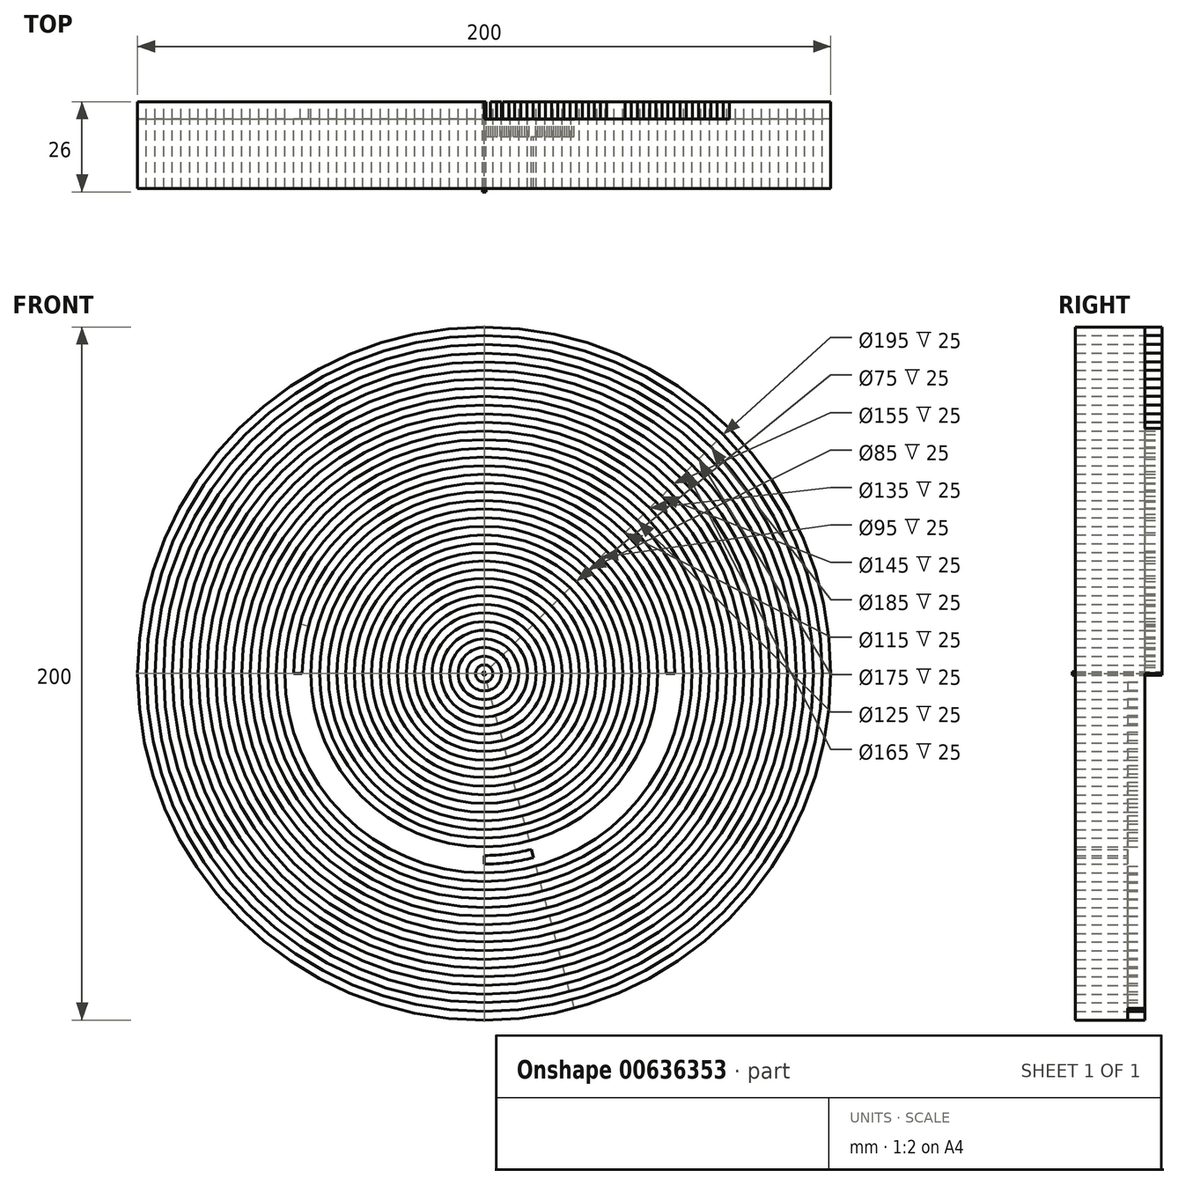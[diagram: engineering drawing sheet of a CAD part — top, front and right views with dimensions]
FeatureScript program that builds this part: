
annotation { "Feature Type Name" : "Feature", "Feature Type Description" : "" }
export const myFeature = defineFeature(function(context is Context, id is Id, definition is map)
    precondition{}
    {
        {
            var Q0;
            Q0=qCreatedBy(makeId("Front.planeOp"),FACE);
            var sketch = newSketch(context, id + "F0", { "sketchPlane" : qUnion([Q0])});
            skCircle(sketch, "E0", {"center": v(0, 0) * mm, "radius": 100 * mm});
            skCircle(sketch, "E1", {"center": v(0, 0) * mm, "radius": 2.5 * mm});
            skCircle(sketch, "E2", {"center": v(0, 0) * mm, "radius": 5 * mm});
            skCircle(sketch, "E3", {"center": v(0, 0) * mm, "radius": 7.5 * mm});
            skCircle(sketch, "E4", {"center": v(0, 0) * mm, "radius": 15 * mm});
            skCircle(sketch, "E5", {"center": v(0, 0) * mm, "radius": 10 * mm});
            skCircle(sketch, "E6", {"center": v(0, 0) * mm, "radius": 12.5 * mm});
            skCircle(sketch, "E7", {"center": v(0, 0) * mm, "radius": 17.5 * mm});
            skCircle(sketch, "E8", {"center": v(0, 0) * mm, "radius": 20 * mm});
            skCircle(sketch, "E9", {"center": v(0, 0) * mm, "radius": 22.5 * mm});
            skCircle(sketch, "E10", {"center": v(0, 0) * mm, "radius": 25 * mm});
            skCircle(sketch, "E11", {"center": v(0, 0) * mm, "radius": 27.5 * mm});
            skCircle(sketch, "E12", {"center": v(0, 0) * mm, "radius": 30 * mm});
            skCircle(sketch, "E13", {"center": v(0, 0) * mm, "radius": 32.5 * mm});
            skCircle(sketch, "E14", {"center": v(0, 0) * mm, "radius": 35 * mm});
            skCircle(sketch, "E15", {"center": v(0, 0) * mm, "radius": 37.5 * mm});
            skCircle(sketch, "E16", {"center": v(0, 0) * mm, "radius": 40 * mm});
            skCircle(sketch, "E17", {"center": v(0, 0) * mm, "radius": 45 * mm});
            skCircle(sketch, "E18", {"center": v(0, 0) * mm, "radius": 50 * mm});
            skCircle(sketch, "E19", {"center": v(0, 0) * mm, "radius": 52.5 * mm});
            skCircle(sketch, "E20", {"center": v(0, 0) * mm, "radius": 55 * mm});
            skCircle(sketch, "E21", {"center": v(0, 0) * mm, "radius": 42.5 * mm});
            skCircle(sketch, "E22", {"center": v(0, 0) * mm, "radius": 47.5 * mm});
            skCircle(sketch, "E23", {"center": v(0, 0) * mm, "radius": 60 * mm});
            skCircle(sketch, "E24", {"center": v(0, 0) * mm, "radius": 57.5 * mm});
            skCircle(sketch, "E25", {"center": v(0, 0) * mm, "radius": 62.5 * mm});
            skCircle(sketch, "E26", {"center": v(0, 0) * mm, "radius": 65 * mm});
            skCircle(sketch, "E27", {"center": v(0, 0) * mm, "radius": 67.5 * mm});
            skCircle(sketch, "E28", {"center": v(0, 0) * mm, "radius": 70 * mm});
            skCircle(sketch, "E29", {"center": v(0, 0) * mm, "radius": 72.5 * mm});
            skCircle(sketch, "E30", {"center": v(0, 0) * mm, "radius": 75 * mm});
            skCircle(sketch, "E31", {"center": v(0, 0) * mm, "radius": 77.5 * mm});
            skCircle(sketch, "E32", {"center": v(0, 0) * mm, "radius": 80 * mm});
            skCircle(sketch, "E33", {"center": v(0, 0) * mm, "radius": 82.5 * mm});
            skCircle(sketch, "E34", {"center": v(0, 0) * mm, "radius": 85 * mm});
            skCircle(sketch, "E35", {"center": v(0, 0) * mm, "radius": 87.5 * mm});
            skCircle(sketch, "E36", {"center": v(0, 0) * mm, "radius": 90 * mm});
            skCircle(sketch, "E37", {"center": v(0, 0) * mm, "radius": 92.5 * mm});
            skCircle(sketch, "E38", {"center": v(0, 0) * mm, "radius": 95 * mm});
            skCircle(sketch, "E39", {"center": v(0, 0) * mm, "radius": 97.5 * mm});
            skLineSegment(sketch, "E40", {"start": v(0, 100) * mm, "end": v(0, -100) * mm});
            skLineSegment(sketch, "E41", {"start": v(100, 0) * mm, "end": v(-100, 0) * mm});
            skLineSegment(sketch, "E42", {"start": v(70.71, 70.71) * mm, "end": v(0, 0) * mm});
            skLineSegment(sketch, "E43", {"start": v(0, 0) * mm, "end": v(25.88, -96.6) * mm});
            skLineSegment(sketch, "E44", {"start": v(25.88, -96.6) * mm, "end": v(0, 0) * mm});
            skLineSegment(sketch, "E45", {"start": v(0, 0) * mm, "end": v(-96.6, 25.88) * mm});
            skCircle(sketch, "E46", {"center": v(0, 0) * mm, "radius": 0.5 * mm});
            skSolve(sketch);
        }
        {
            var Q0;
            {var subQ0=sQuery(id+"F0.wireOp",EDGE,"E42");var subQ1=sQuery(id+"F0.wireOp",EDGE,"E15");var subQ2=makeQuery(id+"F0.imprint","INTERSECT",VERTEX,{"derivedFrom":[subQ1,subQ0]});Q0=makeQuery(id+"F0.imprint","IMPRINT",FACE,{"disambiguationData":[TD([[makeQuery(id+"F0.imprint","IMPRINT",EDGE,{"disambiguationData":[TD([[subQ2,1.0]])],"derivedFrom":subQ1}),-1.0]])]});}
            var Q1;
            {var subQ0=sQuery(id+"F0.wireOp",EDGE,"E41");var subQ1=sQuery(id+"F0.wireOp",EDGE,"E7");var subQ2=makeQuery(id+"F0.imprint","INTERSECT",VERTEX,{"disambiguationData":[OD(0.0)],"derivedFrom":[subQ1,subQ0]});Q1=makeQuery(id+"F0.imprint","IMPRINT",FACE,{"disambiguationData":[TD([[makeQuery(id+"F0.imprint","IMPRINT",EDGE,{"disambiguationData":[TD([[subQ2,1.0]])],"derivedFrom":subQ1}),-1.0]])]});}
            var Q2;
            {var subQ0=sQuery(id+"F0.wireOp",EDGE,"E42");var subQ1=sQuery(id+"F0.wireOp",EDGE,"E26");var subQ2=makeQuery(id+"F0.imprint","INTERSECT",VERTEX,{"derivedFrom":[subQ1,subQ0]});Q2=makeQuery(id+"F0.imprint","IMPRINT",FACE,{"disambiguationData":[TD([[makeQuery(id+"F0.imprint","IMPRINT",EDGE,{"disambiguationData":[TD([[subQ2,-1.0]])],"derivedFrom":subQ1}),-1.0]])]});}
            var Q3;
            {var subQ0=sQuery(id+"F0.wireOp",EDGE,"E45");var subQ1=sQuery(id+"F0.wireOp",EDGE,"E17");var subQ2=makeQuery(id+"F0.imprint","INTERSECT",VERTEX,{"derivedFrom":[subQ1,subQ0]});Q3=makeQuery(id+"F0.imprint","IMPRINT",FACE,{"disambiguationData":[TD([[makeQuery(id+"F0.imprint","IMPRINT",EDGE,{"disambiguationData":[TD([[subQ2,-1.0]])],"derivedFrom":subQ1}),1.0]])]});}
            var Q4;
            {var subQ0=sQuery(id+"F0.wireOp",EDGE,"E40");var subQ1=sQuery(id+"F0.wireOp",EDGE,"E3");var subQ2=makeQuery(id+"F0.imprint","INTERSECT",VERTEX,{"disambiguationData":[OD(1.0)],"derivedFrom":[subQ1,subQ0]});Q4=makeQuery(id+"F0.imprint","IMPRINT",FACE,{"disambiguationData":[TD([[makeQuery(id+"F0.imprint","IMPRINT",EDGE,{"disambiguationData":[TD([[subQ2,-1.0]])],"derivedFrom":subQ1}),-1.0]])]});}
            var Q5;
            {var subQ0=sQuery(id+"F0.wireOp",EDGE,"E42");var subQ1=sQuery(id+"F0.wireOp",EDGE,"E32");var subQ2=makeQuery(id+"F0.imprint","INTERSECT",VERTEX,{"derivedFrom":[subQ1,subQ0]});Q5=makeQuery(id+"F0.imprint","IMPRINT",FACE,{"disambiguationData":[TD([[makeQuery(id+"F0.imprint","IMPRINT",EDGE,{"disambiguationData":[TD([[subQ2,-1.0]])],"derivedFrom":subQ1}),-1.0]])]});}
            var Q6;
            {var subQ0=sQuery(id+"F0.wireOp",EDGE,"E41");var subQ1=sQuery(id+"F0.wireOp",EDGE,"E33");var subQ2=makeQuery(id+"F0.imprint","INTERSECT",VERTEX,{"disambiguationData":[OD(0.0)],"derivedFrom":[subQ1,subQ0]});Q6=makeQuery(id+"F0.imprint","IMPRINT",FACE,{"disambiguationData":[TD([[makeQuery(id+"F0.imprint","IMPRINT",EDGE,{"disambiguationData":[TD([[subQ2,1.0]])],"derivedFrom":subQ1}),-1.0]])]});}
            var Q7;
            {var subQ0=sQuery(id+"F0.wireOp",EDGE,"E41");var subQ1=sQuery(id+"F0.wireOp",EDGE,"E18");var subQ2=makeQuery(id+"F0.imprint","INTERSECT",VERTEX,{"disambiguationData":[OD(1.0)],"derivedFrom":[subQ1,subQ0]});Q7=makeQuery(id+"F0.imprint","IMPRINT",FACE,{"disambiguationData":[TD([[makeQuery(id+"F0.imprint","IMPRINT",EDGE,{"disambiguationData":[TD([[subQ2,-1.0]])],"derivedFrom":subQ1}),-1.0]])]});}
            var Q8;
            {var subQ0=sQuery(id+"F0.wireOp",EDGE,"E42");var subQ1=sQuery(id+"F0.wireOp",EDGE,"E31");var subQ2=makeQuery(id+"F0.imprint","INTERSECT",VERTEX,{"derivedFrom":[subQ1,subQ0]});Q8=makeQuery(id+"F0.imprint","IMPRINT",FACE,{"disambiguationData":[TD([[makeQuery(id+"F0.imprint","IMPRINT",EDGE,{"disambiguationData":[TD([[subQ2,1.0]])],"derivedFrom":subQ1}),-1.0]])]});}
            var Q9;
            {var subQ0=sQuery(id+"F0.wireOp",EDGE,"E45");var subQ1=sQuery(id+"F0.wireOp",EDGE,"E26");var subQ2=makeQuery(id+"F0.imprint","INTERSECT",VERTEX,{"derivedFrom":[subQ1,subQ0]});Q9=makeQuery(id+"F0.imprint","IMPRINT",FACE,{"disambiguationData":[TD([[makeQuery(id+"F0.imprint","IMPRINT",EDGE,{"disambiguationData":[TD([[subQ2,-1.0]])],"derivedFrom":subQ1}),-1.0]])]});}
            var Q10;
            {var subQ0=sQuery(id+"F0.wireOp",EDGE,"E40");var subQ1=sQuery(id+"F0.wireOp",EDGE,"E27");var subQ2=makeQuery(id+"F0.imprint","INTERSECT",VERTEX,{"disambiguationData":[OD(1.0)],"derivedFrom":[subQ1,subQ0]});Q10=makeQuery(id+"F0.imprint","IMPRINT",FACE,{"disambiguationData":[TD([[makeQuery(id+"F0.imprint","IMPRINT",EDGE,{"disambiguationData":[TD([[subQ2,-1.0]])],"derivedFrom":subQ1}),-1.0]])]});}
            var Q11;
            {var subQ0=sQuery(id+"F0.wireOp",EDGE,"E41");var subQ1=sQuery(id+"F0.wireOp",EDGE,"E32");var subQ2=makeQuery(id+"F0.imprint","INTERSECT",VERTEX,{"disambiguationData":[OD(0.0)],"derivedFrom":[subQ1,subQ0]});Q11=makeQuery(id+"F0.imprint","IMPRINT",FACE,{"disambiguationData":[TD([[makeQuery(id+"F0.imprint","IMPRINT",EDGE,{"disambiguationData":[TD([[subQ2,1.0]])],"derivedFrom":subQ1}),-1.0]])]});}
            var Q12;
            {var subQ0=sQuery(id+"F0.wireOp",EDGE,"E40");var subQ1=sQuery(id+"F0.wireOp",EDGE,"E23");var subQ2=makeQuery(id+"F0.imprint","INTERSECT",VERTEX,{"disambiguationData":[OD(0.0)],"derivedFrom":[subQ1,subQ0]});Q12=makeQuery(id+"F0.imprint","IMPRINT",FACE,{"disambiguationData":[TD([[makeQuery(id+"F0.imprint","IMPRINT",EDGE,{"disambiguationData":[TD([[subQ2,-1.0]])],"derivedFrom":subQ1}),1.0]])]});}
            var Q13;
            {var subQ0=sQuery(id+"F0.wireOp",EDGE,"E40");var subQ1=sQuery(id+"F0.wireOp",EDGE,"E14");var subQ2=makeQuery(id+"F0.imprint","INTERSECT",VERTEX,{"disambiguationData":[OD(1.0)],"derivedFrom":[subQ1,subQ0]});Q13=makeQuery(id+"F0.imprint","IMPRINT",FACE,{"disambiguationData":[TD([[makeQuery(id+"F0.imprint","IMPRINT",EDGE,{"disambiguationData":[TD([[subQ2,-1.0]])],"derivedFrom":subQ1}),-1.0]])]});}
            var Q14;
            {var subQ0=sQuery(id+"F0.wireOp",EDGE,"E40");var subQ1=sQuery(id+"F0.wireOp",EDGE,"E26");var subQ2=makeQuery(id+"F0.imprint","INTERSECT",VERTEX,{"disambiguationData":[OD(0.0)],"derivedFrom":[subQ1,subQ0]});Q14=makeQuery(id+"F0.imprint","IMPRINT",FACE,{"disambiguationData":[TD([[makeQuery(id+"F0.imprint","IMPRINT",EDGE,{"disambiguationData":[TD([[subQ2,-1.0]])],"derivedFrom":subQ1}),-1.0]])]});}
            var Q15;
            {var subQ0=sQuery(id+"F0.wireOp",EDGE,"E42");var subQ1=sQuery(id+"F0.wireOp",EDGE,"E12");var subQ2=makeQuery(id+"F0.imprint","INTERSECT",VERTEX,{"derivedFrom":[subQ1,subQ0]});Q15=makeQuery(id+"F0.imprint","IMPRINT",FACE,{"disambiguationData":[TD([[makeQuery(id+"F0.imprint","IMPRINT",EDGE,{"disambiguationData":[TD([[subQ2,-1.0]])],"derivedFrom":subQ1}),-1.0]])]});}
            var Q16;
            {var subQ0=sQuery(id+"F0.wireOp",EDGE,"E45");var subQ1=sQuery(id+"F0.wireOp",EDGE,"E25");var subQ2=makeQuery(id+"F0.imprint","INTERSECT",VERTEX,{"derivedFrom":[subQ1,subQ0]});Q16=makeQuery(id+"F0.imprint","IMPRINT",FACE,{"disambiguationData":[TD([[makeQuery(id+"F0.imprint","IMPRINT",EDGE,{"disambiguationData":[TD([[subQ2,-1.0]])],"derivedFrom":subQ1}),-1.0]])]});}
            var Q17;
            {var subQ0=sQuery(id+"F0.wireOp",EDGE,"E41");var subQ1=sQuery(id+"F0.wireOp",EDGE,"E4");var subQ2=makeQuery(id+"F0.imprint","INTERSECT",VERTEX,{"disambiguationData":[OD(0.0)],"derivedFrom":[subQ1,subQ0]});Q17=makeQuery(id+"F0.imprint","IMPRINT",FACE,{"disambiguationData":[TD([[makeQuery(id+"F0.imprint","IMPRINT",EDGE,{"disambiguationData":[TD([[subQ2,1.0]])],"derivedFrom":subQ1}),-1.0]])]});}
            var Q18;
            {var subQ0=sQuery(id+"F0.wireOp",EDGE,"E45");var subQ1=sQuery(id+"F0.wireOp",EDGE,"E28");var subQ2=makeQuery(id+"F0.imprint","INTERSECT",VERTEX,{"derivedFrom":[subQ1,subQ0]});Q18=makeQuery(id+"F0.imprint","IMPRINT",FACE,{"disambiguationData":[TD([[makeQuery(id+"F0.imprint","IMPRINT",EDGE,{"disambiguationData":[TD([[subQ2,-1.0]])],"derivedFrom":subQ1}),-1.0]])]});}
            var Q19;
            {var subQ0=sQuery(id+"F0.wireOp",EDGE,"E41");var subQ1=sQuery(id+"F0.wireOp",EDGE,"E19");var subQ2=makeQuery(id+"F0.imprint","INTERSECT",VERTEX,{"disambiguationData":[OD(1.0)],"derivedFrom":[subQ1,subQ0]});Q19=makeQuery(id+"F0.imprint","IMPRINT",FACE,{"disambiguationData":[TD([[makeQuery(id+"F0.imprint","IMPRINT",EDGE,{"disambiguationData":[TD([[subQ2,-1.0]])],"derivedFrom":subQ1}),-1.0]])]});}
            var Q20;
            {var subQ0=sQuery(id+"F0.wireOp",EDGE,"E40");var subQ1=sQuery(id+"F0.wireOp",EDGE,"E4");var subQ2=makeQuery(id+"F0.imprint","INTERSECT",VERTEX,{"disambiguationData":[OD(0.0)],"derivedFrom":[subQ1,subQ0]});Q20=makeQuery(id+"F0.imprint","IMPRINT",FACE,{"disambiguationData":[TD([[makeQuery(id+"F0.imprint","IMPRINT",EDGE,{"disambiguationData":[TD([[subQ2,-1.0]])],"derivedFrom":subQ1}),-1.0]])]});}
            var Q21;
            {var subQ0=sQuery(id+"F0.wireOp",EDGE,"E40");var subQ1=sQuery(id+"F0.wireOp",EDGE,"E0");var subQ2=makeQuery(id+"F0.imprint","INTERSECT",VERTEX,{"disambiguationData":[OD(0.0)],"derivedFrom":[subQ1,subQ0]});Q21=makeQuery(id+"F0.imprint","IMPRINT",FACE,{"disambiguationData":[TD([[makeQuery(id+"F0.imprint","IMPRINT",EDGE,{"disambiguationData":[TD([[subQ2,1.0]])],"derivedFrom":subQ1}),1.0]])]});}
            var Q22;
            {var subQ0=sQuery(id+"F0.wireOp",EDGE,"E41");var subQ1=sQuery(id+"F0.wireOp",EDGE,"E18");var subQ2=makeQuery(id+"F0.imprint","INTERSECT",VERTEX,{"disambiguationData":[OD(0.0)],"derivedFrom":[subQ1,subQ0]});Q22=makeQuery(id+"F0.imprint","IMPRINT",FACE,{"disambiguationData":[TD([[makeQuery(id+"F0.imprint","IMPRINT",EDGE,{"disambiguationData":[TD([[subQ2,1.0]])],"derivedFrom":subQ1}),-1.0]])]});}
            var Q23;
            {var subQ0=sQuery(id+"F0.wireOp",EDGE,"E45");var subQ1=sQuery(id+"F0.wireOp",EDGE,"E18");var subQ2=makeQuery(id+"F0.imprint","INTERSECT",VERTEX,{"derivedFrom":[subQ1,subQ0]});Q23=makeQuery(id+"F0.imprint","IMPRINT",FACE,{"disambiguationData":[TD([[makeQuery(id+"F0.imprint","IMPRINT",EDGE,{"disambiguationData":[TD([[subQ2,-1.0]])],"derivedFrom":subQ1}),-1.0]])]});}
            var Q24;
            {var subQ0=sQuery(id+"F0.wireOp",EDGE,"E40");var subQ1=sQuery(id+"F0.wireOp",EDGE,"E33");var subQ2=makeQuery(id+"F0.imprint","INTERSECT",VERTEX,{"disambiguationData":[OD(0.0)],"derivedFrom":[subQ1,subQ0]});Q24=makeQuery(id+"F0.imprint","IMPRINT",FACE,{"disambiguationData":[TD([[makeQuery(id+"F0.imprint","IMPRINT",EDGE,{"disambiguationData":[TD([[subQ2,-1.0]])],"derivedFrom":subQ1}),-1.0]])]});}
            var Q25;
            {var subQ0=sQuery(id+"F0.wireOp",EDGE,"E41");var subQ1=sQuery(id+"F0.wireOp",EDGE,"E10");var subQ2=makeQuery(id+"F0.imprint","INTERSECT",VERTEX,{"disambiguationData":[OD(1.0)],"derivedFrom":[subQ1,subQ0]});Q25=makeQuery(id+"F0.imprint","IMPRINT",FACE,{"disambiguationData":[TD([[makeQuery(id+"F0.imprint","IMPRINT",EDGE,{"disambiguationData":[TD([[subQ2,-1.0]])],"derivedFrom":subQ1}),-1.0]])]});}
            var Q26;
            {var subQ0=sQuery(id+"F0.wireOp",EDGE,"E41");var subQ1=sQuery(id+"F0.wireOp",EDGE,"E11");var subQ2=makeQuery(id+"F0.imprint","INTERSECT",VERTEX,{"disambiguationData":[OD(0.0)],"derivedFrom":[subQ1,subQ0]});Q26=makeQuery(id+"F0.imprint","IMPRINT",FACE,{"disambiguationData":[TD([[makeQuery(id+"F0.imprint","IMPRINT",EDGE,{"disambiguationData":[TD([[subQ2,1.0]])],"derivedFrom":subQ1}),-1.0]])]});}
            var Q27;
            {var subQ0=sQuery(id+"F0.wireOp",EDGE,"E42");var subQ1=sQuery(id+"F0.wireOp",EDGE,"E20");var subQ2=makeQuery(id+"F0.imprint","INTERSECT",VERTEX,{"derivedFrom":[subQ1,subQ0]});Q27=makeQuery(id+"F0.imprint","IMPRINT",FACE,{"disambiguationData":[TD([[makeQuery(id+"F0.imprint","IMPRINT",EDGE,{"disambiguationData":[TD([[subQ2,-1.0]])],"derivedFrom":subQ1}),-1.0]])]});}
            var Q28;
            {var subQ0=sQuery(id+"F0.wireOp",EDGE,"E40");var subQ1=sQuery(id+"F0.wireOp",EDGE,"E34");var subQ2=makeQuery(id+"F0.imprint","INTERSECT",VERTEX,{"disambiguationData":[OD(1.0)],"derivedFrom":[subQ1,subQ0]});Q28=makeQuery(id+"F0.imprint","IMPRINT",FACE,{"disambiguationData":[TD([[makeQuery(id+"F0.imprint","IMPRINT",EDGE,{"disambiguationData":[TD([[subQ2,-1.0]])],"derivedFrom":subQ1}),-1.0]])]});}
            var Q29;
            {var subQ0=sQuery(id+"F0.wireOp",EDGE,"E42");var subQ1=sQuery(id+"F0.wireOp",EDGE,"E3");var subQ2=makeQuery(id+"F0.imprint","INTERSECT",VERTEX,{"derivedFrom":[subQ1,subQ0]});Q29=makeQuery(id+"F0.imprint","IMPRINT",FACE,{"disambiguationData":[TD([[makeQuery(id+"F0.imprint","IMPRINT",EDGE,{"disambiguationData":[TD([[subQ2,1.0]])],"derivedFrom":subQ1}),-1.0]])]});}
            var Q30;
            {var subQ0=sQuery(id+"F0.wireOp",EDGE,"E42");var subQ1=sQuery(id+"F0.wireOp",EDGE,"E16");var subQ2=makeQuery(id+"F0.imprint","INTERSECT",VERTEX,{"derivedFrom":[subQ1,subQ0]});Q30=makeQuery(id+"F0.imprint","IMPRINT",FACE,{"disambiguationData":[TD([[makeQuery(id+"F0.imprint","IMPRINT",EDGE,{"disambiguationData":[TD([[subQ2,1.0]])],"derivedFrom":subQ1}),-1.0]])]});}
            var Q31;
            {var subQ0=sQuery(id+"F0.wireOp",EDGE,"E45");var subQ1=sQuery(id+"F0.wireOp",EDGE,"E38");var subQ2=makeQuery(id+"F0.imprint","INTERSECT",VERTEX,{"derivedFrom":[subQ1,subQ0]});Q31=makeQuery(id+"F0.imprint","IMPRINT",FACE,{"disambiguationData":[TD([[makeQuery(id+"F0.imprint","IMPRINT",EDGE,{"disambiguationData":[TD([[subQ2,-1.0]])],"derivedFrom":subQ1}),-1.0]])]});}
            var Q32;
            {var subQ0=sQuery(id+"F0.wireOp",EDGE,"E40");var subQ1=sQuery(id+"F0.wireOp",EDGE,"E17");var subQ2=makeQuery(id+"F0.imprint","INTERSECT",VERTEX,{"disambiguationData":[OD(0.0)],"derivedFrom":[subQ1,subQ0]});Q32=makeQuery(id+"F0.imprint","IMPRINT",FACE,{"disambiguationData":[TD([[makeQuery(id+"F0.imprint","IMPRINT",EDGE,{"disambiguationData":[TD([[subQ2,-1.0]])],"derivedFrom":subQ1}),-1.0]])]});}
            var Q33;
            {var subQ0=sQuery(id+"F0.wireOp",EDGE,"E41");var subQ1=sQuery(id+"F0.wireOp",EDGE,"E10");var subQ2=makeQuery(id+"F0.imprint","INTERSECT",VERTEX,{"disambiguationData":[OD(0.0)],"derivedFrom":[subQ1,subQ0]});Q33=makeQuery(id+"F0.imprint","IMPRINT",FACE,{"disambiguationData":[TD([[makeQuery(id+"F0.imprint","IMPRINT",EDGE,{"disambiguationData":[TD([[subQ2,1.0]])],"derivedFrom":subQ1}),-1.0]])]});}
            var Q34;
            {var subQ0=sQuery(id+"F0.wireOp",EDGE,"E40");var subQ1=sQuery(id+"F0.wireOp",EDGE,"E18");var subQ2=makeQuery(id+"F0.imprint","INTERSECT",VERTEX,{"disambiguationData":[OD(1.0)],"derivedFrom":[subQ1,subQ0]});Q34=makeQuery(id+"F0.imprint","IMPRINT",FACE,{"disambiguationData":[TD([[makeQuery(id+"F0.imprint","IMPRINT",EDGE,{"disambiguationData":[TD([[subQ2,-1.0]])],"derivedFrom":subQ1}),1.0]])]});}
            var Q35;
            {var subQ0=sQuery(id+"F0.wireOp",EDGE,"E41");var subQ1=sQuery(id+"F0.wireOp",EDGE,"E4");var subQ2=makeQuery(id+"F0.imprint","INTERSECT",VERTEX,{"disambiguationData":[OD(0.0)],"derivedFrom":[subQ1,subQ0]});Q35=makeQuery(id+"F0.imprint","IMPRINT",FACE,{"disambiguationData":[TD([[makeQuery(id+"F0.imprint","IMPRINT",EDGE,{"disambiguationData":[TD([[subQ2,1.0]])],"derivedFrom":subQ1}),1.0]])]});}
            var Q36;
            {var subQ0=sQuery(id+"F0.wireOp",EDGE,"E42");var subQ1=sQuery(id+"F0.wireOp",EDGE,"E17");var subQ2=makeQuery(id+"F0.imprint","INTERSECT",VERTEX,{"derivedFrom":[subQ1,subQ0]});Q36=makeQuery(id+"F0.imprint","IMPRINT",FACE,{"disambiguationData":[TD([[makeQuery(id+"F0.imprint","IMPRINT",EDGE,{"disambiguationData":[TD([[subQ2,1.0]])],"derivedFrom":subQ1}),-1.0]])]});}
            var Q37;
            {var subQ0=sQuery(id+"F0.wireOp",EDGE,"E40");var subQ1=sQuery(id+"F0.wireOp",EDGE,"E7");var subQ2=makeQuery(id+"F0.imprint","INTERSECT",VERTEX,{"disambiguationData":[OD(1.0)],"derivedFrom":[subQ1,subQ0]});Q37=makeQuery(id+"F0.imprint","IMPRINT",FACE,{"disambiguationData":[TD([[makeQuery(id+"F0.imprint","IMPRINT",EDGE,{"disambiguationData":[TD([[subQ2,-1.0]])],"derivedFrom":subQ1}),-1.0]])]});}
            var Q38;
            {var subQ0=sQuery(id+"F0.wireOp",EDGE,"E42");var subQ1=sQuery(id+"F0.wireOp",EDGE,"E28");var subQ2=makeQuery(id+"F0.imprint","INTERSECT",VERTEX,{"derivedFrom":[subQ1,subQ0]});Q38=makeQuery(id+"F0.imprint","IMPRINT",FACE,{"disambiguationData":[TD([[makeQuery(id+"F0.imprint","IMPRINT",EDGE,{"disambiguationData":[TD([[subQ2,1.0]])],"derivedFrom":subQ1}),-1.0]])]});}
            var Q39;
            {var subQ0=sQuery(id+"F0.wireOp",EDGE,"E40");var subQ1=sQuery(id+"F0.wireOp",EDGE,"E23");var subQ2=makeQuery(id+"F0.imprint","INTERSECT",VERTEX,{"disambiguationData":[OD(1.0)],"derivedFrom":[subQ1,subQ0]});Q39=makeQuery(id+"F0.imprint","IMPRINT",FACE,{"disambiguationData":[TD([[makeQuery(id+"F0.imprint","IMPRINT",EDGE,{"disambiguationData":[TD([[subQ2,-1.0]])],"derivedFrom":subQ1}),-1.0]])]});}
            var Q40;
            {var subQ0=sQuery(id+"F0.wireOp",EDGE,"E42");var subQ1=sQuery(id+"F0.wireOp",EDGE,"E23");var subQ2=makeQuery(id+"F0.imprint","INTERSECT",VERTEX,{"derivedFrom":[subQ1,subQ0]});Q40=makeQuery(id+"F0.imprint","IMPRINT",FACE,{"disambiguationData":[TD([[makeQuery(id+"F0.imprint","IMPRINT",EDGE,{"disambiguationData":[TD([[subQ2,1.0]])],"derivedFrom":subQ1}),-1.0]])]});}
            var Q41;
            {var subQ0=sQuery(id+"F0.wireOp",EDGE,"E41");var subQ1=sQuery(id+"F0.wireOp",EDGE,"E2");var subQ2=makeQuery(id+"F0.imprint","INTERSECT",VERTEX,{"disambiguationData":[OD(1.0)],"derivedFrom":[subQ1,subQ0]});Q41=makeQuery(id+"F0.imprint","IMPRINT",FACE,{"disambiguationData":[TD([[makeQuery(id+"F0.imprint","IMPRINT",EDGE,{"disambiguationData":[TD([[subQ2,-1.0]])],"derivedFrom":subQ1}),-1.0]])]});}
            var Q42;
            {var subQ0=sQuery(id+"F0.wireOp",EDGE,"E42");var subQ1=sQuery(id+"F0.wireOp",EDGE,"E7");var subQ2=makeQuery(id+"F0.imprint","INTERSECT",VERTEX,{"derivedFrom":[subQ1,subQ0]});Q42=makeQuery(id+"F0.imprint","IMPRINT",FACE,{"disambiguationData":[TD([[makeQuery(id+"F0.imprint","IMPRINT",EDGE,{"disambiguationData":[TD([[subQ2,-1.0]])],"derivedFrom":subQ1}),-1.0]])]});}
            var Q43;
            {var subQ0=sQuery(id+"F0.wireOp",EDGE,"E41");var subQ1=sQuery(id+"F0.wireOp",EDGE,"E4");var subQ2=makeQuery(id+"F0.imprint","INTERSECT",VERTEX,{"disambiguationData":[OD(1.0)],"derivedFrom":[subQ1,subQ0]});Q43=makeQuery(id+"F0.imprint","IMPRINT",FACE,{"disambiguationData":[TD([[makeQuery(id+"F0.imprint","IMPRINT",EDGE,{"disambiguationData":[TD([[subQ2,-1.0]])],"derivedFrom":subQ1}),-1.0]])]});}
            var Q44;
            {var subQ0=sQuery(id+"F0.wireOp",EDGE,"E40");var subQ1=sQuery(id+"F0.wireOp",EDGE,"E2");var subQ2=makeQuery(id+"F0.imprint","INTERSECT",VERTEX,{"disambiguationData":[OD(0.0)],"derivedFrom":[subQ1,subQ0]});Q44=makeQuery(id+"F0.imprint","IMPRINT",FACE,{"disambiguationData":[TD([[makeQuery(id+"F0.imprint","IMPRINT",EDGE,{"disambiguationData":[TD([[subQ2,-1.0]])],"derivedFrom":subQ1}),-1.0]])]});}
            var Q45;
            {var subQ0=sQuery(id+"F0.wireOp",EDGE,"E40");var subQ1=sQuery(id+"F0.wireOp",EDGE,"E20");var subQ2=makeQuery(id+"F0.imprint","INTERSECT",VERTEX,{"disambiguationData":[OD(1.0)],"derivedFrom":[subQ1,subQ0]});Q45=makeQuery(id+"F0.imprint","IMPRINT",FACE,{"disambiguationData":[TD([[makeQuery(id+"F0.imprint","IMPRINT",EDGE,{"disambiguationData":[TD([[subQ2,-1.0]])],"derivedFrom":subQ1}),-1.0]])]});}
            var Q46;
            {var subQ0=sQuery(id+"F0.wireOp",EDGE,"E40");var subQ1=sQuery(id+"F0.wireOp",EDGE,"E31");var subQ2=makeQuery(id+"F0.imprint","INTERSECT",VERTEX,{"disambiguationData":[OD(1.0)],"derivedFrom":[subQ1,subQ0]});Q46=makeQuery(id+"F0.imprint","IMPRINT",FACE,{"disambiguationData":[TD([[makeQuery(id+"F0.imprint","IMPRINT",EDGE,{"disambiguationData":[TD([[subQ2,-1.0]])],"derivedFrom":subQ1}),-1.0]])]});}
            var Q47;
            {var subQ0=sQuery(id+"F0.wireOp",EDGE,"E45");var subQ1=sQuery(id+"F0.wireOp",EDGE,"E31");var subQ2=makeQuery(id+"F0.imprint","INTERSECT",VERTEX,{"derivedFrom":[subQ1,subQ0]});Q47=makeQuery(id+"F0.imprint","IMPRINT",FACE,{"disambiguationData":[TD([[makeQuery(id+"F0.imprint","IMPRINT",EDGE,{"disambiguationData":[TD([[subQ2,-1.0]])],"derivedFrom":subQ1}),-1.0]])]});}
            var Q48;
            {var subQ0=sQuery(id+"F0.wireOp",EDGE,"E40");var subQ1=sQuery(id+"F0.wireOp",EDGE,"E18");var subQ2=makeQuery(id+"F0.imprint","INTERSECT",VERTEX,{"disambiguationData":[OD(0.0)],"derivedFrom":[subQ1,subQ0]});Q48=makeQuery(id+"F0.imprint","IMPRINT",FACE,{"disambiguationData":[TD([[makeQuery(id+"F0.imprint","IMPRINT",EDGE,{"disambiguationData":[TD([[subQ2,-1.0]])],"derivedFrom":subQ1}),-1.0]])]});}
            var Q49;
            {var subQ0=sQuery(id+"F0.wireOp",EDGE,"E42");var subQ1=sQuery(id+"F0.wireOp",EDGE,"E7");var subQ2=makeQuery(id+"F0.imprint","INTERSECT",VERTEX,{"derivedFrom":[subQ1,subQ0]});Q49=makeQuery(id+"F0.imprint","IMPRINT",FACE,{"disambiguationData":[TD([[makeQuery(id+"F0.imprint","IMPRINT",EDGE,{"disambiguationData":[TD([[subQ2,1.0]])],"derivedFrom":subQ1}),-1.0]])]});}
            var Q50;
            {var subQ0=sQuery(id+"F0.wireOp",EDGE,"E41");var subQ1=sQuery(id+"F0.wireOp",EDGE,"E27");var subQ2=makeQuery(id+"F0.imprint","INTERSECT",VERTEX,{"disambiguationData":[OD(1.0)],"derivedFrom":[subQ1,subQ0]});Q50=makeQuery(id+"F0.imprint","IMPRINT",FACE,{"disambiguationData":[TD([[makeQuery(id+"F0.imprint","IMPRINT",EDGE,{"disambiguationData":[TD([[subQ2,-1.0]])],"derivedFrom":subQ1}),-1.0]])]});}
            var Q51;
            {var subQ0=sQuery(id+"F0.wireOp",EDGE,"E41");var subQ1=sQuery(id+"F0.wireOp",EDGE,"E7");var subQ2=makeQuery(id+"F0.imprint","INTERSECT",VERTEX,{"disambiguationData":[OD(1.0)],"derivedFrom":[subQ1,subQ0]});Q51=makeQuery(id+"F0.imprint","IMPRINT",FACE,{"disambiguationData":[TD([[makeQuery(id+"F0.imprint","IMPRINT",EDGE,{"disambiguationData":[TD([[subQ2,-1.0]])],"derivedFrom":subQ1}),-1.0]])]});}
            var Q52;
            {var subQ0=sQuery(id+"F0.wireOp",EDGE,"E41");var subQ1=sQuery(id+"F0.wireOp",EDGE,"E19");var subQ2=makeQuery(id+"F0.imprint","INTERSECT",VERTEX,{"disambiguationData":[OD(0.0)],"derivedFrom":[subQ1,subQ0]});Q52=makeQuery(id+"F0.imprint","IMPRINT",FACE,{"disambiguationData":[TD([[makeQuery(id+"F0.imprint","IMPRINT",EDGE,{"disambiguationData":[TD([[subQ2,1.0]])],"derivedFrom":subQ1}),-1.0]])]});}
            var Q53;
            {var subQ0=sQuery(id+"F0.wireOp",EDGE,"E45");var subQ1=sQuery(id+"F0.wireOp",EDGE,"E11");var subQ2=makeQuery(id+"F0.imprint","INTERSECT",VERTEX,{"derivedFrom":[subQ1,subQ0]});Q53=makeQuery(id+"F0.imprint","IMPRINT",FACE,{"disambiguationData":[TD([[makeQuery(id+"F0.imprint","IMPRINT",EDGE,{"disambiguationData":[TD([[subQ2,-1.0]])],"derivedFrom":subQ1}),-1.0]])]});}
            var Q54;
            {var subQ0=sQuery(id+"F0.wireOp",EDGE,"E40");var subQ1=sQuery(id+"F0.wireOp",EDGE,"E19");var subQ2=makeQuery(id+"F0.imprint","INTERSECT",VERTEX,{"disambiguationData":[OD(0.0)],"derivedFrom":[subQ1,subQ0]});Q54=makeQuery(id+"F0.imprint","IMPRINT",FACE,{"disambiguationData":[TD([[makeQuery(id+"F0.imprint","IMPRINT",EDGE,{"disambiguationData":[TD([[subQ2,-1.0]])],"derivedFrom":subQ1}),-1.0]])]});}
            var Q55;
            {var subQ0=sQuery(id+"F0.wireOp",EDGE,"E42");var subQ1=sQuery(id+"F0.wireOp",EDGE,"E10");var subQ2=makeQuery(id+"F0.imprint","INTERSECT",VERTEX,{"derivedFrom":[subQ1,subQ0]});Q55=makeQuery(id+"F0.imprint","IMPRINT",FACE,{"disambiguationData":[TD([[makeQuery(id+"F0.imprint","IMPRINT",EDGE,{"disambiguationData":[TD([[subQ2,1.0]])],"derivedFrom":subQ1}),-1.0]])]});}
            var Q56;
            {var subQ0=sQuery(id+"F0.wireOp",EDGE,"E40");var subQ1=sQuery(id+"F0.wireOp",EDGE,"E0");var subQ2=makeQuery(id+"F0.imprint","INTERSECT",VERTEX,{"disambiguationData":[OD(0.0)],"derivedFrom":[subQ1,subQ0]});Q56=makeQuery(id+"F0.imprint","IMPRINT",FACE,{"disambiguationData":[TD([[makeQuery(id+"F0.imprint","IMPRINT",EDGE,{"disambiguationData":[TD([[subQ2,-1.0]])],"derivedFrom":subQ1}),1.0]])]});}
            var Q57;
            {var subQ0=sQuery(id+"F0.wireOp",EDGE,"E40");var subQ1=sQuery(id+"F0.wireOp",EDGE,"E4");var subQ2=makeQuery(id+"F0.imprint","INTERSECT",VERTEX,{"disambiguationData":[OD(1.0)],"derivedFrom":[subQ1,subQ0]});Q57=makeQuery(id+"F0.imprint","IMPRINT",FACE,{"disambiguationData":[TD([[makeQuery(id+"F0.imprint","IMPRINT",EDGE,{"disambiguationData":[TD([[subQ2,-1.0]])],"derivedFrom":subQ1}),1.0]])]});}
            var Q58;
            {var subQ0=sQuery(id+"F0.wireOp",EDGE,"E41");var subQ1=sQuery(id+"F0.wireOp",EDGE,"E30");var subQ2=makeQuery(id+"F0.imprint","INTERSECT",VERTEX,{"disambiguationData":[OD(0.0)],"derivedFrom":[subQ1,subQ0]});Q58=makeQuery(id+"F0.imprint","IMPRINT",FACE,{"disambiguationData":[TD([[makeQuery(id+"F0.imprint","IMPRINT",EDGE,{"disambiguationData":[TD([[subQ2,1.0]])],"derivedFrom":subQ1}),-1.0]])]});}
            var Q59;
            {var subQ0=sQuery(id+"F0.wireOp",EDGE,"E41");var subQ1=sQuery(id+"F0.wireOp",EDGE,"E29");var subQ2=makeQuery(id+"F0.imprint","INTERSECT",VERTEX,{"disambiguationData":[OD(0.0)],"derivedFrom":[subQ1,subQ0]});Q59=makeQuery(id+"F0.imprint","IMPRINT",FACE,{"disambiguationData":[TD([[makeQuery(id+"F0.imprint","IMPRINT",EDGE,{"disambiguationData":[TD([[subQ2,1.0]])],"derivedFrom":subQ1}),-1.0]])]});}
            var Q60;
            {var subQ0=sQuery(id+"F0.wireOp",EDGE,"E45");var subQ1=sQuery(id+"F0.wireOp",EDGE,"E8");var subQ2=makeQuery(id+"F0.imprint","INTERSECT",VERTEX,{"derivedFrom":[subQ1,subQ0]});Q60=makeQuery(id+"F0.imprint","IMPRINT",FACE,{"disambiguationData":[TD([[makeQuery(id+"F0.imprint","IMPRINT",EDGE,{"disambiguationData":[TD([[subQ2,-1.0]])],"derivedFrom":subQ1}),-1.0]])]});}
            var Q61;
            {var subQ0=sQuery(id+"F0.wireOp",EDGE,"E42");var subQ1=sQuery(id+"F0.wireOp",EDGE,"E5");var subQ2=makeQuery(id+"F0.imprint","INTERSECT",VERTEX,{"derivedFrom":[subQ1,subQ0]});Q61=makeQuery(id+"F0.imprint","IMPRINT",FACE,{"disambiguationData":[TD([[makeQuery(id+"F0.imprint","IMPRINT",EDGE,{"disambiguationData":[TD([[subQ2,1.0]])],"derivedFrom":subQ1}),-1.0]])]});}
            var Q62;
            {var subQ0=sQuery(id+"F0.wireOp",EDGE,"E40");var subQ1=sQuery(id+"F0.wireOp",EDGE,"E25");var subQ2=makeQuery(id+"F0.imprint","INTERSECT",VERTEX,{"disambiguationData":[OD(0.0)],"derivedFrom":[subQ1,subQ0]});Q62=makeQuery(id+"F0.imprint","IMPRINT",FACE,{"disambiguationData":[TD([[makeQuery(id+"F0.imprint","IMPRINT",EDGE,{"disambiguationData":[TD([[subQ2,-1.0]])],"derivedFrom":subQ1}),-1.0]])]});}
            var Q63;
            {var subQ0=sQuery(id+"F0.wireOp",EDGE,"E41");var subQ1=sQuery(id+"F0.wireOp",EDGE,"E9");var subQ2=makeQuery(id+"F0.imprint","INTERSECT",VERTEX,{"disambiguationData":[OD(0.0)],"derivedFrom":[subQ1,subQ0]});Q63=makeQuery(id+"F0.imprint","IMPRINT",FACE,{"disambiguationData":[TD([[makeQuery(id+"F0.imprint","IMPRINT",EDGE,{"disambiguationData":[TD([[subQ2,1.0]])],"derivedFrom":subQ1}),-1.0]])]});}
            var Q64;
            {var subQ0=sQuery(id+"F0.wireOp",EDGE,"E45");var subQ1=sQuery(id+"F0.wireOp",EDGE,"E9");var subQ2=makeQuery(id+"F0.imprint","INTERSECT",VERTEX,{"derivedFrom":[subQ1,subQ0]});Q64=makeQuery(id+"F0.imprint","IMPRINT",FACE,{"disambiguationData":[TD([[makeQuery(id+"F0.imprint","IMPRINT",EDGE,{"disambiguationData":[TD([[subQ2,-1.0]])],"derivedFrom":subQ1}),-1.0]])]});}
            var Q65;
            {var subQ0=sQuery(id+"F0.wireOp",EDGE,"E40");var subQ1=sQuery(id+"F0.wireOp",EDGE,"E18");var subQ2=makeQuery(id+"F0.imprint","INTERSECT",VERTEX,{"disambiguationData":[OD(0.0)],"derivedFrom":[subQ1,subQ0]});Q65=makeQuery(id+"F0.imprint","IMPRINT",FACE,{"disambiguationData":[TD([[makeQuery(id+"F0.imprint","IMPRINT",EDGE,{"disambiguationData":[TD([[subQ2,-1.0]])],"derivedFrom":subQ1}),1.0]])]});}
            var Q66;
            {var subQ0=sQuery(id+"F0.wireOp",EDGE,"E40");var subQ1=sQuery(id+"F0.wireOp",EDGE,"E15");var subQ2=makeQuery(id+"F0.imprint","INTERSECT",VERTEX,{"disambiguationData":[OD(0.0)],"derivedFrom":[subQ1,subQ0]});Q66=makeQuery(id+"F0.imprint","IMPRINT",FACE,{"disambiguationData":[TD([[makeQuery(id+"F0.imprint","IMPRINT",EDGE,{"disambiguationData":[TD([[subQ2,-1.0]])],"derivedFrom":subQ1}),-1.0]])]});}
            var Q67;
            {var subQ0=sQuery(id+"F0.wireOp",EDGE,"E40");var subQ1=sQuery(id+"F0.wireOp",EDGE,"E20");var subQ2=makeQuery(id+"F0.imprint","INTERSECT",VERTEX,{"disambiguationData":[OD(0.0)],"derivedFrom":[subQ1,subQ0]});Q67=makeQuery(id+"F0.imprint","IMPRINT",FACE,{"disambiguationData":[TD([[makeQuery(id+"F0.imprint","IMPRINT",EDGE,{"disambiguationData":[TD([[subQ2,-1.0]])],"derivedFrom":subQ1}),-1.0]])]});}
            var Q68;
            {var subQ0=sQuery(id+"F0.wireOp",EDGE,"E42");var subQ1=sQuery(id+"F0.wireOp",EDGE,"E3");var subQ2=makeQuery(id+"F0.imprint","INTERSECT",VERTEX,{"derivedFrom":[subQ1,subQ0]});Q68=makeQuery(id+"F0.imprint","IMPRINT",FACE,{"disambiguationData":[TD([[makeQuery(id+"F0.imprint","IMPRINT",EDGE,{"disambiguationData":[TD([[subQ2,-1.0]])],"derivedFrom":subQ1}),-1.0]])]});}
            var Q69;
            {var subQ0=sQuery(id+"F0.wireOp",EDGE,"E45");var subQ1=sQuery(id+"F0.wireOp",EDGE,"E19");var subQ2=makeQuery(id+"F0.imprint","INTERSECT",VERTEX,{"derivedFrom":[subQ1,subQ0]});Q69=makeQuery(id+"F0.imprint","IMPRINT",FACE,{"disambiguationData":[TD([[makeQuery(id+"F0.imprint","IMPRINT",EDGE,{"disambiguationData":[TD([[subQ2,-1.0]])],"derivedFrom":subQ1}),-1.0]])]});}
            var Q70;
            {var subQ0=sQuery(id+"F0.wireOp",EDGE,"E45");var subQ1=sQuery(id+"F0.wireOp",EDGE,"E36");var subQ2=makeQuery(id+"F0.imprint","INTERSECT",VERTEX,{"derivedFrom":[subQ1,subQ0]});Q70=makeQuery(id+"F0.imprint","IMPRINT",FACE,{"disambiguationData":[TD([[makeQuery(id+"F0.imprint","IMPRINT",EDGE,{"disambiguationData":[TD([[subQ2,-1.0]])],"derivedFrom":subQ1}),-1.0]])]});}
            var Q71;
            {var subQ0=sQuery(id+"F0.wireOp",EDGE,"E42");var subQ1=sQuery(id+"F0.wireOp",EDGE,"E13");var subQ2=makeQuery(id+"F0.imprint","INTERSECT",VERTEX,{"derivedFrom":[subQ1,subQ0]});Q71=makeQuery(id+"F0.imprint","IMPRINT",FACE,{"disambiguationData":[TD([[makeQuery(id+"F0.imprint","IMPRINT",EDGE,{"disambiguationData":[TD([[subQ2,-1.0]])],"derivedFrom":subQ1}),-1.0]])]});}
            var Q72;
            {var subQ0=sQuery(id+"F0.wireOp",EDGE,"E40");var subQ1=sQuery(id+"F0.wireOp",EDGE,"E30");var subQ2=makeQuery(id+"F0.imprint","INTERSECT",VERTEX,{"disambiguationData":[OD(0.0)],"derivedFrom":[subQ1,subQ0]});Q72=makeQuery(id+"F0.imprint","IMPRINT",FACE,{"disambiguationData":[TD([[makeQuery(id+"F0.imprint","IMPRINT",EDGE,{"disambiguationData":[TD([[subQ2,-1.0]])],"derivedFrom":subQ1}),-1.0]])]});}
            var Q73;
            {var subQ0=sQuery(id+"F0.wireOp",EDGE,"E41");var subQ1=sQuery(id+"F0.wireOp",EDGE,"E17");var subQ2=makeQuery(id+"F0.imprint","INTERSECT",VERTEX,{"disambiguationData":[OD(0.0)],"derivedFrom":[subQ1,subQ0]});Q73=makeQuery(id+"F0.imprint","IMPRINT",FACE,{"disambiguationData":[TD([[makeQuery(id+"F0.imprint","IMPRINT",EDGE,{"disambiguationData":[TD([[subQ2,1.0]])],"derivedFrom":subQ1}),1.0]])]});}
            var Q74;
            {var subQ0=sQuery(id+"F0.wireOp",EDGE,"E42");var subQ1=sQuery(id+"F0.wireOp",EDGE,"E35");var subQ2=makeQuery(id+"F0.imprint","INTERSECT",VERTEX,{"derivedFrom":[subQ1,subQ0]});Q74=makeQuery(id+"F0.imprint","IMPRINT",FACE,{"disambiguationData":[TD([[makeQuery(id+"F0.imprint","IMPRINT",EDGE,{"disambiguationData":[TD([[subQ2,-1.0]])],"derivedFrom":subQ1}),-1.0]])]});}
            var Q75;
            {var subQ0=sQuery(id+"F0.wireOp",EDGE,"E41");var subQ1=sQuery(id+"F0.wireOp",EDGE,"E31");var subQ2=makeQuery(id+"F0.imprint","INTERSECT",VERTEX,{"disambiguationData":[OD(1.0)],"derivedFrom":[subQ1,subQ0]});Q75=makeQuery(id+"F0.imprint","IMPRINT",FACE,{"disambiguationData":[TD([[makeQuery(id+"F0.imprint","IMPRINT",EDGE,{"disambiguationData":[TD([[subQ2,-1.0]])],"derivedFrom":subQ1}),-1.0]])]});}
            var Q76;
            {var subQ0=sQuery(id+"F0.wireOp",EDGE,"E42");var subQ1=sQuery(id+"F0.wireOp",EDGE,"E38");var subQ2=makeQuery(id+"F0.imprint","INTERSECT",VERTEX,{"derivedFrom":[subQ1,subQ0]});Q76=makeQuery(id+"F0.imprint","IMPRINT",FACE,{"disambiguationData":[TD([[makeQuery(id+"F0.imprint","IMPRINT",EDGE,{"disambiguationData":[TD([[subQ2,-1.0]])],"derivedFrom":subQ1}),-1.0]])]});}
            var Q77;
            {var subQ0=sQuery(id+"F0.wireOp",EDGE,"E40");var subQ1=sQuery(id+"F0.wireOp",EDGE,"E23");var subQ2=makeQuery(id+"F0.imprint","INTERSECT",VERTEX,{"disambiguationData":[OD(0.0)],"derivedFrom":[subQ1,subQ0]});Q77=makeQuery(id+"F0.imprint","IMPRINT",FACE,{"disambiguationData":[TD([[makeQuery(id+"F0.imprint","IMPRINT",EDGE,{"disambiguationData":[TD([[subQ2,-1.0]])],"derivedFrom":subQ1}),-1.0]])]});}
            var Q78;
            {var subQ0=sQuery(id+"F0.wireOp",EDGE,"E45");var subQ1=sQuery(id+"F0.wireOp",EDGE,"E29");var subQ2=makeQuery(id+"F0.imprint","INTERSECT",VERTEX,{"derivedFrom":[subQ1,subQ0]});Q78=makeQuery(id+"F0.imprint","IMPRINT",FACE,{"disambiguationData":[TD([[makeQuery(id+"F0.imprint","IMPRINT",EDGE,{"disambiguationData":[TD([[subQ2,-1.0]])],"derivedFrom":subQ1}),-1.0]])]});}
            var Q79;
            {var subQ0=sQuery(id+"F0.wireOp",EDGE,"E40");var subQ1=sQuery(id+"F0.wireOp",EDGE,"E5");var subQ2=makeQuery(id+"F0.imprint","INTERSECT",VERTEX,{"disambiguationData":[OD(1.0)],"derivedFrom":[subQ1,subQ0]});Q79=makeQuery(id+"F0.imprint","IMPRINT",FACE,{"disambiguationData":[TD([[makeQuery(id+"F0.imprint","IMPRINT",EDGE,{"disambiguationData":[TD([[subQ2,-1.0]])],"derivedFrom":subQ1}),-1.0]])]});}
            var Q80;
            {var subQ0=sQuery(id+"F0.wireOp",EDGE,"E40");var subQ1=sQuery(id+"F0.wireOp",EDGE,"E27");var subQ2=makeQuery(id+"F0.imprint","INTERSECT",VERTEX,{"disambiguationData":[OD(0.0)],"derivedFrom":[subQ1,subQ0]});Q80=makeQuery(id+"F0.imprint","IMPRINT",FACE,{"disambiguationData":[TD([[makeQuery(id+"F0.imprint","IMPRINT",EDGE,{"disambiguationData":[TD([[subQ2,-1.0]])],"derivedFrom":subQ1}),-1.0]])]});}
            var Q81;
            {var subQ0=sQuery(id+"F0.wireOp",EDGE,"E41");var subQ1=sQuery(id+"F0.wireOp",EDGE,"E28");var subQ2=makeQuery(id+"F0.imprint","INTERSECT",VERTEX,{"disambiguationData":[OD(1.0)],"derivedFrom":[subQ1,subQ0]});Q81=makeQuery(id+"F0.imprint","IMPRINT",FACE,{"disambiguationData":[TD([[makeQuery(id+"F0.imprint","IMPRINT",EDGE,{"disambiguationData":[TD([[subQ2,-1.0]])],"derivedFrom":subQ1}),-1.0]])]});}
            var Q82;
            {var subQ0=sQuery(id+"F0.wireOp",EDGE,"E41");var subQ1=sQuery(id+"F0.wireOp",EDGE,"E35");var subQ2=makeQuery(id+"F0.imprint","INTERSECT",VERTEX,{"disambiguationData":[OD(0.0)],"derivedFrom":[subQ1,subQ0]});Q82=makeQuery(id+"F0.imprint","IMPRINT",FACE,{"disambiguationData":[TD([[makeQuery(id+"F0.imprint","IMPRINT",EDGE,{"disambiguationData":[TD([[subQ2,1.0]])],"derivedFrom":subQ1}),-1.0]])]});}
            var Q83;
            {var subQ0=sQuery(id+"F0.wireOp",EDGE,"E42");var subQ1=sQuery(id+"F0.wireOp",EDGE,"E33");var subQ2=makeQuery(id+"F0.imprint","INTERSECT",VERTEX,{"derivedFrom":[subQ1,subQ0]});Q83=makeQuery(id+"F0.imprint","IMPRINT",FACE,{"disambiguationData":[TD([[makeQuery(id+"F0.imprint","IMPRINT",EDGE,{"disambiguationData":[TD([[subQ2,-1.0]])],"derivedFrom":subQ1}),-1.0]])]});}
            var Q84;
            {var subQ0=sQuery(id+"F0.wireOp",EDGE,"E42");var subQ1=sQuery(id+"F0.wireOp",EDGE,"E14");var subQ2=makeQuery(id+"F0.imprint","INTERSECT",VERTEX,{"derivedFrom":[subQ1,subQ0]});Q84=makeQuery(id+"F0.imprint","IMPRINT",FACE,{"disambiguationData":[TD([[makeQuery(id+"F0.imprint","IMPRINT",EDGE,{"disambiguationData":[TD([[subQ2,-1.0]])],"derivedFrom":subQ1}),-1.0]])]});}
            var Q85;
            {var subQ0=sQuery(id+"F0.wireOp",EDGE,"E41");var subQ1=sQuery(id+"F0.wireOp",EDGE,"E20");var subQ2=makeQuery(id+"F0.imprint","INTERSECT",VERTEX,{"disambiguationData":[OD(1.0)],"derivedFrom":[subQ1,subQ0]});Q85=makeQuery(id+"F0.imprint","IMPRINT",FACE,{"disambiguationData":[TD([[makeQuery(id+"F0.imprint","IMPRINT",EDGE,{"disambiguationData":[TD([[subQ2,-1.0]])],"derivedFrom":subQ1}),-1.0]])]});}
            var Q86;
            {var subQ0=sQuery(id+"F0.wireOp",EDGE,"E42");var subQ1=sQuery(id+"F0.wireOp",EDGE,"E11");var subQ2=makeQuery(id+"F0.imprint","INTERSECT",VERTEX,{"derivedFrom":[subQ1,subQ0]});Q86=makeQuery(id+"F0.imprint","IMPRINT",FACE,{"disambiguationData":[TD([[makeQuery(id+"F0.imprint","IMPRINT",EDGE,{"disambiguationData":[TD([[subQ2,1.0]])],"derivedFrom":subQ1}),-1.0]])]});}
            var Q87;
            {var subQ0=sQuery(id+"F0.wireOp",EDGE,"E40");var subQ1=sQuery(id+"F0.wireOp",EDGE,"E11");var subQ2=makeQuery(id+"F0.imprint","INTERSECT",VERTEX,{"disambiguationData":[OD(1.0)],"derivedFrom":[subQ1,subQ0]});Q87=makeQuery(id+"F0.imprint","IMPRINT",FACE,{"disambiguationData":[TD([[makeQuery(id+"F0.imprint","IMPRINT",EDGE,{"disambiguationData":[TD([[subQ2,-1.0]])],"derivedFrom":subQ1}),-1.0]])]});}
            var Q88;
            {var subQ0=sQuery(id+"F0.wireOp",EDGE,"E41");var subQ1=sQuery(id+"F0.wireOp",EDGE,"E20");var subQ2=makeQuery(id+"F0.imprint","INTERSECT",VERTEX,{"disambiguationData":[OD(0.0)],"derivedFrom":[subQ1,subQ0]});Q88=makeQuery(id+"F0.imprint","IMPRINT",FACE,{"disambiguationData":[TD([[makeQuery(id+"F0.imprint","IMPRINT",EDGE,{"disambiguationData":[TD([[subQ2,1.0]])],"derivedFrom":subQ1}),-1.0]])]});}
            var Q89;
            {var subQ0=sQuery(id+"F0.wireOp",EDGE,"E40");var subQ1=sQuery(id+"F0.wireOp",EDGE,"E2");var subQ2=makeQuery(id+"F0.imprint","INTERSECT",VERTEX,{"disambiguationData":[OD(1.0)],"derivedFrom":[subQ1,subQ0]});Q89=makeQuery(id+"F0.imprint","IMPRINT",FACE,{"disambiguationData":[TD([[makeQuery(id+"F0.imprint","IMPRINT",EDGE,{"disambiguationData":[TD([[subQ2,-1.0]])],"derivedFrom":subQ1}),-1.0]])]});}
            var Q90;
            {var subQ0=sQuery(id+"F0.wireOp",EDGE,"E41");var subQ1=sQuery(id+"F0.wireOp",EDGE,"E23");var subQ2=makeQuery(id+"F0.imprint","INTERSECT",VERTEX,{"disambiguationData":[OD(0.0)],"derivedFrom":[subQ1,subQ0]});Q90=makeQuery(id+"F0.imprint","IMPRINT",FACE,{"disambiguationData":[TD([[makeQuery(id+"F0.imprint","IMPRINT",EDGE,{"disambiguationData":[TD([[subQ2,1.0]])],"derivedFrom":subQ1}),1.0]])]});}
            var Q91;
            {var subQ0=sQuery(id+"F0.wireOp",EDGE,"E42");var subQ1=sQuery(id+"F0.wireOp",EDGE,"E20");var subQ2=makeQuery(id+"F0.imprint","INTERSECT",VERTEX,{"derivedFrom":[subQ1,subQ0]});Q91=makeQuery(id+"F0.imprint","IMPRINT",FACE,{"disambiguationData":[TD([[makeQuery(id+"F0.imprint","IMPRINT",EDGE,{"disambiguationData":[TD([[subQ2,1.0]])],"derivedFrom":subQ1}),-1.0]])]});}
            var Q92;
            {var subQ0=sQuery(id+"F0.wireOp",EDGE,"E42");var subQ1=sQuery(id+"F0.wireOp",EDGE,"E37");var subQ2=makeQuery(id+"F0.imprint","INTERSECT",VERTEX,{"derivedFrom":[subQ1,subQ0]});Q92=makeQuery(id+"F0.imprint","IMPRINT",FACE,{"disambiguationData":[TD([[makeQuery(id+"F0.imprint","IMPRINT",EDGE,{"disambiguationData":[TD([[subQ2,-1.0]])],"derivedFrom":subQ1}),-1.0]])]});}
            var Q93;
            {var subQ0=sQuery(id+"F0.wireOp",EDGE,"E42");var subQ1=sQuery(id+"F0.wireOp",EDGE,"E26");var subQ2=makeQuery(id+"F0.imprint","INTERSECT",VERTEX,{"derivedFrom":[subQ1,subQ0]});Q93=makeQuery(id+"F0.imprint","IMPRINT",FACE,{"disambiguationData":[TD([[makeQuery(id+"F0.imprint","IMPRINT",EDGE,{"disambiguationData":[TD([[subQ2,1.0]])],"derivedFrom":subQ1}),-1.0]])]});}
            var Q94;
            {var subQ0=sQuery(id+"F0.wireOp",EDGE,"E40");var subQ1=sQuery(id+"F0.wireOp",EDGE,"E28");var subQ2=makeQuery(id+"F0.imprint","INTERSECT",VERTEX,{"disambiguationData":[OD(0.0)],"derivedFrom":[subQ1,subQ0]});Q94=makeQuery(id+"F0.imprint","IMPRINT",FACE,{"disambiguationData":[TD([[makeQuery(id+"F0.imprint","IMPRINT",EDGE,{"disambiguationData":[TD([[subQ2,-1.0]])],"derivedFrom":subQ1}),-1.0]])]});}
            var Q95;
            {var subQ0=sQuery(id+"F0.wireOp",EDGE,"E42");var subQ1=sQuery(id+"F0.wireOp",EDGE,"E2");var subQ2=makeQuery(id+"F0.imprint","INTERSECT",VERTEX,{"derivedFrom":[subQ1,subQ0]});Q95=makeQuery(id+"F0.imprint","IMPRINT",FACE,{"disambiguationData":[TD([[makeQuery(id+"F0.imprint","IMPRINT",EDGE,{"disambiguationData":[TD([[subQ2,-1.0]])],"derivedFrom":subQ1}),-1.0]])]});}
            var Q96;
            {var subQ0=sQuery(id+"F0.wireOp",EDGE,"E41");var subQ1=sQuery(id+"F0.wireOp",EDGE,"E3");var subQ2=makeQuery(id+"F0.imprint","INTERSECT",VERTEX,{"disambiguationData":[OD(0.0)],"derivedFrom":[subQ1,subQ0]});Q96=makeQuery(id+"F0.imprint","IMPRINT",FACE,{"disambiguationData":[TD([[makeQuery(id+"F0.imprint","IMPRINT",EDGE,{"disambiguationData":[TD([[subQ2,1.0]])],"derivedFrom":subQ1}),-1.0]])]});}
            var Q97;
            {var subQ0=sQuery(id+"F0.wireOp",EDGE,"E40");var subQ1=sQuery(id+"F0.wireOp",EDGE,"E5");var subQ2=makeQuery(id+"F0.imprint","INTERSECT",VERTEX,{"disambiguationData":[OD(0.0)],"derivedFrom":[subQ1,subQ0]});Q97=makeQuery(id+"F0.imprint","IMPRINT",FACE,{"disambiguationData":[TD([[makeQuery(id+"F0.imprint","IMPRINT",EDGE,{"disambiguationData":[TD([[subQ2,-1.0]])],"derivedFrom":subQ1}),-1.0]])]});}
            var Q98;
            {var subQ0=sQuery(id+"F0.wireOp",EDGE,"E40");var subQ1=sQuery(id+"F0.wireOp",EDGE,"E13");var subQ2=makeQuery(id+"F0.imprint","INTERSECT",VERTEX,{"disambiguationData":[OD(1.0)],"derivedFrom":[subQ1,subQ0]});Q98=makeQuery(id+"F0.imprint","IMPRINT",FACE,{"disambiguationData":[TD([[makeQuery(id+"F0.imprint","IMPRINT",EDGE,{"disambiguationData":[TD([[subQ2,-1.0]])],"derivedFrom":subQ1}),-1.0]])]});}
            var Q99;
            {var subQ0=sQuery(id+"F0.wireOp",EDGE,"E40");var subQ1=sQuery(id+"F0.wireOp",EDGE,"E8");var subQ2=makeQuery(id+"F0.imprint","INTERSECT",VERTEX,{"disambiguationData":[OD(1.0)],"derivedFrom":[subQ1,subQ0]});Q99=makeQuery(id+"F0.imprint","IMPRINT",FACE,{"disambiguationData":[TD([[makeQuery(id+"F0.imprint","IMPRINT",EDGE,{"disambiguationData":[TD([[subQ2,-1.0]])],"derivedFrom":subQ1}),-1.0]])]});}
            var Q100;
            {var subQ0=sQuery(id+"F0.wireOp",EDGE,"E41");var subQ1=sQuery(id+"F0.wireOp",EDGE,"E30");var subQ2=makeQuery(id+"F0.imprint","INTERSECT",VERTEX,{"disambiguationData":[OD(1.0)],"derivedFrom":[subQ1,subQ0]});Q100=makeQuery(id+"F0.imprint","IMPRINT",FACE,{"disambiguationData":[TD([[makeQuery(id+"F0.imprint","IMPRINT",EDGE,{"disambiguationData":[TD([[subQ2,-1.0]])],"derivedFrom":subQ1}),-1.0]])]});}
            var Q101;
            {var subQ0=sQuery(id+"F0.wireOp",EDGE,"E42");var subQ1=sQuery(id+"F0.wireOp",EDGE,"E8");var subQ2=makeQuery(id+"F0.imprint","INTERSECT",VERTEX,{"derivedFrom":[subQ1,subQ0]});Q101=makeQuery(id+"F0.imprint","IMPRINT",FACE,{"disambiguationData":[TD([[makeQuery(id+"F0.imprint","IMPRINT",EDGE,{"disambiguationData":[TD([[subQ2,-1.0]])],"derivedFrom":subQ1}),-1.0]])]});}
            var Q102;
            {var subQ0=sQuery(id+"F0.wireOp",EDGE,"E42");var subQ1=sQuery(id+"F0.wireOp",EDGE,"E30");var subQ2=makeQuery(id+"F0.imprint","INTERSECT",VERTEX,{"derivedFrom":[subQ1,subQ0]});Q102=makeQuery(id+"F0.imprint","IMPRINT",FACE,{"disambiguationData":[TD([[makeQuery(id+"F0.imprint","IMPRINT",EDGE,{"disambiguationData":[TD([[subQ2,-1.0]])],"derivedFrom":subQ1}),-1.0]])]});}
            var Q103;
            {var subQ0=sQuery(id+"F0.wireOp",EDGE,"E45");var subQ1=sQuery(id+"F0.wireOp",EDGE,"E5");var subQ2=makeQuery(id+"F0.imprint","INTERSECT",VERTEX,{"derivedFrom":[subQ1,subQ0]});Q103=makeQuery(id+"F0.imprint","IMPRINT",FACE,{"disambiguationData":[TD([[makeQuery(id+"F0.imprint","IMPRINT",EDGE,{"disambiguationData":[TD([[subQ2,-1.0]])],"derivedFrom":subQ1}),-1.0]])]});}
            var Q104;
            {var subQ0=sQuery(id+"F0.wireOp",EDGE,"E45");var subQ1=sQuery(id+"F0.wireOp",EDGE,"E7");var subQ2=makeQuery(id+"F0.imprint","INTERSECT",VERTEX,{"derivedFrom":[subQ1,subQ0]});Q104=makeQuery(id+"F0.imprint","IMPRINT",FACE,{"disambiguationData":[TD([[makeQuery(id+"F0.imprint","IMPRINT",EDGE,{"disambiguationData":[TD([[subQ2,-1.0]])],"derivedFrom":subQ1}),-1.0]])]});}
            var Q105;
            {var subQ0=sQuery(id+"F0.wireOp",EDGE,"E41");var subQ1=sQuery(id+"F0.wireOp",EDGE,"E8");var subQ2=makeQuery(id+"F0.imprint","INTERSECT",VERTEX,{"disambiguationData":[OD(1.0)],"derivedFrom":[subQ1,subQ0]});Q105=makeQuery(id+"F0.imprint","IMPRINT",FACE,{"disambiguationData":[TD([[makeQuery(id+"F0.imprint","IMPRINT",EDGE,{"disambiguationData":[TD([[subQ2,-1.0]])],"derivedFrom":subQ1}),-1.0]])]});}
            var Q106;
            {var subQ0=sQuery(id+"F0.wireOp",EDGE,"E42");var subQ1=sQuery(id+"F0.wireOp",EDGE,"E4");var subQ2=makeQuery(id+"F0.imprint","INTERSECT",VERTEX,{"derivedFrom":[subQ1,subQ0]});Q106=makeQuery(id+"F0.imprint","IMPRINT",FACE,{"disambiguationData":[TD([[makeQuery(id+"F0.imprint","IMPRINT",EDGE,{"disambiguationData":[TD([[subQ2,1.0]])],"derivedFrom":subQ1}),1.0]])]});}
            var Q107;
            {var subQ0=sQuery(id+"F0.wireOp",EDGE,"E41");var subQ1=sQuery(id+"F0.wireOp",EDGE,"E29");var subQ2=makeQuery(id+"F0.imprint","INTERSECT",VERTEX,{"disambiguationData":[OD(1.0)],"derivedFrom":[subQ1,subQ0]});Q107=makeQuery(id+"F0.imprint","IMPRINT",FACE,{"disambiguationData":[TD([[makeQuery(id+"F0.imprint","IMPRINT",EDGE,{"disambiguationData":[TD([[subQ2,-1.0]])],"derivedFrom":subQ1}),-1.0]])]});}
            var Q108;
            {var subQ0=sQuery(id+"F0.wireOp",EDGE,"E40");var subQ1=sQuery(id+"F0.wireOp",EDGE,"E38");var subQ2=makeQuery(id+"F0.imprint","INTERSECT",VERTEX,{"disambiguationData":[OD(0.0)],"derivedFrom":[subQ1,subQ0]});Q108=makeQuery(id+"F0.imprint","IMPRINT",FACE,{"disambiguationData":[TD([[makeQuery(id+"F0.imprint","IMPRINT",EDGE,{"disambiguationData":[TD([[subQ2,-1.0]])],"derivedFrom":subQ1}),-1.0]])]});}
            var Q109;
            {var subQ0=sQuery(id+"F0.wireOp",EDGE,"E42");var subQ1=sQuery(id+"F0.wireOp",EDGE,"E27");var subQ2=makeQuery(id+"F0.imprint","INTERSECT",VERTEX,{"derivedFrom":[subQ1,subQ0]});Q109=makeQuery(id+"F0.imprint","IMPRINT",FACE,{"disambiguationData":[TD([[makeQuery(id+"F0.imprint","IMPRINT",EDGE,{"disambiguationData":[TD([[subQ2,-1.0]])],"derivedFrom":subQ1}),-1.0]])]});}
            var Q110;
            {var subQ0=sQuery(id+"F0.wireOp",EDGE,"E41");var subQ1=sQuery(id+"F0.wireOp",EDGE,"E5");var subQ2=makeQuery(id+"F0.imprint","INTERSECT",VERTEX,{"disambiguationData":[OD(0.0)],"derivedFrom":[subQ1,subQ0]});Q110=makeQuery(id+"F0.imprint","IMPRINT",FACE,{"disambiguationData":[TD([[makeQuery(id+"F0.imprint","IMPRINT",EDGE,{"disambiguationData":[TD([[subQ2,1.0]])],"derivedFrom":subQ1}),-1.0]])]});}
            var Q111;
            {var subQ0=sQuery(id+"F0.wireOp",EDGE,"E45");var subQ1=sQuery(id+"F0.wireOp",EDGE,"E32");var subQ2=makeQuery(id+"F0.imprint","INTERSECT",VERTEX,{"derivedFrom":[subQ1,subQ0]});Q111=makeQuery(id+"F0.imprint","IMPRINT",FACE,{"disambiguationData":[TD([[makeQuery(id+"F0.imprint","IMPRINT",EDGE,{"disambiguationData":[TD([[subQ2,-1.0]])],"derivedFrom":subQ1}),-1.0]])]});}
            var Q112;
            {var subQ0=sQuery(id+"F0.wireOp",EDGE,"E40");var subQ1=sQuery(id+"F0.wireOp",EDGE,"E32");var subQ2=makeQuery(id+"F0.imprint","INTERSECT",VERTEX,{"disambiguationData":[OD(0.0)],"derivedFrom":[subQ1,subQ0]});Q112=makeQuery(id+"F0.imprint","IMPRINT",FACE,{"disambiguationData":[TD([[makeQuery(id+"F0.imprint","IMPRINT",EDGE,{"disambiguationData":[TD([[subQ2,-1.0]])],"derivedFrom":subQ1}),-1.0]])]});}
            var Q113;
            {var subQ0=sQuery(id+"F0.wireOp",EDGE,"E40");var subQ1=sQuery(id+"F0.wireOp",EDGE,"E19");var subQ2=makeQuery(id+"F0.imprint","INTERSECT",VERTEX,{"disambiguationData":[OD(1.0)],"derivedFrom":[subQ1,subQ0]});Q113=makeQuery(id+"F0.imprint","IMPRINT",FACE,{"disambiguationData":[TD([[makeQuery(id+"F0.imprint","IMPRINT",EDGE,{"disambiguationData":[TD([[subQ2,-1.0]])],"derivedFrom":subQ1}),-1.0]])]});}
            var Q114;
            {var subQ0=sQuery(id+"F0.wireOp",EDGE,"E40");var subQ1=sQuery(id+"F0.wireOp",EDGE,"E10");var subQ2=makeQuery(id+"F0.imprint","INTERSECT",VERTEX,{"disambiguationData":[OD(0.0)],"derivedFrom":[subQ1,subQ0]});Q114=makeQuery(id+"F0.imprint","IMPRINT",FACE,{"disambiguationData":[TD([[makeQuery(id+"F0.imprint","IMPRINT",EDGE,{"disambiguationData":[TD([[subQ2,-1.0]])],"derivedFrom":subQ1}),-1.0]])]});}
            var Q115;
            {var subQ0=sQuery(id+"F0.wireOp",EDGE,"E41");var subQ1=sQuery(id+"F0.wireOp",EDGE,"E8");var subQ2=makeQuery(id+"F0.imprint","INTERSECT",VERTEX,{"disambiguationData":[OD(0.0)],"derivedFrom":[subQ1,subQ0]});Q115=makeQuery(id+"F0.imprint","IMPRINT",FACE,{"disambiguationData":[TD([[makeQuery(id+"F0.imprint","IMPRINT",EDGE,{"disambiguationData":[TD([[subQ2,1.0]])],"derivedFrom":subQ1}),-1.0]])]});}
            var Q116;
            {var subQ0=sQuery(id+"F0.wireOp",EDGE,"E42");var subQ1=sQuery(id+"F0.wireOp",EDGE,"E17");var subQ2=makeQuery(id+"F0.imprint","INTERSECT",VERTEX,{"derivedFrom":[subQ1,subQ0]});Q116=makeQuery(id+"F0.imprint","IMPRINT",FACE,{"disambiguationData":[TD([[makeQuery(id+"F0.imprint","IMPRINT",EDGE,{"disambiguationData":[TD([[subQ2,-1.0]])],"derivedFrom":subQ1}),1.0]])]});}
            var Q117;
            {var subQ0=sQuery(id+"F0.wireOp",EDGE,"E45");var subQ1=sQuery(id+"F0.wireOp",EDGE,"E2");var subQ2=makeQuery(id+"F0.imprint","INTERSECT",VERTEX,{"derivedFrom":[subQ1,subQ0]});Q117=makeQuery(id+"F0.imprint","IMPRINT",FACE,{"disambiguationData":[TD([[makeQuery(id+"F0.imprint","IMPRINT",EDGE,{"disambiguationData":[TD([[subQ2,-1.0]])],"derivedFrom":subQ1}),-1.0]])]});}
            var Q118;
            {var subQ0=sQuery(id+"F0.wireOp",EDGE,"E40");var subQ1=sQuery(id+"F0.wireOp",EDGE,"E16");var subQ2=makeQuery(id+"F0.imprint","INTERSECT",VERTEX,{"disambiguationData":[OD(1.0)],"derivedFrom":[subQ1,subQ0]});Q118=makeQuery(id+"F0.imprint","IMPRINT",FACE,{"disambiguationData":[TD([[makeQuery(id+"F0.imprint","IMPRINT",EDGE,{"disambiguationData":[TD([[subQ2,-1.0]])],"derivedFrom":subQ1}),-1.0]])]});}
            var Q119;
            {var subQ0=sQuery(id+"F0.wireOp",EDGE,"E40");var subQ1=sQuery(id+"F0.wireOp",EDGE,"E28");var subQ2=makeQuery(id+"F0.imprint","INTERSECT",VERTEX,{"disambiguationData":[OD(1.0)],"derivedFrom":[subQ1,subQ0]});Q119=makeQuery(id+"F0.imprint","IMPRINT",FACE,{"disambiguationData":[TD([[makeQuery(id+"F0.imprint","IMPRINT",EDGE,{"disambiguationData":[TD([[subQ2,-1.0]])],"derivedFrom":subQ1}),-1.0]])]});}
            var Q120;
            {var subQ0=sQuery(id+"F0.wireOp",EDGE,"E42");var subQ1=sQuery(id+"F0.wireOp",EDGE,"E29");var subQ2=makeQuery(id+"F0.imprint","INTERSECT",VERTEX,{"derivedFrom":[subQ1,subQ0]});Q120=makeQuery(id+"F0.imprint","IMPRINT",FACE,{"disambiguationData":[TD([[makeQuery(id+"F0.imprint","IMPRINT",EDGE,{"disambiguationData":[TD([[subQ2,1.0]])],"derivedFrom":subQ1}),-1.0]])]});}
            var Q121;
            {var subQ0=sQuery(id+"F0.wireOp",EDGE,"E42");var subQ1=sQuery(id+"F0.wireOp",EDGE,"E5");var subQ2=makeQuery(id+"F0.imprint","INTERSECT",VERTEX,{"derivedFrom":[subQ1,subQ0]});Q121=makeQuery(id+"F0.imprint","IMPRINT",FACE,{"disambiguationData":[TD([[makeQuery(id+"F0.imprint","IMPRINT",EDGE,{"disambiguationData":[TD([[subQ2,-1.0]])],"derivedFrom":subQ1}),-1.0]])]});}
            var Q122;
            {var subQ0=sQuery(id+"F0.wireOp",EDGE,"E45");var subQ1=sQuery(id+"F0.wireOp",EDGE,"E15");var subQ2=makeQuery(id+"F0.imprint","INTERSECT",VERTEX,{"derivedFrom":[subQ1,subQ0]});Q122=makeQuery(id+"F0.imprint","IMPRINT",FACE,{"disambiguationData":[TD([[makeQuery(id+"F0.imprint","IMPRINT",EDGE,{"disambiguationData":[TD([[subQ2,-1.0]])],"derivedFrom":subQ1}),-1.0]])]});}
            var Q123;
            {var subQ0=sQuery(id+"F0.wireOp",EDGE,"E40");var subQ1=sQuery(id+"F0.wireOp",EDGE,"E29");var subQ2=makeQuery(id+"F0.imprint","INTERSECT",VERTEX,{"disambiguationData":[OD(0.0)],"derivedFrom":[subQ1,subQ0]});Q123=makeQuery(id+"F0.imprint","IMPRINT",FACE,{"disambiguationData":[TD([[makeQuery(id+"F0.imprint","IMPRINT",EDGE,{"disambiguationData":[TD([[subQ2,-1.0]])],"derivedFrom":subQ1}),-1.0]])]});}
            var Q124;
            {var subQ0=sQuery(id+"F0.wireOp",EDGE,"E41");var subQ1=sQuery(id+"F0.wireOp",EDGE,"E2");var subQ2=makeQuery(id+"F0.imprint","INTERSECT",VERTEX,{"disambiguationData":[OD(0.0)],"derivedFrom":[subQ1,subQ0]});Q124=makeQuery(id+"F0.imprint","IMPRINT",FACE,{"disambiguationData":[TD([[makeQuery(id+"F0.imprint","IMPRINT",EDGE,{"disambiguationData":[TD([[subQ2,1.0]])],"derivedFrom":subQ1}),-1.0]])]});}
            var Q125;
            {var subQ0=sQuery(id+"F0.wireOp",EDGE,"E41");var subQ1=sQuery(id+"F0.wireOp",EDGE,"E15");var subQ2=makeQuery(id+"F0.imprint","INTERSECT",VERTEX,{"disambiguationData":[OD(0.0)],"derivedFrom":[subQ1,subQ0]});Q125=makeQuery(id+"F0.imprint","IMPRINT",FACE,{"disambiguationData":[TD([[makeQuery(id+"F0.imprint","IMPRINT",EDGE,{"disambiguationData":[TD([[subQ2,1.0]])],"derivedFrom":subQ1}),-1.0]])]});}
            var Q126;
            {var subQ0=sQuery(id+"F0.wireOp",EDGE,"E40");var subQ1=sQuery(id+"F0.wireOp",EDGE,"E7");var subQ2=makeQuery(id+"F0.imprint","INTERSECT",VERTEX,{"disambiguationData":[OD(0.0)],"derivedFrom":[subQ1,subQ0]});Q126=makeQuery(id+"F0.imprint","IMPRINT",FACE,{"disambiguationData":[TD([[makeQuery(id+"F0.imprint","IMPRINT",EDGE,{"disambiguationData":[TD([[subQ2,-1.0]])],"derivedFrom":subQ1}),-1.0]])]});}
            var Q127;
            {var subQ0=sQuery(id+"F0.wireOp",EDGE,"E41");var subQ1=sQuery(id+"F0.wireOp",EDGE,"E0");var subQ2=makeQuery(id+"F0.imprint","INTERSECT",VERTEX,{"disambiguationData":[OD(1.0)],"derivedFrom":[subQ1,subQ0]});Q127=makeQuery(id+"F0.imprint","IMPRINT",FACE,{"disambiguationData":[TD([[makeQuery(id+"F0.imprint","IMPRINT",EDGE,{"disambiguationData":[TD([[subQ2,1.0]])],"derivedFrom":subQ1}),1.0]])]});}
            var Q128;
            {var subQ0=sQuery(id+"F0.wireOp",EDGE,"E42");var subQ1=sQuery(id+"F0.wireOp",EDGE,"E30");var subQ2=makeQuery(id+"F0.imprint","INTERSECT",VERTEX,{"derivedFrom":[subQ1,subQ0]});Q128=makeQuery(id+"F0.imprint","IMPRINT",FACE,{"disambiguationData":[TD([[makeQuery(id+"F0.imprint","IMPRINT",EDGE,{"disambiguationData":[TD([[subQ2,1.0]])],"derivedFrom":subQ1}),-1.0]])]});}
            var Q129;
            {var subQ0=sQuery(id+"F0.wireOp",EDGE,"E45");var subQ1=sQuery(id+"F0.wireOp",EDGE,"E30");var subQ2=makeQuery(id+"F0.imprint","INTERSECT",VERTEX,{"derivedFrom":[subQ1,subQ0]});Q129=makeQuery(id+"F0.imprint","IMPRINT",FACE,{"disambiguationData":[TD([[makeQuery(id+"F0.imprint","IMPRINT",EDGE,{"disambiguationData":[TD([[subQ2,-1.0]])],"derivedFrom":subQ1}),-1.0]])]});}
            var Q130;
            {var subQ0=sQuery(id+"F0.wireOp",EDGE,"E42");var subQ1=sQuery(id+"F0.wireOp",EDGE,"E23");var subQ2=makeQuery(id+"F0.imprint","INTERSECT",VERTEX,{"derivedFrom":[subQ1,subQ0]});Q130=makeQuery(id+"F0.imprint","IMPRINT",FACE,{"disambiguationData":[TD([[makeQuery(id+"F0.imprint","IMPRINT",EDGE,{"disambiguationData":[TD([[subQ2,-1.0]])],"derivedFrom":subQ1}),-1.0]])]});}
            var Q131;
            {var subQ0=sQuery(id+"F0.wireOp",EDGE,"E42");var subQ1=sQuery(id+"F0.wireOp",EDGE,"E17");var subQ2=makeQuery(id+"F0.imprint","INTERSECT",VERTEX,{"derivedFrom":[subQ1,subQ0]});Q131=makeQuery(id+"F0.imprint","IMPRINT",FACE,{"disambiguationData":[TD([[makeQuery(id+"F0.imprint","IMPRINT",EDGE,{"disambiguationData":[TD([[subQ2,1.0]])],"derivedFrom":subQ1}),1.0]])]});}
            var Q132;
            {var subQ0=sQuery(id+"F0.wireOp",EDGE,"E40");var subQ1=sQuery(id+"F0.wireOp",EDGE,"E3");var subQ2=makeQuery(id+"F0.imprint","INTERSECT",VERTEX,{"disambiguationData":[OD(0.0)],"derivedFrom":[subQ1,subQ0]});Q132=makeQuery(id+"F0.imprint","IMPRINT",FACE,{"disambiguationData":[TD([[makeQuery(id+"F0.imprint","IMPRINT",EDGE,{"disambiguationData":[TD([[subQ2,-1.0]])],"derivedFrom":subQ1}),-1.0]])]});}
            var Q133;
            {var subQ0=sQuery(id+"F0.wireOp",EDGE,"E41");var subQ1=sQuery(id+"F0.wireOp",EDGE,"E26");var subQ2=makeQuery(id+"F0.imprint","INTERSECT",VERTEX,{"disambiguationData":[OD(0.0)],"derivedFrom":[subQ1,subQ0]});Q133=makeQuery(id+"F0.imprint","IMPRINT",FACE,{"disambiguationData":[TD([[makeQuery(id+"F0.imprint","IMPRINT",EDGE,{"disambiguationData":[TD([[subQ2,1.0]])],"derivedFrom":subQ1}),-1.0]])]});}
            var Q134;
            {var subQ0=sQuery(id+"F0.wireOp",EDGE,"E41");var subQ1=sQuery(id+"F0.wireOp",EDGE,"E32");var subQ2=makeQuery(id+"F0.imprint","INTERSECT",VERTEX,{"disambiguationData":[OD(1.0)],"derivedFrom":[subQ1,subQ0]});Q134=makeQuery(id+"F0.imprint","IMPRINT",FACE,{"disambiguationData":[TD([[makeQuery(id+"F0.imprint","IMPRINT",EDGE,{"disambiguationData":[TD([[subQ2,-1.0]])],"derivedFrom":subQ1}),-1.0]])]});}
            var Q135;
            {var subQ0=sQuery(id+"F0.wireOp",EDGE,"E41");var subQ1=sQuery(id+"F0.wireOp",EDGE,"E23");var subQ2=makeQuery(id+"F0.imprint","INTERSECT",VERTEX,{"disambiguationData":[OD(1.0)],"derivedFrom":[subQ1,subQ0]});Q135=makeQuery(id+"F0.imprint","IMPRINT",FACE,{"disambiguationData":[TD([[makeQuery(id+"F0.imprint","IMPRINT",EDGE,{"disambiguationData":[TD([[subQ2,-1.0]])],"derivedFrom":subQ1}),-1.0]])]});}
            var Q136;
            {var subQ0=sQuery(id+"F0.wireOp",EDGE,"E41");var subQ1=sQuery(id+"F0.wireOp",EDGE,"E33");var subQ2=makeQuery(id+"F0.imprint","INTERSECT",VERTEX,{"disambiguationData":[OD(1.0)],"derivedFrom":[subQ1,subQ0]});Q136=makeQuery(id+"F0.imprint","IMPRINT",FACE,{"disambiguationData":[TD([[makeQuery(id+"F0.imprint","IMPRINT",EDGE,{"disambiguationData":[TD([[subQ2,-1.0]])],"derivedFrom":subQ1}),-1.0]])]});}
            var Q137;
            {var subQ0=sQuery(id+"F0.wireOp",EDGE,"E41");var subQ1=sQuery(id+"F0.wireOp",EDGE,"E13");var subQ2=makeQuery(id+"F0.imprint","INTERSECT",VERTEX,{"disambiguationData":[OD(1.0)],"derivedFrom":[subQ1,subQ0]});Q137=makeQuery(id+"F0.imprint","IMPRINT",FACE,{"disambiguationData":[TD([[makeQuery(id+"F0.imprint","IMPRINT",EDGE,{"disambiguationData":[TD([[subQ2,-1.0]])],"derivedFrom":subQ1}),-1.0]])]});}
            var Q138;
            {var subQ0=sQuery(id+"F0.wireOp",EDGE,"E41");var subQ1=sQuery(id+"F0.wireOp",EDGE,"E18");var subQ2=makeQuery(id+"F0.imprint","INTERSECT",VERTEX,{"disambiguationData":[OD(0.0)],"derivedFrom":[subQ1,subQ0]});Q138=makeQuery(id+"F0.imprint","IMPRINT",FACE,{"disambiguationData":[TD([[makeQuery(id+"F0.imprint","IMPRINT",EDGE,{"disambiguationData":[TD([[subQ2,1.0]])],"derivedFrom":subQ1}),1.0]])]});}
            var Q139;
            {var subQ0=sQuery(id+"F0.wireOp",EDGE,"E40");var subQ1=sQuery(id+"F0.wireOp",EDGE,"E16");var subQ2=makeQuery(id+"F0.imprint","INTERSECT",VERTEX,{"disambiguationData":[OD(0.0)],"derivedFrom":[subQ1,subQ0]});Q139=makeQuery(id+"F0.imprint","IMPRINT",FACE,{"disambiguationData":[TD([[makeQuery(id+"F0.imprint","IMPRINT",EDGE,{"disambiguationData":[TD([[subQ2,-1.0]])],"derivedFrom":subQ1}),-1.0]])]});}
            var Q140;
            {var subQ0=sQuery(id+"F0.wireOp",EDGE,"E42");var subQ1=sQuery(id+"F0.wireOp",EDGE,"E13");var subQ2=makeQuery(id+"F0.imprint","INTERSECT",VERTEX,{"derivedFrom":[subQ1,subQ0]});Q140=makeQuery(id+"F0.imprint","IMPRINT",FACE,{"disambiguationData":[TD([[makeQuery(id+"F0.imprint","IMPRINT",EDGE,{"disambiguationData":[TD([[subQ2,1.0]])],"derivedFrom":subQ1}),-1.0]])]});}
            var Q141;
            {var subQ0=sQuery(id+"F0.wireOp",EDGE,"E41");var subQ1=sQuery(id+"F0.wireOp",EDGE,"E16");var subQ2=makeQuery(id+"F0.imprint","INTERSECT",VERTEX,{"disambiguationData":[OD(1.0)],"derivedFrom":[subQ1,subQ0]});Q141=makeQuery(id+"F0.imprint","IMPRINT",FACE,{"disambiguationData":[TD([[makeQuery(id+"F0.imprint","IMPRINT",EDGE,{"disambiguationData":[TD([[subQ2,-1.0]])],"derivedFrom":subQ1}),-1.0]])]});}
            var Q142;
            {var subQ0=sQuery(id+"F0.wireOp",EDGE,"E40");var subQ1=sQuery(id+"F0.wireOp",EDGE,"E34");var subQ2=makeQuery(id+"F0.imprint","INTERSECT",VERTEX,{"disambiguationData":[OD(0.0)],"derivedFrom":[subQ1,subQ0]});Q142=makeQuery(id+"F0.imprint","IMPRINT",FACE,{"disambiguationData":[TD([[makeQuery(id+"F0.imprint","IMPRINT",EDGE,{"disambiguationData":[TD([[subQ2,-1.0]])],"derivedFrom":subQ1}),-1.0]])]});}
            var Q143;
            {var subQ0=sQuery(id+"F0.wireOp",EDGE,"E40");var subQ1=sQuery(id+"F0.wireOp",EDGE,"E35");var subQ2=makeQuery(id+"F0.imprint","INTERSECT",VERTEX,{"disambiguationData":[OD(0.0)],"derivedFrom":[subQ1,subQ0]});Q143=makeQuery(id+"F0.imprint","IMPRINT",FACE,{"disambiguationData":[TD([[makeQuery(id+"F0.imprint","IMPRINT",EDGE,{"disambiguationData":[TD([[subQ2,-1.0]])],"derivedFrom":subQ1}),-1.0]])]});}
            var Q144;
            {var subQ0=sQuery(id+"F0.wireOp",EDGE,"E45");var subQ1=sQuery(id+"F0.wireOp",EDGE,"E37");var subQ2=makeQuery(id+"F0.imprint","INTERSECT",VERTEX,{"derivedFrom":[subQ1,subQ0]});Q144=makeQuery(id+"F0.imprint","IMPRINT",FACE,{"disambiguationData":[TD([[makeQuery(id+"F0.imprint","IMPRINT",EDGE,{"disambiguationData":[TD([[subQ2,-1.0]])],"derivedFrom":subQ1}),-1.0]])]});}
            var Q145;
            {var subQ0=sQuery(id+"F0.wireOp",EDGE,"E40");var subQ1=sQuery(id+"F0.wireOp",EDGE,"E11");var subQ2=makeQuery(id+"F0.imprint","INTERSECT",VERTEX,{"disambiguationData":[OD(0.0)],"derivedFrom":[subQ1,subQ0]});Q145=makeQuery(id+"F0.imprint","IMPRINT",FACE,{"disambiguationData":[TD([[makeQuery(id+"F0.imprint","IMPRINT",EDGE,{"disambiguationData":[TD([[subQ2,-1.0]])],"derivedFrom":subQ1}),-1.0]])]});}
            var Q146;
            {var subQ0=sQuery(id+"F0.wireOp",EDGE,"E40");var subQ1=sQuery(id+"F0.wireOp",EDGE,"E30");var subQ2=makeQuery(id+"F0.imprint","INTERSECT",VERTEX,{"disambiguationData":[OD(1.0)],"derivedFrom":[subQ1,subQ0]});Q146=makeQuery(id+"F0.imprint","IMPRINT",FACE,{"disambiguationData":[TD([[makeQuery(id+"F0.imprint","IMPRINT",EDGE,{"disambiguationData":[TD([[subQ2,-1.0]])],"derivedFrom":subQ1}),-1.0]])]});}
            var Q147;
            {var subQ0=sQuery(id+"F0.wireOp",EDGE,"E41");var subQ1=sQuery(id+"F0.wireOp",EDGE,"E3");var subQ2=makeQuery(id+"F0.imprint","INTERSECT",VERTEX,{"disambiguationData":[OD(1.0)],"derivedFrom":[subQ1,subQ0]});Q147=makeQuery(id+"F0.imprint","IMPRINT",FACE,{"disambiguationData":[TD([[makeQuery(id+"F0.imprint","IMPRINT",EDGE,{"disambiguationData":[TD([[subQ2,-1.0]])],"derivedFrom":subQ1}),-1.0]])]});}
            var Q148;
            {var subQ0=sQuery(id+"F0.wireOp",EDGE,"E42");var subQ1=sQuery(id+"F0.wireOp",EDGE,"E9");var subQ2=makeQuery(id+"F0.imprint","INTERSECT",VERTEX,{"derivedFrom":[subQ1,subQ0]});Q148=makeQuery(id+"F0.imprint","IMPRINT",FACE,{"disambiguationData":[TD([[makeQuery(id+"F0.imprint","IMPRINT",EDGE,{"disambiguationData":[TD([[subQ2,-1.0]])],"derivedFrom":subQ1}),-1.0]])]});}
            var Q149;
            {var subQ0=sQuery(id+"F0.wireOp",EDGE,"E42");var subQ1=sQuery(id+"F0.wireOp",EDGE,"E4");var subQ2=makeQuery(id+"F0.imprint","INTERSECT",VERTEX,{"derivedFrom":[subQ1,subQ0]});Q149=makeQuery(id+"F0.imprint","IMPRINT",FACE,{"disambiguationData":[TD([[makeQuery(id+"F0.imprint","IMPRINT",EDGE,{"disambiguationData":[TD([[subQ2,1.0]])],"derivedFrom":subQ1}),-1.0]])]});}
            var Q150;
            {var subQ0=sQuery(id+"F0.wireOp",EDGE,"E40");var subQ1=sQuery(id+"F0.wireOp",EDGE,"E23");var subQ2=makeQuery(id+"F0.imprint","INTERSECT",VERTEX,{"disambiguationData":[OD(1.0)],"derivedFrom":[subQ1,subQ0]});Q150=makeQuery(id+"F0.imprint","IMPRINT",FACE,{"disambiguationData":[TD([[makeQuery(id+"F0.imprint","IMPRINT",EDGE,{"disambiguationData":[TD([[subQ2,-1.0]])],"derivedFrom":subQ1}),1.0]])]});}
            var Q151;
            {var subQ0=sQuery(id+"F0.wireOp",EDGE,"E41");var subQ1=sQuery(id+"F0.wireOp",EDGE,"E9");var subQ2=makeQuery(id+"F0.imprint","INTERSECT",VERTEX,{"disambiguationData":[OD(1.0)],"derivedFrom":[subQ1,subQ0]});Q151=makeQuery(id+"F0.imprint","IMPRINT",FACE,{"disambiguationData":[TD([[makeQuery(id+"F0.imprint","IMPRINT",EDGE,{"disambiguationData":[TD([[subQ2,-1.0]])],"derivedFrom":subQ1}),-1.0]])]});}
            var Q152;
            {var subQ0=sQuery(id+"F0.wireOp",EDGE,"E42");var subQ1=sQuery(id+"F0.wireOp",EDGE,"E34");var subQ2=makeQuery(id+"F0.imprint","INTERSECT",VERTEX,{"derivedFrom":[subQ1,subQ0]});Q152=makeQuery(id+"F0.imprint","IMPRINT",FACE,{"disambiguationData":[TD([[makeQuery(id+"F0.imprint","IMPRINT",EDGE,{"disambiguationData":[TD([[subQ2,-1.0]])],"derivedFrom":subQ1}),-1.0]])]});}
            var Q153;
            {var subQ0=sQuery(id+"F0.wireOp",EDGE,"E45");var subQ1=sQuery(id+"F0.wireOp",EDGE,"E10");var subQ2=makeQuery(id+"F0.imprint","INTERSECT",VERTEX,{"derivedFrom":[subQ1,subQ0]});Q153=makeQuery(id+"F0.imprint","IMPRINT",FACE,{"disambiguationData":[TD([[makeQuery(id+"F0.imprint","IMPRINT",EDGE,{"disambiguationData":[TD([[subQ2,-1.0]])],"derivedFrom":subQ1}),-1.0]])]});}
            var Q154;
            {var subQ0=sQuery(id+"F0.wireOp",EDGE,"E40");var subQ1=sQuery(id+"F0.wireOp",EDGE,"E4");var subQ2=makeQuery(id+"F0.imprint","INTERSECT",VERTEX,{"disambiguationData":[OD(0.0)],"derivedFrom":[subQ1,subQ0]});Q154=makeQuery(id+"F0.imprint","IMPRINT",FACE,{"disambiguationData":[TD([[makeQuery(id+"F0.imprint","IMPRINT",EDGE,{"disambiguationData":[TD([[subQ2,-1.0]])],"derivedFrom":subQ1}),1.0]])]});}
            var Q155;
            {var subQ0=sQuery(id+"F0.wireOp",EDGE,"E42");var subQ1=sQuery(id+"F0.wireOp",EDGE,"E11");var subQ2=makeQuery(id+"F0.imprint","INTERSECT",VERTEX,{"derivedFrom":[subQ1,subQ0]});Q155=makeQuery(id+"F0.imprint","IMPRINT",FACE,{"disambiguationData":[TD([[makeQuery(id+"F0.imprint","IMPRINT",EDGE,{"disambiguationData":[TD([[subQ2,-1.0]])],"derivedFrom":subQ1}),-1.0]])]});}
            var Q156;
            {var subQ0=sQuery(id+"F0.wireOp",EDGE,"E45");var subQ1=sQuery(id+"F0.wireOp",EDGE,"E23");var subQ2=makeQuery(id+"F0.imprint","INTERSECT",VERTEX,{"derivedFrom":[subQ1,subQ0]});Q156=makeQuery(id+"F0.imprint","IMPRINT",FACE,{"disambiguationData":[TD([[makeQuery(id+"F0.imprint","IMPRINT",EDGE,{"disambiguationData":[TD([[subQ2,-1.0]])],"derivedFrom":subQ1}),1.0]])]});}
            var Q157;
            {var subQ0=sQuery(id+"F0.wireOp",EDGE,"E45");var subQ1=sQuery(id+"F0.wireOp",EDGE,"E16");var subQ2=makeQuery(id+"F0.imprint","INTERSECT",VERTEX,{"derivedFrom":[subQ1,subQ0]});Q157=makeQuery(id+"F0.imprint","IMPRINT",FACE,{"disambiguationData":[TD([[makeQuery(id+"F0.imprint","IMPRINT",EDGE,{"disambiguationData":[TD([[subQ2,-1.0]])],"derivedFrom":subQ1}),-1.0]])]});}
            var Q158;
            {var subQ0=sQuery(id+"F0.wireOp",EDGE,"E40");var subQ1=sQuery(id+"F0.wireOp",EDGE,"E17");var subQ2=makeQuery(id+"F0.imprint","INTERSECT",VERTEX,{"disambiguationData":[OD(1.0)],"derivedFrom":[subQ1,subQ0]});Q158=makeQuery(id+"F0.imprint","IMPRINT",FACE,{"disambiguationData":[TD([[makeQuery(id+"F0.imprint","IMPRINT",EDGE,{"disambiguationData":[TD([[subQ2,-1.0]])],"derivedFrom":subQ1}),-1.0]])]});}
            var Q159;
            {var subQ0=sQuery(id+"F0.wireOp",EDGE,"E42");var subQ1=sQuery(id+"F0.wireOp",EDGE,"E19");var subQ2=makeQuery(id+"F0.imprint","INTERSECT",VERTEX,{"derivedFrom":[subQ1,subQ0]});Q159=makeQuery(id+"F0.imprint","IMPRINT",FACE,{"disambiguationData":[TD([[makeQuery(id+"F0.imprint","IMPRINT",EDGE,{"disambiguationData":[TD([[subQ2,1.0]])],"derivedFrom":subQ1}),-1.0]])]});}
            var Q160;
            {var subQ0=sQuery(id+"F0.wireOp",EDGE,"E41");var subQ1=sQuery(id+"F0.wireOp",EDGE,"E23");var subQ2=makeQuery(id+"F0.imprint","INTERSECT",VERTEX,{"disambiguationData":[OD(0.0)],"derivedFrom":[subQ1,subQ0]});Q160=makeQuery(id+"F0.imprint","IMPRINT",FACE,{"disambiguationData":[TD([[makeQuery(id+"F0.imprint","IMPRINT",EDGE,{"disambiguationData":[TD([[subQ2,1.0]])],"derivedFrom":subQ1}),-1.0]])]});}
            var Q161;
            {var subQ0=sQuery(id+"F0.wireOp",EDGE,"E40");var subQ1=sQuery(id+"F0.wireOp",EDGE,"E12");var subQ2=makeQuery(id+"F0.imprint","INTERSECT",VERTEX,{"disambiguationData":[OD(0.0)],"derivedFrom":[subQ1,subQ0]});Q161=makeQuery(id+"F0.imprint","IMPRINT",FACE,{"disambiguationData":[TD([[makeQuery(id+"F0.imprint","IMPRINT",EDGE,{"disambiguationData":[TD([[subQ2,-1.0]])],"derivedFrom":subQ1}),-1.0]])]});}
            var Q162;
            {var subQ0=sQuery(id+"F0.wireOp",EDGE,"E41");var subQ1=sQuery(id+"F0.wireOp",EDGE,"E25");var subQ2=makeQuery(id+"F0.imprint","INTERSECT",VERTEX,{"disambiguationData":[OD(0.0)],"derivedFrom":[subQ1,subQ0]});Q162=makeQuery(id+"F0.imprint","IMPRINT",FACE,{"disambiguationData":[TD([[makeQuery(id+"F0.imprint","IMPRINT",EDGE,{"disambiguationData":[TD([[subQ2,1.0]])],"derivedFrom":subQ1}),-1.0]])]});}
            var Q163;
            {var subQ0=sQuery(id+"F0.wireOp",EDGE,"E45");var subQ1=sQuery(id+"F0.wireOp",EDGE,"E35");var subQ2=makeQuery(id+"F0.imprint","INTERSECT",VERTEX,{"derivedFrom":[subQ1,subQ0]});Q163=makeQuery(id+"F0.imprint","IMPRINT",FACE,{"disambiguationData":[TD([[makeQuery(id+"F0.imprint","IMPRINT",EDGE,{"disambiguationData":[TD([[subQ2,-1.0]])],"derivedFrom":subQ1}),-1.0]])]});}
            var Q164;
            {var subQ0=sQuery(id+"F0.wireOp",EDGE,"E42");var subQ1=sQuery(id+"F0.wireOp",EDGE,"E19");var subQ2=makeQuery(id+"F0.imprint","INTERSECT",VERTEX,{"derivedFrom":[subQ1,subQ0]});Q164=makeQuery(id+"F0.imprint","IMPRINT",FACE,{"disambiguationData":[TD([[makeQuery(id+"F0.imprint","IMPRINT",EDGE,{"disambiguationData":[TD([[subQ2,-1.0]])],"derivedFrom":subQ1}),-1.0]])]});}
            var Q165;
            {var subQ0=sQuery(id+"F0.wireOp",EDGE,"E40");var subQ1=sQuery(id+"F0.wireOp",EDGE,"E12");var subQ2=makeQuery(id+"F0.imprint","INTERSECT",VERTEX,{"disambiguationData":[OD(1.0)],"derivedFrom":[subQ1,subQ0]});Q165=makeQuery(id+"F0.imprint","IMPRINT",FACE,{"disambiguationData":[TD([[makeQuery(id+"F0.imprint","IMPRINT",EDGE,{"disambiguationData":[TD([[subQ2,-1.0]])],"derivedFrom":subQ1}),-1.0]])]});}
            var Q166;
            {var subQ0=sQuery(id+"F0.wireOp",EDGE,"E42");var subQ1=sQuery(id+"F0.wireOp",EDGE,"E15");var subQ2=makeQuery(id+"F0.imprint","INTERSECT",VERTEX,{"derivedFrom":[subQ1,subQ0]});Q166=makeQuery(id+"F0.imprint","IMPRINT",FACE,{"disambiguationData":[TD([[makeQuery(id+"F0.imprint","IMPRINT",EDGE,{"disambiguationData":[TD([[subQ2,-1.0]])],"derivedFrom":subQ1}),-1.0]])]});}
            var Q167;
            {var subQ0=sQuery(id+"F0.wireOp",EDGE,"E40");var subQ1=sQuery(id+"F0.wireOp",EDGE,"E9");var subQ2=makeQuery(id+"F0.imprint","INTERSECT",VERTEX,{"disambiguationData":[OD(1.0)],"derivedFrom":[subQ1,subQ0]});Q167=makeQuery(id+"F0.imprint","IMPRINT",FACE,{"disambiguationData":[TD([[makeQuery(id+"F0.imprint","IMPRINT",EDGE,{"disambiguationData":[TD([[subQ2,-1.0]])],"derivedFrom":subQ1}),-1.0]])]});}
            var Q168;
            {var subQ0=sQuery(id+"F0.wireOp",EDGE,"E45");var subQ1=sQuery(id+"F0.wireOp",EDGE,"E34");var subQ2=makeQuery(id+"F0.imprint","INTERSECT",VERTEX,{"derivedFrom":[subQ1,subQ0]});Q168=makeQuery(id+"F0.imprint","IMPRINT",FACE,{"disambiguationData":[TD([[makeQuery(id+"F0.imprint","IMPRINT",EDGE,{"disambiguationData":[TD([[subQ2,-1.0]])],"derivedFrom":subQ1}),-1.0]])]});}
            var Q169;
            {var subQ0=sQuery(id+"F0.wireOp",EDGE,"E42");var subQ1=sQuery(id+"F0.wireOp",EDGE,"E16");var subQ2=makeQuery(id+"F0.imprint","INTERSECT",VERTEX,{"derivedFrom":[subQ1,subQ0]});Q169=makeQuery(id+"F0.imprint","IMPRINT",FACE,{"disambiguationData":[TD([[makeQuery(id+"F0.imprint","IMPRINT",EDGE,{"disambiguationData":[TD([[subQ2,-1.0]])],"derivedFrom":subQ1}),-1.0]])]});}
            var Q170;
            {var subQ0=sQuery(id+"F0.wireOp",EDGE,"E41");var subQ1=sQuery(id+"F0.wireOp",EDGE,"E11");var subQ2=makeQuery(id+"F0.imprint","INTERSECT",VERTEX,{"disambiguationData":[OD(1.0)],"derivedFrom":[subQ1,subQ0]});Q170=makeQuery(id+"F0.imprint","IMPRINT",FACE,{"disambiguationData":[TD([[makeQuery(id+"F0.imprint","IMPRINT",EDGE,{"disambiguationData":[TD([[subQ2,-1.0]])],"derivedFrom":subQ1}),-1.0]])]});}
            var Q171;
            {var subQ0=sQuery(id+"F0.wireOp",EDGE,"E40");var subQ1=sQuery(id+"F0.wireOp",EDGE,"E15");var subQ2=makeQuery(id+"F0.imprint","INTERSECT",VERTEX,{"disambiguationData":[OD(1.0)],"derivedFrom":[subQ1,subQ0]});Q171=makeQuery(id+"F0.imprint","IMPRINT",FACE,{"disambiguationData":[TD([[makeQuery(id+"F0.imprint","IMPRINT",EDGE,{"disambiguationData":[TD([[subQ2,-1.0]])],"derivedFrom":subQ1}),-1.0]])]});}
            var Q172;
            {var subQ0=sQuery(id+"F0.wireOp",EDGE,"E42");var subQ1=sQuery(id+"F0.wireOp",EDGE,"E18");var subQ2=makeQuery(id+"F0.imprint","INTERSECT",VERTEX,{"derivedFrom":[subQ1,subQ0]});Q172=makeQuery(id+"F0.imprint","IMPRINT",FACE,{"disambiguationData":[TD([[makeQuery(id+"F0.imprint","IMPRINT",EDGE,{"disambiguationData":[TD([[subQ2,1.0]])],"derivedFrom":subQ1}),1.0]])]});}
            var Q173;
            {var subQ0=sQuery(id+"F0.wireOp",EDGE,"E40");var subQ1=sQuery(id+"F0.wireOp",EDGE,"E4");var subQ2=makeQuery(id+"F0.imprint","INTERSECT",VERTEX,{"disambiguationData":[OD(1.0)],"derivedFrom":[subQ1,subQ0]});Q173=makeQuery(id+"F0.imprint","IMPRINT",FACE,{"disambiguationData":[TD([[makeQuery(id+"F0.imprint","IMPRINT",EDGE,{"disambiguationData":[TD([[subQ2,-1.0]])],"derivedFrom":subQ1}),-1.0]])]});}
            var Q174;
            {var subQ0=sQuery(id+"F0.wireOp",EDGE,"E42");var subQ1=sQuery(id+"F0.wireOp",EDGE,"E32");var subQ2=makeQuery(id+"F0.imprint","INTERSECT",VERTEX,{"derivedFrom":[subQ1,subQ0]});Q174=makeQuery(id+"F0.imprint","IMPRINT",FACE,{"disambiguationData":[TD([[makeQuery(id+"F0.imprint","IMPRINT",EDGE,{"disambiguationData":[TD([[subQ2,1.0]])],"derivedFrom":subQ1}),-1.0]])]});}
            var Q175;
            {var subQ0=sQuery(id+"F0.wireOp",EDGE,"E40");var subQ1=sQuery(id+"F0.wireOp",EDGE,"E29");var subQ2=makeQuery(id+"F0.imprint","INTERSECT",VERTEX,{"disambiguationData":[OD(1.0)],"derivedFrom":[subQ1,subQ0]});Q175=makeQuery(id+"F0.imprint","IMPRINT",FACE,{"disambiguationData":[TD([[makeQuery(id+"F0.imprint","IMPRINT",EDGE,{"disambiguationData":[TD([[subQ2,-1.0]])],"derivedFrom":subQ1}),-1.0]])]});}
            var Q176;
            {var subQ0=sQuery(id+"F0.wireOp",EDGE,"E42");var subQ1=sQuery(id+"F0.wireOp",EDGE,"E18");var subQ2=makeQuery(id+"F0.imprint","INTERSECT",VERTEX,{"derivedFrom":[subQ1,subQ0]});Q176=makeQuery(id+"F0.imprint","IMPRINT",FACE,{"disambiguationData":[TD([[makeQuery(id+"F0.imprint","IMPRINT",EDGE,{"disambiguationData":[TD([[subQ2,-1.0]])],"derivedFrom":subQ1}),1.0]])]});}
            var Q177;
            {var subQ0=sQuery(id+"F0.wireOp",EDGE,"E40");var subQ1=sQuery(id+"F0.wireOp",EDGE,"E25");var subQ2=makeQuery(id+"F0.imprint","INTERSECT",VERTEX,{"disambiguationData":[OD(1.0)],"derivedFrom":[subQ1,subQ0]});Q177=makeQuery(id+"F0.imprint","IMPRINT",FACE,{"disambiguationData":[TD([[makeQuery(id+"F0.imprint","IMPRINT",EDGE,{"disambiguationData":[TD([[subQ2,-1.0]])],"derivedFrom":subQ1}),-1.0]])]});}
            var Q178;
            {var subQ0=sQuery(id+"F0.wireOp",EDGE,"E41");var subQ1=sQuery(id+"F0.wireOp",EDGE,"E16");var subQ2=makeQuery(id+"F0.imprint","INTERSECT",VERTEX,{"disambiguationData":[OD(0.0)],"derivedFrom":[subQ1,subQ0]});Q178=makeQuery(id+"F0.imprint","IMPRINT",FACE,{"disambiguationData":[TD([[makeQuery(id+"F0.imprint","IMPRINT",EDGE,{"disambiguationData":[TD([[subQ2,1.0]])],"derivedFrom":subQ1}),-1.0]])]});}
            var Q179;
            {var subQ0=sQuery(id+"F0.wireOp",EDGE,"E42");var subQ1=sQuery(id+"F0.wireOp",EDGE,"E12");var subQ2=makeQuery(id+"F0.imprint","INTERSECT",VERTEX,{"derivedFrom":[subQ1,subQ0]});Q179=makeQuery(id+"F0.imprint","IMPRINT",FACE,{"disambiguationData":[TD([[makeQuery(id+"F0.imprint","IMPRINT",EDGE,{"disambiguationData":[TD([[subQ2,1.0]])],"derivedFrom":subQ1}),-1.0]])]});}
            var Q180;
            {var subQ0=sQuery(id+"F0.wireOp",EDGE,"E41");var subQ1=sQuery(id+"F0.wireOp",EDGE,"E26");var subQ2=makeQuery(id+"F0.imprint","INTERSECT",VERTEX,{"disambiguationData":[OD(1.0)],"derivedFrom":[subQ1,subQ0]});Q180=makeQuery(id+"F0.imprint","IMPRINT",FACE,{"disambiguationData":[TD([[makeQuery(id+"F0.imprint","IMPRINT",EDGE,{"disambiguationData":[TD([[subQ2,-1.0]])],"derivedFrom":subQ1}),-1.0]])]});}
            var Q181;
            {var subQ0=sQuery(id+"F0.wireOp",EDGE,"E42");var subQ1=sQuery(id+"F0.wireOp",EDGE,"E25");var subQ2=makeQuery(id+"F0.imprint","INTERSECT",VERTEX,{"derivedFrom":[subQ1,subQ0]});Q181=makeQuery(id+"F0.imprint","IMPRINT",FACE,{"disambiguationData":[TD([[makeQuery(id+"F0.imprint","IMPRINT",EDGE,{"disambiguationData":[TD([[subQ2,-1.0]])],"derivedFrom":subQ1}),-1.0]])]});}
            var Q182;
            {var subQ0=sQuery(id+"F0.wireOp",EDGE,"E40");var subQ1=sQuery(id+"F0.wireOp",EDGE,"E35");var subQ2=makeQuery(id+"F0.imprint","INTERSECT",VERTEX,{"disambiguationData":[OD(1.0)],"derivedFrom":[subQ1,subQ0]});Q182=makeQuery(id+"F0.imprint","IMPRINT",FACE,{"disambiguationData":[TD([[makeQuery(id+"F0.imprint","IMPRINT",EDGE,{"disambiguationData":[TD([[subQ2,-1.0]])],"derivedFrom":subQ1}),-1.0]])]});}
            var Q183;
            {var subQ0=sQuery(id+"F0.wireOp",EDGE,"E40");var subQ1=sQuery(id+"F0.wireOp",EDGE,"E8");var subQ2=makeQuery(id+"F0.imprint","INTERSECT",VERTEX,{"disambiguationData":[OD(0.0)],"derivedFrom":[subQ1,subQ0]});Q183=makeQuery(id+"F0.imprint","IMPRINT",FACE,{"disambiguationData":[TD([[makeQuery(id+"F0.imprint","IMPRINT",EDGE,{"disambiguationData":[TD([[subQ2,-1.0]])],"derivedFrom":subQ1}),-1.0]])]});}
            var Q184;
            {var subQ0=sQuery(id+"F0.wireOp",EDGE,"E42");var subQ1=sQuery(id+"F0.wireOp",EDGE,"E4");var subQ2=makeQuery(id+"F0.imprint","INTERSECT",VERTEX,{"derivedFrom":[subQ1,subQ0]});Q184=makeQuery(id+"F0.imprint","IMPRINT",FACE,{"disambiguationData":[TD([[makeQuery(id+"F0.imprint","IMPRINT",EDGE,{"disambiguationData":[TD([[subQ2,-1.0]])],"derivedFrom":subQ1}),1.0]])]});}
            var Q185;
            {var subQ0=sQuery(id+"F0.wireOp",EDGE,"E41");var subQ1=sQuery(id+"F0.wireOp",EDGE,"E15");var subQ2=makeQuery(id+"F0.imprint","INTERSECT",VERTEX,{"disambiguationData":[OD(1.0)],"derivedFrom":[subQ1,subQ0]});Q185=makeQuery(id+"F0.imprint","IMPRINT",FACE,{"disambiguationData":[TD([[makeQuery(id+"F0.imprint","IMPRINT",EDGE,{"disambiguationData":[TD([[subQ2,-1.0]])],"derivedFrom":subQ1}),-1.0]])]});}
            var Q186;
            {var subQ0=sQuery(id+"F0.wireOp",EDGE,"E40");var subQ1=sQuery(id+"F0.wireOp",EDGE,"E31");var subQ2=makeQuery(id+"F0.imprint","INTERSECT",VERTEX,{"disambiguationData":[OD(0.0)],"derivedFrom":[subQ1,subQ0]});Q186=makeQuery(id+"F0.imprint","IMPRINT",FACE,{"disambiguationData":[TD([[makeQuery(id+"F0.imprint","IMPRINT",EDGE,{"disambiguationData":[TD([[subQ2,-1.0]])],"derivedFrom":subQ1}),-1.0]])]});}
            var Q187;
            {var subQ0=sQuery(id+"F0.wireOp",EDGE,"E41");var subQ1=sQuery(id+"F0.wireOp",EDGE,"E31");var subQ2=makeQuery(id+"F0.imprint","INTERSECT",VERTEX,{"disambiguationData":[OD(0.0)],"derivedFrom":[subQ1,subQ0]});Q187=makeQuery(id+"F0.imprint","IMPRINT",FACE,{"disambiguationData":[TD([[makeQuery(id+"F0.imprint","IMPRINT",EDGE,{"disambiguationData":[TD([[subQ2,1.0]])],"derivedFrom":subQ1}),-1.0]])]});}
            var Q188;
            {var subQ0=sQuery(id+"F0.wireOp",EDGE,"E40");var subQ1=sQuery(id+"F0.wireOp",EDGE,"E17");var subQ2=makeQuery(id+"F0.imprint","INTERSECT",VERTEX,{"disambiguationData":[OD(0.0)],"derivedFrom":[subQ1,subQ0]});Q188=makeQuery(id+"F0.imprint","IMPRINT",FACE,{"disambiguationData":[TD([[makeQuery(id+"F0.imprint","IMPRINT",EDGE,{"disambiguationData":[TD([[subQ2,-1.0]])],"derivedFrom":subQ1}),1.0]])]});}
            var Q189;
            {var subQ0=sQuery(id+"F0.wireOp",EDGE,"E42");var subQ1=sQuery(id+"F0.wireOp",EDGE,"E25");var subQ2=makeQuery(id+"F0.imprint","INTERSECT",VERTEX,{"derivedFrom":[subQ1,subQ0]});Q189=makeQuery(id+"F0.imprint","IMPRINT",FACE,{"disambiguationData":[TD([[makeQuery(id+"F0.imprint","IMPRINT",EDGE,{"disambiguationData":[TD([[subQ2,1.0]])],"derivedFrom":subQ1}),-1.0]])]});}
            var Q190;
            {var subQ0=sQuery(id+"F0.wireOp",EDGE,"E42");var subQ1=sQuery(id+"F0.wireOp",EDGE,"E4");var subQ2=makeQuery(id+"F0.imprint","INTERSECT",VERTEX,{"derivedFrom":[subQ1,subQ0]});Q190=makeQuery(id+"F0.imprint","IMPRINT",FACE,{"disambiguationData":[TD([[makeQuery(id+"F0.imprint","IMPRINT",EDGE,{"disambiguationData":[TD([[subQ2,-1.0]])],"derivedFrom":subQ1}),-1.0]])]});}
            var Q191;
            {var subQ0=sQuery(id+"F0.wireOp",EDGE,"E42");var subQ1=sQuery(id+"F0.wireOp",EDGE,"E31");var subQ2=makeQuery(id+"F0.imprint","INTERSECT",VERTEX,{"derivedFrom":[subQ1,subQ0]});Q191=makeQuery(id+"F0.imprint","IMPRINT",FACE,{"disambiguationData":[TD([[makeQuery(id+"F0.imprint","IMPRINT",EDGE,{"disambiguationData":[TD([[subQ2,-1.0]])],"derivedFrom":subQ1}),-1.0]])]});}
            var Q192;
            {var subQ0=sQuery(id+"F0.wireOp",EDGE,"E41");var subQ1=sQuery(id+"F0.wireOp",EDGE,"E28");var subQ2=makeQuery(id+"F0.imprint","INTERSECT",VERTEX,{"disambiguationData":[OD(0.0)],"derivedFrom":[subQ1,subQ0]});Q192=makeQuery(id+"F0.imprint","IMPRINT",FACE,{"disambiguationData":[TD([[makeQuery(id+"F0.imprint","IMPRINT",EDGE,{"disambiguationData":[TD([[subQ2,1.0]])],"derivedFrom":subQ1}),-1.0]])]});}
            var Q193;
            {var subQ0=sQuery(id+"F0.wireOp",EDGE,"E40");var subQ1=sQuery(id+"F0.wireOp",EDGE,"E37");var subQ2=makeQuery(id+"F0.imprint","INTERSECT",VERTEX,{"disambiguationData":[OD(0.0)],"derivedFrom":[subQ1,subQ0]});Q193=makeQuery(id+"F0.imprint","IMPRINT",FACE,{"disambiguationData":[TD([[makeQuery(id+"F0.imprint","IMPRINT",EDGE,{"disambiguationData":[TD([[subQ2,-1.0]])],"derivedFrom":subQ1}),-1.0]])]});}
            var Q194;
            {var subQ0=sQuery(id+"F0.wireOp",EDGE,"E45");var subQ1=sQuery(id+"F0.wireOp",EDGE,"E14");var subQ2=makeQuery(id+"F0.imprint","INTERSECT",VERTEX,{"derivedFrom":[subQ1,subQ0]});Q194=makeQuery(id+"F0.imprint","IMPRINT",FACE,{"disambiguationData":[TD([[makeQuery(id+"F0.imprint","IMPRINT",EDGE,{"disambiguationData":[TD([[subQ2,-1.0]])],"derivedFrom":subQ1}),-1.0]])]});}
            var Q195;
            {var subQ0=sQuery(id+"F0.wireOp",EDGE,"E45");var subQ1=sQuery(id+"F0.wireOp",EDGE,"E4");var subQ2=makeQuery(id+"F0.imprint","INTERSECT",VERTEX,{"derivedFrom":[subQ1,subQ0]});Q195=makeQuery(id+"F0.imprint","IMPRINT",FACE,{"disambiguationData":[TD([[makeQuery(id+"F0.imprint","IMPRINT",EDGE,{"disambiguationData":[TD([[subQ2,-1.0]])],"derivedFrom":subQ1}),-1.0]])]});}
            var Q196;
            {var subQ0=sQuery(id+"F0.wireOp",EDGE,"E45");var subQ1=sQuery(id+"F0.wireOp",EDGE,"E17");var subQ2=makeQuery(id+"F0.imprint","INTERSECT",VERTEX,{"derivedFrom":[subQ1,subQ0]});Q196=makeQuery(id+"F0.imprint","IMPRINT",FACE,{"disambiguationData":[TD([[makeQuery(id+"F0.imprint","IMPRINT",EDGE,{"disambiguationData":[TD([[subQ2,-1.0]])],"derivedFrom":subQ1}),-1.0]])]});}
            var Q197;
            {var subQ0=sQuery(id+"F0.wireOp",EDGE,"E45");var subQ1=sQuery(id+"F0.wireOp",EDGE,"E20");var subQ2=makeQuery(id+"F0.imprint","INTERSECT",VERTEX,{"derivedFrom":[subQ1,subQ0]});Q197=makeQuery(id+"F0.imprint","IMPRINT",FACE,{"disambiguationData":[TD([[makeQuery(id+"F0.imprint","IMPRINT",EDGE,{"disambiguationData":[TD([[subQ2,-1.0]])],"derivedFrom":subQ1}),-1.0]])]});}
            var Q198;
            {var subQ0=sQuery(id+"F0.wireOp",EDGE,"E42");var subQ1=sQuery(id+"F0.wireOp",EDGE,"E35");var subQ2=makeQuery(id+"F0.imprint","INTERSECT",VERTEX,{"derivedFrom":[subQ1,subQ0]});Q198=makeQuery(id+"F0.imprint","IMPRINT",FACE,{"disambiguationData":[TD([[makeQuery(id+"F0.imprint","IMPRINT",EDGE,{"disambiguationData":[TD([[subQ2,1.0]])],"derivedFrom":subQ1}),-1.0]])]});}
            var Q199;
            {var subQ0=sQuery(id+"F0.wireOp",EDGE,"E42");var subQ1=sQuery(id+"F0.wireOp",EDGE,"E2");var subQ2=makeQuery(id+"F0.imprint","INTERSECT",VERTEX,{"derivedFrom":[subQ1,subQ0]});Q199=makeQuery(id+"F0.imprint","IMPRINT",FACE,{"disambiguationData":[TD([[makeQuery(id+"F0.imprint","IMPRINT",EDGE,{"disambiguationData":[TD([[subQ2,1.0]])],"derivedFrom":subQ1}),-1.0]])]});}
            var Q200;
            {var subQ0=sQuery(id+"F0.wireOp",EDGE,"E40");var subQ1=sQuery(id+"F0.wireOp",EDGE,"E26");var subQ2=makeQuery(id+"F0.imprint","INTERSECT",VERTEX,{"disambiguationData":[OD(1.0)],"derivedFrom":[subQ1,subQ0]});Q200=makeQuery(id+"F0.imprint","IMPRINT",FACE,{"disambiguationData":[TD([[makeQuery(id+"F0.imprint","IMPRINT",EDGE,{"disambiguationData":[TD([[subQ2,-1.0]])],"derivedFrom":subQ1}),-1.0]])]});}
            var Q201;
            {var subQ0=sQuery(id+"F0.wireOp",EDGE,"E45");var subQ1=sQuery(id+"F0.wireOp",EDGE,"E13");var subQ2=makeQuery(id+"F0.imprint","INTERSECT",VERTEX,{"derivedFrom":[subQ1,subQ0]});Q201=makeQuery(id+"F0.imprint","IMPRINT",FACE,{"disambiguationData":[TD([[makeQuery(id+"F0.imprint","IMPRINT",EDGE,{"disambiguationData":[TD([[subQ2,-1.0]])],"derivedFrom":subQ1}),-1.0]])]});}
            var Q202;
            {var subQ0=sQuery(id+"F0.wireOp",EDGE,"E42");var subQ1=sQuery(id+"F0.wireOp",EDGE,"E36");var subQ2=makeQuery(id+"F0.imprint","INTERSECT",VERTEX,{"derivedFrom":[subQ1,subQ0]});Q202=makeQuery(id+"F0.imprint","IMPRINT",FACE,{"disambiguationData":[TD([[makeQuery(id+"F0.imprint","IMPRINT",EDGE,{"disambiguationData":[TD([[subQ2,-1.0]])],"derivedFrom":subQ1}),-1.0]])]});}
            var Q203;
            {var subQ0=sQuery(id+"F0.wireOp",EDGE,"E42");var subQ1=sQuery(id+"F0.wireOp",EDGE,"E9");var subQ2=makeQuery(id+"F0.imprint","INTERSECT",VERTEX,{"derivedFrom":[subQ1,subQ0]});Q203=makeQuery(id+"F0.imprint","IMPRINT",FACE,{"disambiguationData":[TD([[makeQuery(id+"F0.imprint","IMPRINT",EDGE,{"disambiguationData":[TD([[subQ2,1.0]])],"derivedFrom":subQ1}),-1.0]])]});}
            var Q204;
            {var subQ0=sQuery(id+"F0.wireOp",EDGE,"E40");var subQ1=sQuery(id+"F0.wireOp",EDGE,"E10");var subQ2=makeQuery(id+"F0.imprint","INTERSECT",VERTEX,{"disambiguationData":[OD(1.0)],"derivedFrom":[subQ1,subQ0]});Q204=makeQuery(id+"F0.imprint","IMPRINT",FACE,{"disambiguationData":[TD([[makeQuery(id+"F0.imprint","IMPRINT",EDGE,{"disambiguationData":[TD([[subQ2,-1.0]])],"derivedFrom":subQ1}),-1.0]])]});}
            var Q205;
            {var subQ0=sQuery(id+"F0.wireOp",EDGE,"E42");var subQ1=sQuery(id+"F0.wireOp",EDGE,"E18");var subQ2=makeQuery(id+"F0.imprint","INTERSECT",VERTEX,{"derivedFrom":[subQ1,subQ0]});Q205=makeQuery(id+"F0.imprint","IMPRINT",FACE,{"disambiguationData":[TD([[makeQuery(id+"F0.imprint","IMPRINT",EDGE,{"disambiguationData":[TD([[subQ2,-1.0]])],"derivedFrom":subQ1}),-1.0]])]});}
            var Q206;
            {var subQ0=sQuery(id+"F0.wireOp",EDGE,"E42");var subQ1=sQuery(id+"F0.wireOp",EDGE,"E27");var subQ2=makeQuery(id+"F0.imprint","INTERSECT",VERTEX,{"derivedFrom":[subQ1,subQ0]});Q206=makeQuery(id+"F0.imprint","IMPRINT",FACE,{"disambiguationData":[TD([[makeQuery(id+"F0.imprint","IMPRINT",EDGE,{"disambiguationData":[TD([[subQ2,1.0]])],"derivedFrom":subQ1}),-1.0]])]});}
            var Q207;
            {var subQ0=sQuery(id+"F0.wireOp",EDGE,"E40");var subQ1=sQuery(id+"F0.wireOp",EDGE,"E13");var subQ2=makeQuery(id+"F0.imprint","INTERSECT",VERTEX,{"disambiguationData":[OD(0.0)],"derivedFrom":[subQ1,subQ0]});Q207=makeQuery(id+"F0.imprint","IMPRINT",FACE,{"disambiguationData":[TD([[makeQuery(id+"F0.imprint","IMPRINT",EDGE,{"disambiguationData":[TD([[subQ2,-1.0]])],"derivedFrom":subQ1}),-1.0]])]});}
            var Q208;
            {var subQ0=sQuery(id+"F0.wireOp",EDGE,"E41");var subQ1=sQuery(id+"F0.wireOp",EDGE,"E23");var subQ2=makeQuery(id+"F0.imprint","INTERSECT",VERTEX,{"disambiguationData":[OD(1.0)],"derivedFrom":[subQ1,subQ0]});Q208=makeQuery(id+"F0.imprint","IMPRINT",FACE,{"disambiguationData":[TD([[makeQuery(id+"F0.imprint","IMPRINT",EDGE,{"disambiguationData":[TD([[subQ2,-1.0]])],"derivedFrom":subQ1}),1.0]])]});}
            var Q209;
            {var subQ0=sQuery(id+"F0.wireOp",EDGE,"E42");var subQ1=sQuery(id+"F0.wireOp",EDGE,"E28");var subQ2=makeQuery(id+"F0.imprint","INTERSECT",VERTEX,{"derivedFrom":[subQ1,subQ0]});Q209=makeQuery(id+"F0.imprint","IMPRINT",FACE,{"disambiguationData":[TD([[makeQuery(id+"F0.imprint","IMPRINT",EDGE,{"disambiguationData":[TD([[subQ2,-1.0]])],"derivedFrom":subQ1}),-1.0]])]});}
            var Q210;
            {var subQ0=sQuery(id+"F0.wireOp",EDGE,"E41");var subQ1=sQuery(id+"F0.wireOp",EDGE,"E17");var subQ2=makeQuery(id+"F0.imprint","INTERSECT",VERTEX,{"disambiguationData":[OD(0.0)],"derivedFrom":[subQ1,subQ0]});Q210=makeQuery(id+"F0.imprint","IMPRINT",FACE,{"disambiguationData":[TD([[makeQuery(id+"F0.imprint","IMPRINT",EDGE,{"disambiguationData":[TD([[subQ2,1.0]])],"derivedFrom":subQ1}),-1.0]])]});}
            var Q211;
            {var subQ0=sQuery(id+"F0.wireOp",EDGE,"E41");var subQ1=sQuery(id+"F0.wireOp",EDGE,"E34");var subQ2=makeQuery(id+"F0.imprint","INTERSECT",VERTEX,{"disambiguationData":[OD(0.0)],"derivedFrom":[subQ1,subQ0]});Q211=makeQuery(id+"F0.imprint","IMPRINT",FACE,{"disambiguationData":[TD([[makeQuery(id+"F0.imprint","IMPRINT",EDGE,{"disambiguationData":[TD([[subQ2,1.0]])],"derivedFrom":subQ1}),-1.0]])]});}
            var Q212;
            {var subQ0=sQuery(id+"F0.wireOp",EDGE,"E41");var subQ1=sQuery(id+"F0.wireOp",EDGE,"E12");var subQ2=makeQuery(id+"F0.imprint","INTERSECT",VERTEX,{"disambiguationData":[OD(1.0)],"derivedFrom":[subQ1,subQ0]});Q212=makeQuery(id+"F0.imprint","IMPRINT",FACE,{"disambiguationData":[TD([[makeQuery(id+"F0.imprint","IMPRINT",EDGE,{"disambiguationData":[TD([[subQ2,-1.0]])],"derivedFrom":subQ1}),-1.0]])]});}
            var Q213;
            {var subQ0=sQuery(id+"F0.wireOp",EDGE,"E42");var subQ1=sQuery(id+"F0.wireOp",EDGE,"E23");var subQ2=makeQuery(id+"F0.imprint","INTERSECT",VERTEX,{"derivedFrom":[subQ1,subQ0]});Q213=makeQuery(id+"F0.imprint","IMPRINT",FACE,{"disambiguationData":[TD([[makeQuery(id+"F0.imprint","IMPRINT",EDGE,{"disambiguationData":[TD([[subQ2,1.0]])],"derivedFrom":subQ1}),1.0]])]});}
            var Q214;
            {var subQ0=sQuery(id+"F0.wireOp",EDGE,"E41");var subQ1=sQuery(id+"F0.wireOp",EDGE,"E35");var subQ2=makeQuery(id+"F0.imprint","INTERSECT",VERTEX,{"disambiguationData":[OD(1.0)],"derivedFrom":[subQ1,subQ0]});Q214=makeQuery(id+"F0.imprint","IMPRINT",FACE,{"disambiguationData":[TD([[makeQuery(id+"F0.imprint","IMPRINT",EDGE,{"disambiguationData":[TD([[subQ2,-1.0]])],"derivedFrom":subQ1}),-1.0]])]});}
            var Q215;
            {var subQ0=sQuery(id+"F0.wireOp",EDGE,"E41");var subQ1=sQuery(id+"F0.wireOp",EDGE,"E14");var subQ2=makeQuery(id+"F0.imprint","INTERSECT",VERTEX,{"disambiguationData":[OD(1.0)],"derivedFrom":[subQ1,subQ0]});Q215=makeQuery(id+"F0.imprint","IMPRINT",FACE,{"disambiguationData":[TD([[makeQuery(id+"F0.imprint","IMPRINT",EDGE,{"disambiguationData":[TD([[subQ2,-1.0]])],"derivedFrom":subQ1}),-1.0]])]});}
            var Q216;
            {var subQ0=sQuery(id+"F0.wireOp",EDGE,"E40");var subQ1=sQuery(id+"F0.wireOp",EDGE,"E14");var subQ2=makeQuery(id+"F0.imprint","INTERSECT",VERTEX,{"disambiguationData":[OD(0.0)],"derivedFrom":[subQ1,subQ0]});Q216=makeQuery(id+"F0.imprint","IMPRINT",FACE,{"disambiguationData":[TD([[makeQuery(id+"F0.imprint","IMPRINT",EDGE,{"disambiguationData":[TD([[subQ2,-1.0]])],"derivedFrom":subQ1}),-1.0]])]});}
            var Q217;
            {var subQ0=sQuery(id+"F0.wireOp",EDGE,"E41");var subQ1=sQuery(id+"F0.wireOp",EDGE,"E27");var subQ2=makeQuery(id+"F0.imprint","INTERSECT",VERTEX,{"disambiguationData":[OD(0.0)],"derivedFrom":[subQ1,subQ0]});Q217=makeQuery(id+"F0.imprint","IMPRINT",FACE,{"disambiguationData":[TD([[makeQuery(id+"F0.imprint","IMPRINT",EDGE,{"disambiguationData":[TD([[subQ2,1.0]])],"derivedFrom":subQ1}),-1.0]])]});}
            var Q218;
            {var subQ0=sQuery(id+"F0.wireOp",EDGE,"E41");var subQ1=sQuery(id+"F0.wireOp",EDGE,"E5");var subQ2=makeQuery(id+"F0.imprint","INTERSECT",VERTEX,{"disambiguationData":[OD(1.0)],"derivedFrom":[subQ1,subQ0]});Q218=makeQuery(id+"F0.imprint","IMPRINT",FACE,{"disambiguationData":[TD([[makeQuery(id+"F0.imprint","IMPRINT",EDGE,{"disambiguationData":[TD([[subQ2,-1.0]])],"derivedFrom":subQ1}),-1.0]])]});}
            var Q219;
            {var subQ0=sQuery(id+"F0.wireOp",EDGE,"E40");var subQ1=sQuery(id+"F0.wireOp",EDGE,"E17");var subQ2=makeQuery(id+"F0.imprint","INTERSECT",VERTEX,{"disambiguationData":[OD(1.0)],"derivedFrom":[subQ1,subQ0]});Q219=makeQuery(id+"F0.imprint","IMPRINT",FACE,{"disambiguationData":[TD([[makeQuery(id+"F0.imprint","IMPRINT",EDGE,{"disambiguationData":[TD([[subQ2,-1.0]])],"derivedFrom":subQ1}),1.0]])]});}
            var Q220;
            {var subQ0=sQuery(id+"F0.wireOp",EDGE,"E41");var subQ1=sQuery(id+"F0.wireOp",EDGE,"E17");var subQ2=makeQuery(id+"F0.imprint","INTERSECT",VERTEX,{"disambiguationData":[OD(1.0)],"derivedFrom":[subQ1,subQ0]});Q220=makeQuery(id+"F0.imprint","IMPRINT",FACE,{"disambiguationData":[TD([[makeQuery(id+"F0.imprint","IMPRINT",EDGE,{"disambiguationData":[TD([[subQ2,-1.0]])],"derivedFrom":subQ1}),1.0]])]});}
            var Q221;
            {var subQ0=sQuery(id+"F0.wireOp",EDGE,"E45");var subQ1=sQuery(id+"F0.wireOp",EDGE,"E12");var subQ2=makeQuery(id+"F0.imprint","INTERSECT",VERTEX,{"derivedFrom":[subQ1,subQ0]});Q221=makeQuery(id+"F0.imprint","IMPRINT",FACE,{"disambiguationData":[TD([[makeQuery(id+"F0.imprint","IMPRINT",EDGE,{"disambiguationData":[TD([[subQ2,-1.0]])],"derivedFrom":subQ1}),-1.0]])]});}
            var Q222;
            {var subQ0=sQuery(id+"F0.wireOp",EDGE,"E42");var subQ1=sQuery(id+"F0.wireOp",EDGE,"E14");var subQ2=makeQuery(id+"F0.imprint","INTERSECT",VERTEX,{"derivedFrom":[subQ1,subQ0]});Q222=makeQuery(id+"F0.imprint","IMPRINT",FACE,{"disambiguationData":[TD([[makeQuery(id+"F0.imprint","IMPRINT",EDGE,{"disambiguationData":[TD([[subQ2,1.0]])],"derivedFrom":subQ1}),-1.0]])]});}
            var Q223;
            {var subQ0=sQuery(id+"F0.wireOp",EDGE,"E41");var subQ1=sQuery(id+"F0.wireOp",EDGE,"E34");var subQ2=makeQuery(id+"F0.imprint","INTERSECT",VERTEX,{"disambiguationData":[OD(1.0)],"derivedFrom":[subQ1,subQ0]});Q223=makeQuery(id+"F0.imprint","IMPRINT",FACE,{"disambiguationData":[TD([[makeQuery(id+"F0.imprint","IMPRINT",EDGE,{"disambiguationData":[TD([[subQ2,-1.0]])],"derivedFrom":subQ1}),-1.0]])]});}
            var Q224;
            {var subQ0=sQuery(id+"F0.wireOp",EDGE,"E45");var subQ1=sQuery(id+"F0.wireOp",EDGE,"E33");var subQ2=makeQuery(id+"F0.imprint","INTERSECT",VERTEX,{"derivedFrom":[subQ1,subQ0]});Q224=makeQuery(id+"F0.imprint","IMPRINT",FACE,{"disambiguationData":[TD([[makeQuery(id+"F0.imprint","IMPRINT",EDGE,{"disambiguationData":[TD([[subQ2,-1.0]])],"derivedFrom":subQ1}),-1.0]])]});}
            var Q225;
            {var subQ0=sQuery(id+"F0.wireOp",EDGE,"E41");var subQ1=sQuery(id+"F0.wireOp",EDGE,"E18");var subQ2=makeQuery(id+"F0.imprint","INTERSECT",VERTEX,{"disambiguationData":[OD(1.0)],"derivedFrom":[subQ1,subQ0]});Q225=makeQuery(id+"F0.imprint","IMPRINT",FACE,{"disambiguationData":[TD([[makeQuery(id+"F0.imprint","IMPRINT",EDGE,{"disambiguationData":[TD([[subQ2,-1.0]])],"derivedFrom":subQ1}),1.0]])]});}
            var Q226;
            {var subQ0=sQuery(id+"F0.wireOp",EDGE,"E41");var subQ1=sQuery(id+"F0.wireOp",EDGE,"E25");var subQ2=makeQuery(id+"F0.imprint","INTERSECT",VERTEX,{"disambiguationData":[OD(1.0)],"derivedFrom":[subQ1,subQ0]});Q226=makeQuery(id+"F0.imprint","IMPRINT",FACE,{"disambiguationData":[TD([[makeQuery(id+"F0.imprint","IMPRINT",EDGE,{"disambiguationData":[TD([[subQ2,-1.0]])],"derivedFrom":subQ1}),-1.0]])]});}
            var Q227;
            {var subQ0=sQuery(id+"F0.wireOp",EDGE,"E45");var subQ1=sQuery(id+"F0.wireOp",EDGE,"E3");var subQ2=makeQuery(id+"F0.imprint","INTERSECT",VERTEX,{"derivedFrom":[subQ1,subQ0]});Q227=makeQuery(id+"F0.imprint","IMPRINT",FACE,{"disambiguationData":[TD([[makeQuery(id+"F0.imprint","IMPRINT",EDGE,{"disambiguationData":[TD([[subQ2,-1.0]])],"derivedFrom":subQ1}),-1.0]])]});}
            var Q228;
            {var subQ0=sQuery(id+"F0.wireOp",EDGE,"E42");var subQ1=sQuery(id+"F0.wireOp",EDGE,"E33");var subQ2=makeQuery(id+"F0.imprint","INTERSECT",VERTEX,{"derivedFrom":[subQ1,subQ0]});Q228=makeQuery(id+"F0.imprint","IMPRINT",FACE,{"disambiguationData":[TD([[makeQuery(id+"F0.imprint","IMPRINT",EDGE,{"disambiguationData":[TD([[subQ2,1.0]])],"derivedFrom":subQ1}),-1.0]])]});}
            var Q229;
            {var subQ0=sQuery(id+"F0.wireOp",EDGE,"E45");var subQ1=sQuery(id+"F0.wireOp",EDGE,"E18");var subQ2=makeQuery(id+"F0.imprint","INTERSECT",VERTEX,{"derivedFrom":[subQ1,subQ0]});Q229=makeQuery(id+"F0.imprint","IMPRINT",FACE,{"disambiguationData":[TD([[makeQuery(id+"F0.imprint","IMPRINT",EDGE,{"disambiguationData":[TD([[subQ2,-1.0]])],"derivedFrom":subQ1}),1.0]])]});}
            var Q230;
            {var subQ0=sQuery(id+"F0.wireOp",EDGE,"E40");var subQ1=sQuery(id+"F0.wireOp",EDGE,"E36");var subQ2=makeQuery(id+"F0.imprint","INTERSECT",VERTEX,{"disambiguationData":[OD(0.0)],"derivedFrom":[subQ1,subQ0]});Q230=makeQuery(id+"F0.imprint","IMPRINT",FACE,{"disambiguationData":[TD([[makeQuery(id+"F0.imprint","IMPRINT",EDGE,{"disambiguationData":[TD([[subQ2,-1.0]])],"derivedFrom":subQ1}),-1.0]])]});}
            var Q231;
            {var subQ0=sQuery(id+"F0.wireOp",EDGE,"E40");var subQ1=sQuery(id+"F0.wireOp",EDGE,"E32");var subQ2=makeQuery(id+"F0.imprint","INTERSECT",VERTEX,{"disambiguationData":[OD(1.0)],"derivedFrom":[subQ1,subQ0]});Q231=makeQuery(id+"F0.imprint","IMPRINT",FACE,{"disambiguationData":[TD([[makeQuery(id+"F0.imprint","IMPRINT",EDGE,{"disambiguationData":[TD([[subQ2,-1.0]])],"derivedFrom":subQ1}),-1.0]])]});}
            var Q232;
            {var subQ0=sQuery(id+"F0.wireOp",EDGE,"E41");var subQ1=sQuery(id+"F0.wireOp",EDGE,"E17");var subQ2=makeQuery(id+"F0.imprint","INTERSECT",VERTEX,{"disambiguationData":[OD(1.0)],"derivedFrom":[subQ1,subQ0]});Q232=makeQuery(id+"F0.imprint","IMPRINT",FACE,{"disambiguationData":[TD([[makeQuery(id+"F0.imprint","IMPRINT",EDGE,{"disambiguationData":[TD([[subQ2,-1.0]])],"derivedFrom":subQ1}),-1.0]])]});}
            var Q233;
            {var subQ0=sQuery(id+"F0.wireOp",EDGE,"E41");var subQ1=sQuery(id+"F0.wireOp",EDGE,"E14");var subQ2=makeQuery(id+"F0.imprint","INTERSECT",VERTEX,{"disambiguationData":[OD(0.0)],"derivedFrom":[subQ1,subQ0]});Q233=makeQuery(id+"F0.imprint","IMPRINT",FACE,{"disambiguationData":[TD([[makeQuery(id+"F0.imprint","IMPRINT",EDGE,{"disambiguationData":[TD([[subQ2,1.0]])],"derivedFrom":subQ1}),-1.0]])]});}
            var Q234;
            {var subQ0=sQuery(id+"F0.wireOp",EDGE,"E41");var subQ1=sQuery(id+"F0.wireOp",EDGE,"E12");var subQ2=makeQuery(id+"F0.imprint","INTERSECT",VERTEX,{"disambiguationData":[OD(0.0)],"derivedFrom":[subQ1,subQ0]});Q234=makeQuery(id+"F0.imprint","IMPRINT",FACE,{"disambiguationData":[TD([[makeQuery(id+"F0.imprint","IMPRINT",EDGE,{"disambiguationData":[TD([[subQ2,1.0]])],"derivedFrom":subQ1}),-1.0]])]});}
            var Q235;
            {var subQ0=sQuery(id+"F0.wireOp",EDGE,"E45");var subQ1=sQuery(id+"F0.wireOp",EDGE,"E4");var subQ2=makeQuery(id+"F0.imprint","INTERSECT",VERTEX,{"derivedFrom":[subQ1,subQ0]});Q235=makeQuery(id+"F0.imprint","IMPRINT",FACE,{"disambiguationData":[TD([[makeQuery(id+"F0.imprint","IMPRINT",EDGE,{"disambiguationData":[TD([[subQ2,-1.0]])],"derivedFrom":subQ1}),1.0]])]});}
            var Q236;
            {var subQ0=sQuery(id+"F0.wireOp",EDGE,"E45");var subQ1=sQuery(id+"F0.wireOp",EDGE,"E23");var subQ2=makeQuery(id+"F0.imprint","INTERSECT",VERTEX,{"derivedFrom":[subQ1,subQ0]});Q236=makeQuery(id+"F0.imprint","IMPRINT",FACE,{"disambiguationData":[TD([[makeQuery(id+"F0.imprint","IMPRINT",EDGE,{"disambiguationData":[TD([[subQ2,-1.0]])],"derivedFrom":subQ1}),-1.0]])]});}
            var Q237;
            {var subQ0=sQuery(id+"F0.wireOp",EDGE,"E45");var subQ1=sQuery(id+"F0.wireOp",EDGE,"E27");var subQ2=makeQuery(id+"F0.imprint","INTERSECT",VERTEX,{"derivedFrom":[subQ1,subQ0]});Q237=makeQuery(id+"F0.imprint","IMPRINT",FACE,{"disambiguationData":[TD([[makeQuery(id+"F0.imprint","IMPRINT",EDGE,{"disambiguationData":[TD([[subQ2,-1.0]])],"derivedFrom":subQ1}),-1.0]])]});}
            var Q238;
            {var subQ0=sQuery(id+"F0.wireOp",EDGE,"E42");var subQ1=sQuery(id+"F0.wireOp",EDGE,"E34");var subQ2=makeQuery(id+"F0.imprint","INTERSECT",VERTEX,{"derivedFrom":[subQ1,subQ0]});Q238=makeQuery(id+"F0.imprint","IMPRINT",FACE,{"disambiguationData":[TD([[makeQuery(id+"F0.imprint","IMPRINT",EDGE,{"disambiguationData":[TD([[subQ2,1.0]])],"derivedFrom":subQ1}),-1.0]])]});}
            var Q239;
            {var subQ0=sQuery(id+"F0.wireOp",EDGE,"E42");var subQ1=sQuery(id+"F0.wireOp",EDGE,"E17");var subQ2=makeQuery(id+"F0.imprint","INTERSECT",VERTEX,{"derivedFrom":[subQ1,subQ0]});Q239=makeQuery(id+"F0.imprint","IMPRINT",FACE,{"disambiguationData":[TD([[makeQuery(id+"F0.imprint","IMPRINT",EDGE,{"disambiguationData":[TD([[subQ2,-1.0]])],"derivedFrom":subQ1}),-1.0]])]});}
            var Q240;
            {var subQ0=sQuery(id+"F0.wireOp",EDGE,"E40");var subQ1=sQuery(id+"F0.wireOp",EDGE,"E33");var subQ2=makeQuery(id+"F0.imprint","INTERSECT",VERTEX,{"disambiguationData":[OD(1.0)],"derivedFrom":[subQ1,subQ0]});Q240=makeQuery(id+"F0.imprint","IMPRINT",FACE,{"disambiguationData":[TD([[makeQuery(id+"F0.imprint","IMPRINT",EDGE,{"disambiguationData":[TD([[subQ2,-1.0]])],"derivedFrom":subQ1}),-1.0]])]});}
            var Q241;
            {var subQ0=sQuery(id+"F0.wireOp",EDGE,"E42");var subQ1=sQuery(id+"F0.wireOp",EDGE,"E18");var subQ2=makeQuery(id+"F0.imprint","INTERSECT",VERTEX,{"derivedFrom":[subQ1,subQ0]});Q241=makeQuery(id+"F0.imprint","IMPRINT",FACE,{"disambiguationData":[TD([[makeQuery(id+"F0.imprint","IMPRINT",EDGE,{"disambiguationData":[TD([[subQ2,1.0]])],"derivedFrom":subQ1}),-1.0]])]});}
            var Q242;
            {var subQ0=sQuery(id+"F0.wireOp",EDGE,"E41");var subQ1=sQuery(id+"F0.wireOp",EDGE,"E4");var subQ2=makeQuery(id+"F0.imprint","INTERSECT",VERTEX,{"disambiguationData":[OD(1.0)],"derivedFrom":[subQ1,subQ0]});Q242=makeQuery(id+"F0.imprint","IMPRINT",FACE,{"disambiguationData":[TD([[makeQuery(id+"F0.imprint","IMPRINT",EDGE,{"disambiguationData":[TD([[subQ2,-1.0]])],"derivedFrom":subQ1}),1.0]])]});}
            var Q243;
            {var subQ0=sQuery(id+"F0.wireOp",EDGE,"E40");var subQ1=sQuery(id+"F0.wireOp",EDGE,"E18");var subQ2=makeQuery(id+"F0.imprint","INTERSECT",VERTEX,{"disambiguationData":[OD(1.0)],"derivedFrom":[subQ1,subQ0]});Q243=makeQuery(id+"F0.imprint","IMPRINT",FACE,{"disambiguationData":[TD([[makeQuery(id+"F0.imprint","IMPRINT",EDGE,{"disambiguationData":[TD([[subQ2,-1.0]])],"derivedFrom":subQ1}),-1.0]])]});}
            var Q244;
            {var subQ0=sQuery(id+"F0.wireOp",EDGE,"E41");var subQ1=sQuery(id+"F0.wireOp",EDGE,"E13");var subQ2=makeQuery(id+"F0.imprint","INTERSECT",VERTEX,{"disambiguationData":[OD(0.0)],"derivedFrom":[subQ1,subQ0]});Q244=makeQuery(id+"F0.imprint","IMPRINT",FACE,{"disambiguationData":[TD([[makeQuery(id+"F0.imprint","IMPRINT",EDGE,{"disambiguationData":[TD([[subQ2,1.0]])],"derivedFrom":subQ1}),-1.0]])]});}
            var Q245;
            {var subQ0=sQuery(id+"F0.wireOp",EDGE,"E42");var subQ1=sQuery(id+"F0.wireOp",EDGE,"E29");var subQ2=makeQuery(id+"F0.imprint","INTERSECT",VERTEX,{"derivedFrom":[subQ1,subQ0]});Q245=makeQuery(id+"F0.imprint","IMPRINT",FACE,{"disambiguationData":[TD([[makeQuery(id+"F0.imprint","IMPRINT",EDGE,{"disambiguationData":[TD([[subQ2,-1.0]])],"derivedFrom":subQ1}),-1.0]])]});}
            var Q246;
            {var subQ0=sQuery(id+"F0.wireOp",EDGE,"E42");var subQ1=sQuery(id+"F0.wireOp",EDGE,"E8");var subQ2=makeQuery(id+"F0.imprint","INTERSECT",VERTEX,{"derivedFrom":[subQ1,subQ0]});Q246=makeQuery(id+"F0.imprint","IMPRINT",FACE,{"disambiguationData":[TD([[makeQuery(id+"F0.imprint","IMPRINT",EDGE,{"disambiguationData":[TD([[subQ2,1.0]])],"derivedFrom":subQ1}),-1.0]])]});}
            var Q247;
            {var subQ0=sQuery(id+"F0.wireOp",EDGE,"E40");var subQ1=sQuery(id+"F0.wireOp",EDGE,"E9");var subQ2=makeQuery(id+"F0.imprint","INTERSECT",VERTEX,{"disambiguationData":[OD(0.0)],"derivedFrom":[subQ1,subQ0]});Q247=makeQuery(id+"F0.imprint","IMPRINT",FACE,{"disambiguationData":[TD([[makeQuery(id+"F0.imprint","IMPRINT",EDGE,{"disambiguationData":[TD([[subQ2,-1.0]])],"derivedFrom":subQ1}),-1.0]])]});}
            var Q248;
            {var subQ0=sQuery(id+"F0.wireOp",EDGE,"E42");var subQ1=sQuery(id+"F0.wireOp",EDGE,"E10");var subQ2=makeQuery(id+"F0.imprint","INTERSECT",VERTEX,{"derivedFrom":[subQ1,subQ0]});Q248=makeQuery(id+"F0.imprint","IMPRINT",FACE,{"disambiguationData":[TD([[makeQuery(id+"F0.imprint","IMPRINT",EDGE,{"disambiguationData":[TD([[subQ2,-1.0]])],"derivedFrom":subQ1}),-1.0]])]});}
            var Q249;
            {var subQ0=sQuery(id+"F0.wireOp",EDGE,"E42");var subQ1=sQuery(id+"F0.wireOp",EDGE,"E23");var subQ2=makeQuery(id+"F0.imprint","INTERSECT",VERTEX,{"derivedFrom":[subQ1,subQ0]});Q249=makeQuery(id+"F0.imprint","IMPRINT",FACE,{"disambiguationData":[TD([[makeQuery(id+"F0.imprint","IMPRINT",EDGE,{"disambiguationData":[TD([[subQ2,-1.0]])],"derivedFrom":subQ1}),1.0]])]});}
            var Q250;
            {var subQ0=sQuery(id+"F0.wireOp",EDGE,"E41");var subQ1=sQuery(id+"F0.wireOp",EDGE,"E1");var subQ2=makeQuery(id+"F0.imprint","INTERSECT",VERTEX,{"disambiguationData":[OD(0.0)],"derivedFrom":[subQ1,subQ0]});Q250=makeQuery(id+"F0.imprint","IMPRINT",FACE,{"disambiguationData":[TD([[makeQuery(id+"F0.imprint","IMPRINT",EDGE,{"disambiguationData":[TD([[subQ2,1.0]])],"derivedFrom":subQ1}),1.0]])]});}
            var Q251;
            {var subQ0=sQuery(id+"F0.wireOp",EDGE,"E40");var subQ1=sQuery(id+"F0.wireOp",EDGE,"E1");var subQ2=makeQuery(id+"F0.imprint","INTERSECT",VERTEX,{"disambiguationData":[OD(0.0)],"derivedFrom":[subQ1,subQ0]});Q251=makeQuery(id+"F0.imprint","IMPRINT",FACE,{"disambiguationData":[TD([[makeQuery(id+"F0.imprint","IMPRINT",EDGE,{"disambiguationData":[TD([[subQ2,-1.0]])],"derivedFrom":subQ1}),1.0]])]});}
            var Q252;
            {var subQ0=sQuery(id+"F0.wireOp",EDGE,"E41");var subQ1=sQuery(id+"F0.wireOp",EDGE,"E1");var subQ2=makeQuery(id+"F0.imprint","INTERSECT",VERTEX,{"disambiguationData":[OD(1.0)],"derivedFrom":[subQ1,subQ0]});Q252=makeQuery(id+"F0.imprint","IMPRINT",FACE,{"disambiguationData":[TD([[makeQuery(id+"F0.imprint","IMPRINT",EDGE,{"disambiguationData":[TD([[subQ2,-1.0]])],"derivedFrom":subQ1}),1.0]])]});}
            var Q253;
            {var subQ0=sQuery(id+"F0.wireOp",EDGE,"E40");var subQ1=sQuery(id+"F0.wireOp",EDGE,"E1");var subQ2=makeQuery(id+"F0.imprint","INTERSECT",VERTEX,{"disambiguationData":[OD(0.0)],"derivedFrom":[subQ1,subQ0]});Q253=makeQuery(id+"F0.imprint","IMPRINT",FACE,{"disambiguationData":[TD([[makeQuery(id+"F0.imprint","IMPRINT",EDGE,{"disambiguationData":[TD([[subQ2,-1.0]])],"derivedFrom":subQ1}),-1.0]])]});}
            var Q254;
            {var subQ0=sQuery(id+"F0.wireOp",EDGE,"E42");var subQ1=sQuery(id+"F0.wireOp",EDGE,"E1");var subQ2=makeQuery(id+"F0.imprint","INTERSECT",VERTEX,{"derivedFrom":[subQ1,subQ0]});Q254=makeQuery(id+"F0.imprint","IMPRINT",FACE,{"disambiguationData":[TD([[makeQuery(id+"F0.imprint","IMPRINT",EDGE,{"disambiguationData":[TD([[subQ2,-1.0]])],"derivedFrom":subQ1}),-1.0]])]});}
            var Q255;
            {var subQ0=sQuery(id+"F0.wireOp",EDGE,"E42");var subQ1=sQuery(id+"F0.wireOp",EDGE,"E1");var subQ2=makeQuery(id+"F0.imprint","INTERSECT",VERTEX,{"derivedFrom":[subQ1,subQ0]});Q255=makeQuery(id+"F0.imprint","IMPRINT",FACE,{"disambiguationData":[TD([[makeQuery(id+"F0.imprint","IMPRINT",EDGE,{"disambiguationData":[TD([[subQ2,1.0]])],"derivedFrom":subQ1}),-1.0]])]});}
            var Q256;
            {var subQ0=sQuery(id+"F0.wireOp",EDGE,"E40");var subQ1=sQuery(id+"F0.wireOp",EDGE,"E1");var subQ2=makeQuery(id+"F0.imprint","INTERSECT",VERTEX,{"disambiguationData":[OD(1.0)],"derivedFrom":[subQ1,subQ0]});Q256=makeQuery(id+"F0.imprint","IMPRINT",FACE,{"disambiguationData":[TD([[makeQuery(id+"F0.imprint","IMPRINT",EDGE,{"disambiguationData":[TD([[subQ2,-1.0]])],"derivedFrom":subQ1}),-1.0]])]});}
            var Q257;
            {var subQ0=sQuery(id+"F0.wireOp",EDGE,"E45");var subQ1=sQuery(id+"F0.wireOp",EDGE,"E1");var subQ2=makeQuery(id+"F0.imprint","INTERSECT",VERTEX,{"derivedFrom":[subQ1,subQ0]});Q257=makeQuery(id+"F0.imprint","IMPRINT",FACE,{"disambiguationData":[TD([[makeQuery(id+"F0.imprint","IMPRINT",EDGE,{"disambiguationData":[TD([[subQ2,-1.0]])],"derivedFrom":subQ1}),-1.0]])]});}
            var Q258;
            {var subQ0=sQuery(id+"F0.wireOp",EDGE,"E41");var subQ1=sQuery(id+"F0.wireOp",EDGE,"E1");var subQ2=makeQuery(id+"F0.imprint","INTERSECT",VERTEX,{"disambiguationData":[OD(1.0)],"derivedFrom":[subQ1,subQ0]});Q258=makeQuery(id+"F0.imprint","IMPRINT",FACE,{"disambiguationData":[TD([[makeQuery(id+"F0.imprint","IMPRINT",EDGE,{"disambiguationData":[TD([[subQ2,-1.0]])],"derivedFrom":subQ1}),-1.0]])]});}
            var Q259;
            {var subQ0=sQuery(id+"F0.wireOp",EDGE,"E41");var subQ1=sQuery(id+"F0.wireOp",EDGE,"E1");var subQ2=makeQuery(id+"F0.imprint","INTERSECT",VERTEX,{"disambiguationData":[OD(0.0)],"derivedFrom":[subQ1,subQ0]});Q259=makeQuery(id+"F0.imprint","IMPRINT",FACE,{"disambiguationData":[TD([[makeQuery(id+"F0.imprint","IMPRINT",EDGE,{"disambiguationData":[TD([[subQ2,1.0]])],"derivedFrom":subQ1}),-1.0]])]});}
            var Q260;
            {var subQ0=sQuery(id+"F0.wireOp",EDGE,"E45");var subQ1=sQuery(id+"F0.wireOp",EDGE,"E1");var subQ2=makeQuery(id+"F0.imprint","INTERSECT",VERTEX,{"derivedFrom":[subQ1,subQ0]});Q260=makeQuery(id+"F0.imprint","IMPRINT",FACE,{"disambiguationData":[TD([[makeQuery(id+"F0.imprint","IMPRINT",EDGE,{"disambiguationData":[TD([[subQ2,-1.0]])],"derivedFrom":subQ1}),1.0]])]});}
            var Q261;
            {var subQ0=sQuery(id+"F0.wireOp",EDGE,"E40");var subQ1=sQuery(id+"F0.wireOp",EDGE,"E1");var subQ2=makeQuery(id+"F0.imprint","INTERSECT",VERTEX,{"disambiguationData":[OD(1.0)],"derivedFrom":[subQ1,subQ0]});Q261=makeQuery(id+"F0.imprint","IMPRINT",FACE,{"disambiguationData":[TD([[makeQuery(id+"F0.imprint","IMPRINT",EDGE,{"disambiguationData":[TD([[subQ2,-1.0]])],"derivedFrom":subQ1}),1.0]])]});}
            var Q262;
            {var subQ0=sQuery(id+"F0.wireOp",EDGE,"E42");var subQ1=sQuery(id+"F0.wireOp",EDGE,"E1");var subQ2=makeQuery(id+"F0.imprint","INTERSECT",VERTEX,{"derivedFrom":[subQ1,subQ0]});Q262=makeQuery(id+"F0.imprint","IMPRINT",FACE,{"disambiguationData":[TD([[makeQuery(id+"F0.imprint","IMPRINT",EDGE,{"disambiguationData":[TD([[subQ2,-1.0]])],"derivedFrom":subQ1}),1.0]])]});}
            var Q263;
            {var subQ0=sQuery(id+"F0.wireOp",EDGE,"E42");var subQ1=sQuery(id+"F0.wireOp",EDGE,"E1");var subQ2=makeQuery(id+"F0.imprint","INTERSECT",VERTEX,{"derivedFrom":[subQ1,subQ0]});Q263=makeQuery(id+"F0.imprint","IMPRINT",FACE,{"disambiguationData":[TD([[makeQuery(id+"F0.imprint","IMPRINT",EDGE,{"disambiguationData":[TD([[subQ2,1.0]])],"derivedFrom":subQ1}),1.0]])]});}
            var Q264;
            {var subQ0=sQuery(id+"F0.wireOp",EDGE,"E41");var subQ1=sQuery(id+"F0.wireOp",EDGE,"E37");var subQ2=makeQuery(id+"F0.imprint","INTERSECT",VERTEX,{"disambiguationData":[OD(1.0)],"derivedFrom":[subQ1,subQ0]});Q264=makeQuery(id+"F0.imprint","IMPRINT",FACE,{"disambiguationData":[TD([[makeQuery(id+"F0.imprint","IMPRINT",EDGE,{"disambiguationData":[TD([[subQ2,-1.0]])],"derivedFrom":subQ1}),-1.0]])]});}
            var Q265;
            {var subQ0=sQuery(id+"F0.wireOp",EDGE,"E40");var subQ1=sQuery(id+"F0.wireOp",EDGE,"E36");var subQ2=makeQuery(id+"F0.imprint","INTERSECT",VERTEX,{"disambiguationData":[OD(1.0)],"derivedFrom":[subQ1,subQ0]});Q265=makeQuery(id+"F0.imprint","IMPRINT",FACE,{"disambiguationData":[TD([[makeQuery(id+"F0.imprint","IMPRINT",EDGE,{"disambiguationData":[TD([[subQ2,-1.0]])],"derivedFrom":subQ1}),-1.0]])]});}
            var Q266;
            {var subQ0=sQuery(id+"F0.wireOp",EDGE,"E42");var subQ1=sQuery(id+"F0.wireOp",EDGE,"E38");var subQ2=makeQuery(id+"F0.imprint","INTERSECT",VERTEX,{"derivedFrom":[subQ1,subQ0]});Q266=makeQuery(id+"F0.imprint","IMPRINT",FACE,{"disambiguationData":[TD([[makeQuery(id+"F0.imprint","IMPRINT",EDGE,{"disambiguationData":[TD([[subQ2,1.0]])],"derivedFrom":subQ1}),-1.0]])]});}
            var Q267;
            {var subQ0=sQuery(id+"F0.wireOp",EDGE,"E41");var subQ1=sQuery(id+"F0.wireOp",EDGE,"E36");var subQ2=makeQuery(id+"F0.imprint","INTERSECT",VERTEX,{"disambiguationData":[OD(0.0)],"derivedFrom":[subQ1,subQ0]});Q267=makeQuery(id+"F0.imprint","IMPRINT",FACE,{"disambiguationData":[TD([[makeQuery(id+"F0.imprint","IMPRINT",EDGE,{"disambiguationData":[TD([[subQ2,1.0]])],"derivedFrom":subQ1}),-1.0]])]});}
            var Q268;
            {var subQ0=sQuery(id+"F0.wireOp",EDGE,"E41");var subQ1=sQuery(id+"F0.wireOp",EDGE,"E37");var subQ2=makeQuery(id+"F0.imprint","INTERSECT",VERTEX,{"disambiguationData":[OD(0.0)],"derivedFrom":[subQ1,subQ0]});Q268=makeQuery(id+"F0.imprint","IMPRINT",FACE,{"disambiguationData":[TD([[makeQuery(id+"F0.imprint","IMPRINT",EDGE,{"disambiguationData":[TD([[subQ2,1.0]])],"derivedFrom":subQ1}),-1.0]])]});}
            var Q269;
            {var subQ0=sQuery(id+"F0.wireOp",EDGE,"E42");var subQ1=sQuery(id+"F0.wireOp",EDGE,"E37");var subQ2=makeQuery(id+"F0.imprint","INTERSECT",VERTEX,{"derivedFrom":[subQ1,subQ0]});Q269=makeQuery(id+"F0.imprint","IMPRINT",FACE,{"disambiguationData":[TD([[makeQuery(id+"F0.imprint","IMPRINT",EDGE,{"disambiguationData":[TD([[subQ2,1.0]])],"derivedFrom":subQ1}),-1.0]])]});}
            var Q270;
            {var subQ0=sQuery(id+"F0.wireOp",EDGE,"E41");var subQ1=sQuery(id+"F0.wireOp",EDGE,"E38");var subQ2=makeQuery(id+"F0.imprint","INTERSECT",VERTEX,{"disambiguationData":[OD(0.0)],"derivedFrom":[subQ1,subQ0]});Q270=makeQuery(id+"F0.imprint","IMPRINT",FACE,{"disambiguationData":[TD([[makeQuery(id+"F0.imprint","IMPRINT",EDGE,{"disambiguationData":[TD([[subQ2,1.0]])],"derivedFrom":subQ1}),-1.0]])]});}
            var Q271;
            {var subQ0=sQuery(id+"F0.wireOp",EDGE,"E41");var subQ1=sQuery(id+"F0.wireOp",EDGE,"E0");var subQ2=makeQuery(id+"F0.imprint","INTERSECT",VERTEX,{"disambiguationData":[OD(0.0)],"derivedFrom":[subQ1,subQ0]});Q271=makeQuery(id+"F0.imprint","IMPRINT",FACE,{"disambiguationData":[TD([[makeQuery(id+"F0.imprint","IMPRINT",EDGE,{"disambiguationData":[TD([[subQ2,1.0]])],"derivedFrom":subQ1}),1.0]])]});}
            var Q272;
            {var subQ0=sQuery(id+"F0.wireOp",EDGE,"E40");var subQ1=sQuery(id+"F0.wireOp",EDGE,"E0");var subQ2=makeQuery(id+"F0.imprint","INTERSECT",VERTEX,{"disambiguationData":[OD(1.0)],"derivedFrom":[subQ1,subQ0]});Q272=makeQuery(id+"F0.imprint","IMPRINT",FACE,{"disambiguationData":[TD([[makeQuery(id+"F0.imprint","IMPRINT",EDGE,{"disambiguationData":[TD([[subQ2,1.0]])],"derivedFrom":subQ1}),1.0]])]});}
            var Q273;
            {var subQ0=sQuery(id+"F0.wireOp",EDGE,"E41");var subQ1=sQuery(id+"F0.wireOp",EDGE,"E38");var subQ2=makeQuery(id+"F0.imprint","INTERSECT",VERTEX,{"disambiguationData":[OD(1.0)],"derivedFrom":[subQ1,subQ0]});Q273=makeQuery(id+"F0.imprint","IMPRINT",FACE,{"disambiguationData":[TD([[makeQuery(id+"F0.imprint","IMPRINT",EDGE,{"disambiguationData":[TD([[subQ2,-1.0]])],"derivedFrom":subQ1}),-1.0]])]});}
            var Q274;
            {var subQ0=sQuery(id+"F0.wireOp",EDGE,"E42");var subQ1=sQuery(id+"F0.wireOp",EDGE,"E36");var subQ2=makeQuery(id+"F0.imprint","INTERSECT",VERTEX,{"derivedFrom":[subQ1,subQ0]});Q274=makeQuery(id+"F0.imprint","IMPRINT",FACE,{"disambiguationData":[TD([[makeQuery(id+"F0.imprint","IMPRINT",EDGE,{"disambiguationData":[TD([[subQ2,1.0]])],"derivedFrom":subQ1}),-1.0]])]});}
            var Q275;
            {var subQ0=sQuery(id+"F0.wireOp",EDGE,"E41");var subQ1=sQuery(id+"F0.wireOp",EDGE,"E36");var subQ2=makeQuery(id+"F0.imprint","INTERSECT",VERTEX,{"disambiguationData":[OD(1.0)],"derivedFrom":[subQ1,subQ0]});Q275=makeQuery(id+"F0.imprint","IMPRINT",FACE,{"disambiguationData":[TD([[makeQuery(id+"F0.imprint","IMPRINT",EDGE,{"disambiguationData":[TD([[subQ2,-1.0]])],"derivedFrom":subQ1}),-1.0]])]});}
            var Q276;
            {var subQ0=sQuery(id+"F0.wireOp",EDGE,"E41");var subQ1=sQuery(id+"F0.wireOp",EDGE,"E0");var subQ2=makeQuery(id+"F0.imprint","INTERSECT",VERTEX,{"disambiguationData":[OD(0.0)],"derivedFrom":[subQ1,subQ0]});Q276=makeQuery(id+"F0.imprint","IMPRINT",FACE,{"disambiguationData":[TD([[makeQuery(id+"F0.imprint","IMPRINT",EDGE,{"disambiguationData":[TD([[subQ2,-1.0]])],"derivedFrom":subQ1}),1.0]])]});}
            var Q277;
            {var subQ0=sQuery(id+"F0.wireOp",EDGE,"E40");var subQ1=sQuery(id+"F0.wireOp",EDGE,"E38");var subQ2=makeQuery(id+"F0.imprint","INTERSECT",VERTEX,{"disambiguationData":[OD(1.0)],"derivedFrom":[subQ1,subQ0]});Q277=makeQuery(id+"F0.imprint","IMPRINT",FACE,{"disambiguationData":[TD([[makeQuery(id+"F0.imprint","IMPRINT",EDGE,{"disambiguationData":[TD([[subQ2,-1.0]])],"derivedFrom":subQ1}),-1.0]])]});}
            var Q278;
            {var subQ0=sQuery(id+"F0.wireOp",EDGE,"E40");var subQ1=sQuery(id+"F0.wireOp",EDGE,"E37");var subQ2=makeQuery(id+"F0.imprint","INTERSECT",VERTEX,{"disambiguationData":[OD(1.0)],"derivedFrom":[subQ1,subQ0]});Q278=makeQuery(id+"F0.imprint","IMPRINT",FACE,{"disambiguationData":[TD([[makeQuery(id+"F0.imprint","IMPRINT",EDGE,{"disambiguationData":[TD([[subQ2,-1.0]])],"derivedFrom":subQ1}),-1.0]])]});}
            var Q279;
            {var subQ0=sQuery(id+"F0.wireOp",EDGE,"E40");var subQ1=sQuery(id+"F0.wireOp",EDGE,"E0");var subQ2=makeQuery(id+"F0.imprint","INTERSECT",VERTEX,{"disambiguationData":[OD(1.0)],"derivedFrom":[subQ1,subQ0]});Q279=makeQuery(id+"F0.imprint","IMPRINT",FACE,{"disambiguationData":[TD([[makeQuery(id+"F0.imprint","IMPRINT",EDGE,{"disambiguationData":[TD([[subQ2,-1.0]])],"derivedFrom":subQ1}),1.0]])]});}
            extrude(context, id + "F1", {"entities" : qUnion([Q0, Q1, Q2, Q3, Q4, Q5, Q6, Q7, Q8, Q9, Q10, Q11, Q12, Q13, Q14, Q15, Q16, Q17, Q18, Q19, Q20, Q21, Q22, Q23, Q24, Q25, Q26, Q27, Q28, Q29, Q30, Q31, Q32, Q33, Q34, Q35, Q36, Q37, Q38, Q39, Q40, Q41, Q42, Q43, Q44, Q45, Q46, Q47, Q48, Q49, Q50, Q51, Q52, Q53, Q54, Q55, Q56, Q57, Q58, Q59, Q60, Q61, Q62, Q63, Q64, Q65, Q66, Q67, Q68, Q69, Q70, Q71, Q72, Q73, Q74, Q75, Q76, Q77, Q78, Q79, Q80, Q81, Q82, Q83, Q84, Q85, Q86, Q87, Q88, Q89, Q90, Q91, Q92, Q93, Q94, Q95, Q96, Q97, Q98, Q99, Q100, Q101, Q102, Q103, Q104, Q105, Q106, Q107, Q108, Q109, Q110, Q111, Q112, Q113, Q114, Q115, Q116, Q117, Q118, Q119, Q120, Q121, Q122, Q123, Q124, Q125, Q126, Q127, Q128, Q129, Q130, Q131, Q132, Q133, Q134, Q135, Q136, Q137, Q138, Q139, Q140, Q141, Q142, Q143, Q144, Q145, Q146, Q147, Q148, Q149, Q150, Q151, Q152, Q153, Q154, Q155, Q156, Q157, Q158, Q159, Q160, Q161, Q162, Q163, Q164, Q165, Q166, Q167, Q168, Q169, Q170, Q171, Q172, Q173, Q174, Q175, Q176, Q177, Q178, Q179, Q180, Q181, Q182, Q183, Q184, Q185, Q186, Q187, Q188, Q189, Q190, Q191, Q192, Q193, Q194, Q195, Q196, Q197, Q198, Q199, Q200, Q201, Q202, Q203, Q204, Q205, Q206, Q207, Q208, Q209, Q210, Q211, Q212, Q213, Q214, Q215, Q216, Q217, Q218, Q219, Q220, Q221, Q222, Q223, Q224, Q225, Q226, Q227, Q228, Q229, Q230, Q231, Q232, Q233, Q234, Q235, Q236, Q237, Q238, Q239, Q240, Q241, Q242, Q243, Q244, Q245, Q246, Q247, Q248, Q249, Q250, Q251, Q252, Q253, Q254, Q255, Q256, Q257, Q258, Q259, Q260, Q261, Q262, Q263, Q264, Q265, Q266, Q267, Q268, Q269, Q270, Q271, Q272, Q273, Q274, Q275, Q276, Q277, Q278, Q279]), "depth" : 25 * mm, "offsetDistance" : 25 * mm});
        }
        {
            var Q0;
            {var subQ0=sQuery(id+"F0.wireOp",EDGE,"E41");var subQ1=sQuery(id+"F0.wireOp",EDGE,"E1");var subQ2=makeQuery(id+"F0.imprint","INTERSECT",VERTEX,{"disambiguationData":[OD(1.0)],"derivedFrom":[subQ1,subQ0]});Q0=makeQuery(id+"F0.imprint","IMPRINT",FACE,{"disambiguationData":[TD([[makeQuery(id+"F0.imprint","IMPRINT",EDGE,{"disambiguationData":[TD([[subQ2,-1.0]])],"derivedFrom":subQ1}),1.0]])]});}
            var Q1;
            {var subQ0=sQuery(id+"F0.wireOp",EDGE,"E40");var subQ1=sQuery(id+"F0.wireOp",EDGE,"E1");var subQ2=makeQuery(id+"F0.imprint","INTERSECT",VERTEX,{"disambiguationData":[OD(0.0)],"derivedFrom":[subQ1,subQ0]});Q1=makeQuery(id+"F0.imprint","IMPRINT",FACE,{"disambiguationData":[TD([[makeQuery(id+"F0.imprint","IMPRINT",EDGE,{"disambiguationData":[TD([[subQ2,-1.0]])],"derivedFrom":subQ1}),1.0]])]});}
            var Q2;
            {var subQ0=sQuery(id+"F0.wireOp",EDGE,"E42");var subQ1=sQuery(id+"F0.wireOp",EDGE,"E1");var subQ2=makeQuery(id+"F0.imprint","INTERSECT",VERTEX,{"derivedFrom":[subQ1,subQ0]});Q2=makeQuery(id+"F0.imprint","IMPRINT",FACE,{"disambiguationData":[TD([[makeQuery(id+"F0.imprint","IMPRINT",EDGE,{"disambiguationData":[TD([[subQ2,-1.0]])],"derivedFrom":subQ1}),1.0]])]});}
            var Q3;
            {var subQ0=sQuery(id+"F0.wireOp",EDGE,"E42");var subQ1=sQuery(id+"F0.wireOp",EDGE,"E1");var subQ2=makeQuery(id+"F0.imprint","INTERSECT",VERTEX,{"derivedFrom":[subQ1,subQ0]});Q3=makeQuery(id+"F0.imprint","IMPRINT",FACE,{"disambiguationData":[TD([[makeQuery(id+"F0.imprint","IMPRINT",EDGE,{"disambiguationData":[TD([[subQ2,1.0]])],"derivedFrom":subQ1}),1.0]])]});}
            var Q4;
            {var subQ0=sQuery(id+"F0.wireOp",EDGE,"E41");var subQ1=sQuery(id+"F0.wireOp",EDGE,"E1");var subQ2=makeQuery(id+"F0.imprint","INTERSECT",VERTEX,{"disambiguationData":[OD(0.0)],"derivedFrom":[subQ1,subQ0]});Q4=makeQuery(id+"F0.imprint","IMPRINT",FACE,{"disambiguationData":[TD([[makeQuery(id+"F0.imprint","IMPRINT",EDGE,{"disambiguationData":[TD([[subQ2,1.0]])],"derivedFrom":subQ1}),1.0]])]});}
            var Q5;
            {var subQ0=sQuery(id+"F0.wireOp",EDGE,"E40");var subQ1=sQuery(id+"F0.wireOp",EDGE,"E1");var subQ2=makeQuery(id+"F0.imprint","INTERSECT",VERTEX,{"disambiguationData":[OD(1.0)],"derivedFrom":[subQ1,subQ0]});Q5=makeQuery(id+"F0.imprint","IMPRINT",FACE,{"disambiguationData":[TD([[makeQuery(id+"F0.imprint","IMPRINT",EDGE,{"disambiguationData":[TD([[subQ2,-1.0]])],"derivedFrom":subQ1}),1.0]])]});}
            var Q6;
            {var subQ0=sQuery(id+"F0.wireOp",EDGE,"E45");var subQ1=sQuery(id+"F0.wireOp",EDGE,"E1");var subQ2=makeQuery(id+"F0.imprint","INTERSECT",VERTEX,{"derivedFrom":[subQ1,subQ0]});Q6=makeQuery(id+"F0.imprint","IMPRINT",FACE,{"disambiguationData":[TD([[makeQuery(id+"F0.imprint","IMPRINT",EDGE,{"disambiguationData":[TD([[subQ2,-1.0]])],"derivedFrom":subQ1}),1.0]])]});}
            var Q7;
            {var subQ0=sQuery(id+"F0.wireOp",EDGE,"E45");var subQ1=sQuery(id+"F0.wireOp",EDGE,"E2");var subQ2=makeQuery(id+"F0.imprint","INTERSECT",VERTEX,{"derivedFrom":[subQ1,subQ0]});Q7=makeQuery(id+"F0.imprint","IMPRINT",FACE,{"disambiguationData":[TD([[makeQuery(id+"F0.imprint","IMPRINT",EDGE,{"disambiguationData":[TD([[subQ2,-1.0]])],"derivedFrom":subQ1}),-1.0]])]});}
            var Q8;
            {var subQ0=sQuery(id+"F0.wireOp",EDGE,"E40");var subQ1=sQuery(id+"F0.wireOp",EDGE,"E2");var subQ2=makeQuery(id+"F0.imprint","INTERSECT",VERTEX,{"disambiguationData":[OD(0.0)],"derivedFrom":[subQ1,subQ0]});Q8=makeQuery(id+"F0.imprint","IMPRINT",FACE,{"disambiguationData":[TD([[makeQuery(id+"F0.imprint","IMPRINT",EDGE,{"disambiguationData":[TD([[subQ2,-1.0]])],"derivedFrom":subQ1}),-1.0]])]});}
            var Q9;
            {var subQ0=sQuery(id+"F0.wireOp",EDGE,"E41");var subQ1=sQuery(id+"F0.wireOp",EDGE,"E2");var subQ2=makeQuery(id+"F0.imprint","INTERSECT",VERTEX,{"disambiguationData":[OD(1.0)],"derivedFrom":[subQ1,subQ0]});Q9=makeQuery(id+"F0.imprint","IMPRINT",FACE,{"disambiguationData":[TD([[makeQuery(id+"F0.imprint","IMPRINT",EDGE,{"disambiguationData":[TD([[subQ2,-1.0]])],"derivedFrom":subQ1}),-1.0]])]});}
            var Q10;
            {var subQ0=sQuery(id+"F0.wireOp",EDGE,"E40");var subQ1=sQuery(id+"F0.wireOp",EDGE,"E2");var subQ2=makeQuery(id+"F0.imprint","INTERSECT",VERTEX,{"disambiguationData":[OD(1.0)],"derivedFrom":[subQ1,subQ0]});Q10=makeQuery(id+"F0.imprint","IMPRINT",FACE,{"disambiguationData":[TD([[makeQuery(id+"F0.imprint","IMPRINT",EDGE,{"disambiguationData":[TD([[subQ2,-1.0]])],"derivedFrom":subQ1}),-1.0]])]});}
            var Q11;
            {var subQ0=sQuery(id+"F0.wireOp",EDGE,"E41");var subQ1=sQuery(id+"F0.wireOp",EDGE,"E2");var subQ2=makeQuery(id+"F0.imprint","INTERSECT",VERTEX,{"disambiguationData":[OD(0.0)],"derivedFrom":[subQ1,subQ0]});Q11=makeQuery(id+"F0.imprint","IMPRINT",FACE,{"disambiguationData":[TD([[makeQuery(id+"F0.imprint","IMPRINT",EDGE,{"disambiguationData":[TD([[subQ2,1.0]])],"derivedFrom":subQ1}),-1.0]])]});}
            var Q12;
            {var subQ0=sQuery(id+"F0.wireOp",EDGE,"E42");var subQ1=sQuery(id+"F0.wireOp",EDGE,"E2");var subQ2=makeQuery(id+"F0.imprint","INTERSECT",VERTEX,{"derivedFrom":[subQ1,subQ0]});Q12=makeQuery(id+"F0.imprint","IMPRINT",FACE,{"disambiguationData":[TD([[makeQuery(id+"F0.imprint","IMPRINT",EDGE,{"disambiguationData":[TD([[subQ2,1.0]])],"derivedFrom":subQ1}),-1.0]])]});}
            var Q13;
            {var subQ0=sQuery(id+"F0.wireOp",EDGE,"E42");var subQ1=sQuery(id+"F0.wireOp",EDGE,"E2");var subQ2=makeQuery(id+"F0.imprint","INTERSECT",VERTEX,{"derivedFrom":[subQ1,subQ0]});Q13=makeQuery(id+"F0.imprint","IMPRINT",FACE,{"disambiguationData":[TD([[makeQuery(id+"F0.imprint","IMPRINT",EDGE,{"disambiguationData":[TD([[subQ2,-1.0]])],"derivedFrom":subQ1}),-1.0]])]});}
            var Q14;
            {var subQ0=sQuery(id+"F0.wireOp",EDGE,"E40");var subQ1=sQuery(id+"F0.wireOp",EDGE,"E5");var subQ2=makeQuery(id+"F0.imprint","INTERSECT",VERTEX,{"disambiguationData":[OD(0.0)],"derivedFrom":[subQ1,subQ0]});Q14=makeQuery(id+"F0.imprint","IMPRINT",FACE,{"disambiguationData":[TD([[makeQuery(id+"F0.imprint","IMPRINT",EDGE,{"disambiguationData":[TD([[subQ2,-1.0]])],"derivedFrom":subQ1}),-1.0]])]});}
            var Q15;
            {var subQ0=sQuery(id+"F0.wireOp",EDGE,"E45");var subQ1=sQuery(id+"F0.wireOp",EDGE,"E5");var subQ2=makeQuery(id+"F0.imprint","INTERSECT",VERTEX,{"derivedFrom":[subQ1,subQ0]});Q15=makeQuery(id+"F0.imprint","IMPRINT",FACE,{"disambiguationData":[TD([[makeQuery(id+"F0.imprint","IMPRINT",EDGE,{"disambiguationData":[TD([[subQ2,-1.0]])],"derivedFrom":subQ1}),-1.0]])]});}
            var Q16;
            {var subQ0=sQuery(id+"F0.wireOp",EDGE,"E41");var subQ1=sQuery(id+"F0.wireOp",EDGE,"E5");var subQ2=makeQuery(id+"F0.imprint","INTERSECT",VERTEX,{"disambiguationData":[OD(1.0)],"derivedFrom":[subQ1,subQ0]});Q16=makeQuery(id+"F0.imprint","IMPRINT",FACE,{"disambiguationData":[TD([[makeQuery(id+"F0.imprint","IMPRINT",EDGE,{"disambiguationData":[TD([[subQ2,-1.0]])],"derivedFrom":subQ1}),-1.0]])]});}
            var Q17;
            {var subQ0=sQuery(id+"F0.wireOp",EDGE,"E40");var subQ1=sQuery(id+"F0.wireOp",EDGE,"E5");var subQ2=makeQuery(id+"F0.imprint","INTERSECT",VERTEX,{"disambiguationData":[OD(1.0)],"derivedFrom":[subQ1,subQ0]});Q17=makeQuery(id+"F0.imprint","IMPRINT",FACE,{"disambiguationData":[TD([[makeQuery(id+"F0.imprint","IMPRINT",EDGE,{"disambiguationData":[TD([[subQ2,-1.0]])],"derivedFrom":subQ1}),-1.0]])]});}
            var Q18;
            {var subQ0=sQuery(id+"F0.wireOp",EDGE,"E41");var subQ1=sQuery(id+"F0.wireOp",EDGE,"E5");var subQ2=makeQuery(id+"F0.imprint","INTERSECT",VERTEX,{"disambiguationData":[OD(0.0)],"derivedFrom":[subQ1,subQ0]});Q18=makeQuery(id+"F0.imprint","IMPRINT",FACE,{"disambiguationData":[TD([[makeQuery(id+"F0.imprint","IMPRINT",EDGE,{"disambiguationData":[TD([[subQ2,1.0]])],"derivedFrom":subQ1}),-1.0]])]});}
            var Q19;
            {var subQ0=sQuery(id+"F0.wireOp",EDGE,"E42");var subQ1=sQuery(id+"F0.wireOp",EDGE,"E5");var subQ2=makeQuery(id+"F0.imprint","INTERSECT",VERTEX,{"derivedFrom":[subQ1,subQ0]});Q19=makeQuery(id+"F0.imprint","IMPRINT",FACE,{"disambiguationData":[TD([[makeQuery(id+"F0.imprint","IMPRINT",EDGE,{"disambiguationData":[TD([[subQ2,1.0]])],"derivedFrom":subQ1}),-1.0]])]});}
            var Q20;
            {var subQ0=sQuery(id+"F0.wireOp",EDGE,"E42");var subQ1=sQuery(id+"F0.wireOp",EDGE,"E5");var subQ2=makeQuery(id+"F0.imprint","INTERSECT",VERTEX,{"derivedFrom":[subQ1,subQ0]});Q20=makeQuery(id+"F0.imprint","IMPRINT",FACE,{"disambiguationData":[TD([[makeQuery(id+"F0.imprint","IMPRINT",EDGE,{"disambiguationData":[TD([[subQ2,-1.0]])],"derivedFrom":subQ1}),-1.0]])]});}
            var Q21;
            {var subQ0=sQuery(id+"F0.wireOp",EDGE,"E45");var subQ1=sQuery(id+"F0.wireOp",EDGE,"E4");var subQ2=makeQuery(id+"F0.imprint","INTERSECT",VERTEX,{"derivedFrom":[subQ1,subQ0]});Q21=makeQuery(id+"F0.imprint","IMPRINT",FACE,{"disambiguationData":[TD([[makeQuery(id+"F0.imprint","IMPRINT",EDGE,{"disambiguationData":[TD([[subQ2,-1.0]])],"derivedFrom":subQ1}),-1.0]])]});}
            var Q22;
            {var subQ0=sQuery(id+"F0.wireOp",EDGE,"E45");var subQ1=sQuery(id+"F0.wireOp",EDGE,"E8");var subQ2=makeQuery(id+"F0.imprint","INTERSECT",VERTEX,{"derivedFrom":[subQ1,subQ0]});Q22=makeQuery(id+"F0.imprint","IMPRINT",FACE,{"disambiguationData":[TD([[makeQuery(id+"F0.imprint","IMPRINT",EDGE,{"disambiguationData":[TD([[subQ2,-1.0]])],"derivedFrom":subQ1}),-1.0]])]});}
            var Q23;
            {var subQ0=sQuery(id+"F0.wireOp",EDGE,"E45");var subQ1=sQuery(id+"F0.wireOp",EDGE,"E10");var subQ2=makeQuery(id+"F0.imprint","INTERSECT",VERTEX,{"derivedFrom":[subQ1,subQ0]});Q23=makeQuery(id+"F0.imprint","IMPRINT",FACE,{"disambiguationData":[TD([[makeQuery(id+"F0.imprint","IMPRINT",EDGE,{"disambiguationData":[TD([[subQ2,-1.0]])],"derivedFrom":subQ1}),-1.0]])]});}
            var Q24;
            {var subQ0=sQuery(id+"F0.wireOp",EDGE,"E45");var subQ1=sQuery(id+"F0.wireOp",EDGE,"E12");var subQ2=makeQuery(id+"F0.imprint","INTERSECT",VERTEX,{"derivedFrom":[subQ1,subQ0]});Q24=makeQuery(id+"F0.imprint","IMPRINT",FACE,{"disambiguationData":[TD([[makeQuery(id+"F0.imprint","IMPRINT",EDGE,{"disambiguationData":[TD([[subQ2,-1.0]])],"derivedFrom":subQ1}),-1.0]])]});}
            var Q25;
            {var subQ0=sQuery(id+"F0.wireOp",EDGE,"E45");var subQ1=sQuery(id+"F0.wireOp",EDGE,"E14");var subQ2=makeQuery(id+"F0.imprint","INTERSECT",VERTEX,{"derivedFrom":[subQ1,subQ0]});Q25=makeQuery(id+"F0.imprint","IMPRINT",FACE,{"disambiguationData":[TD([[makeQuery(id+"F0.imprint","IMPRINT",EDGE,{"disambiguationData":[TD([[subQ2,-1.0]])],"derivedFrom":subQ1}),-1.0]])]});}
            var Q26;
            {var subQ0=sQuery(id+"F0.wireOp",EDGE,"E45");var subQ1=sQuery(id+"F0.wireOp",EDGE,"E16");var subQ2=makeQuery(id+"F0.imprint","INTERSECT",VERTEX,{"derivedFrom":[subQ1,subQ0]});Q26=makeQuery(id+"F0.imprint","IMPRINT",FACE,{"disambiguationData":[TD([[makeQuery(id+"F0.imprint","IMPRINT",EDGE,{"disambiguationData":[TD([[subQ2,-1.0]])],"derivedFrom":subQ1}),-1.0]])]});}
            var Q27;
            {var subQ0=sQuery(id+"F0.wireOp",EDGE,"E45");var subQ1=sQuery(id+"F0.wireOp",EDGE,"E17");var subQ2=makeQuery(id+"F0.imprint","INTERSECT",VERTEX,{"derivedFrom":[subQ1,subQ0]});Q27=makeQuery(id+"F0.imprint","IMPRINT",FACE,{"disambiguationData":[TD([[makeQuery(id+"F0.imprint","IMPRINT",EDGE,{"disambiguationData":[TD([[subQ2,-1.0]])],"derivedFrom":subQ1}),-1.0]])]});}
            var Q28;
            {var subQ0=sQuery(id+"F0.wireOp",EDGE,"E45");var subQ1=sQuery(id+"F0.wireOp",EDGE,"E18");var subQ2=makeQuery(id+"F0.imprint","INTERSECT",VERTEX,{"derivedFrom":[subQ1,subQ0]});Q28=makeQuery(id+"F0.imprint","IMPRINT",FACE,{"disambiguationData":[TD([[makeQuery(id+"F0.imprint","IMPRINT",EDGE,{"disambiguationData":[TD([[subQ2,-1.0]])],"derivedFrom":subQ1}),-1.0]])]});}
            var Q29;
            {var subQ0=sQuery(id+"F0.wireOp",EDGE,"E45");var subQ1=sQuery(id+"F0.wireOp",EDGE,"E20");var subQ2=makeQuery(id+"F0.imprint","INTERSECT",VERTEX,{"derivedFrom":[subQ1,subQ0]});Q29=makeQuery(id+"F0.imprint","IMPRINT",FACE,{"disambiguationData":[TD([[makeQuery(id+"F0.imprint","IMPRINT",EDGE,{"disambiguationData":[TD([[subQ2,-1.0]])],"derivedFrom":subQ1}),-1.0]])]});}
            var Q30;
            {var subQ0=sQuery(id+"F0.wireOp",EDGE,"E40");var subQ1=sQuery(id+"F0.wireOp",EDGE,"E4");var subQ2=makeQuery(id+"F0.imprint","INTERSECT",VERTEX,{"disambiguationData":[OD(0.0)],"derivedFrom":[subQ1,subQ0]});Q30=makeQuery(id+"F0.imprint","IMPRINT",FACE,{"disambiguationData":[TD([[makeQuery(id+"F0.imprint","IMPRINT",EDGE,{"disambiguationData":[TD([[subQ2,-1.0]])],"derivedFrom":subQ1}),-1.0]])]});}
            var Q31;
            {var subQ0=sQuery(id+"F0.wireOp",EDGE,"E40");var subQ1=sQuery(id+"F0.wireOp",EDGE,"E8");var subQ2=makeQuery(id+"F0.imprint","INTERSECT",VERTEX,{"disambiguationData":[OD(0.0)],"derivedFrom":[subQ1,subQ0]});Q31=makeQuery(id+"F0.imprint","IMPRINT",FACE,{"disambiguationData":[TD([[makeQuery(id+"F0.imprint","IMPRINT",EDGE,{"disambiguationData":[TD([[subQ2,-1.0]])],"derivedFrom":subQ1}),-1.0]])]});}
            var Q32;
            {var subQ0=sQuery(id+"F0.wireOp",EDGE,"E40");var subQ1=sQuery(id+"F0.wireOp",EDGE,"E10");var subQ2=makeQuery(id+"F0.imprint","INTERSECT",VERTEX,{"disambiguationData":[OD(0.0)],"derivedFrom":[subQ1,subQ0]});Q32=makeQuery(id+"F0.imprint","IMPRINT",FACE,{"disambiguationData":[TD([[makeQuery(id+"F0.imprint","IMPRINT",EDGE,{"disambiguationData":[TD([[subQ2,-1.0]])],"derivedFrom":subQ1}),-1.0]])]});}
            var Q33;
            {var subQ0=sQuery(id+"F0.wireOp",EDGE,"E40");var subQ1=sQuery(id+"F0.wireOp",EDGE,"E12");var subQ2=makeQuery(id+"F0.imprint","INTERSECT",VERTEX,{"disambiguationData":[OD(0.0)],"derivedFrom":[subQ1,subQ0]});Q33=makeQuery(id+"F0.imprint","IMPRINT",FACE,{"disambiguationData":[TD([[makeQuery(id+"F0.imprint","IMPRINT",EDGE,{"disambiguationData":[TD([[subQ2,-1.0]])],"derivedFrom":subQ1}),-1.0]])]});}
            var Q34;
            {var subQ0=sQuery(id+"F0.wireOp",EDGE,"E40");var subQ1=sQuery(id+"F0.wireOp",EDGE,"E14");var subQ2=makeQuery(id+"F0.imprint","INTERSECT",VERTEX,{"disambiguationData":[OD(0.0)],"derivedFrom":[subQ1,subQ0]});Q34=makeQuery(id+"F0.imprint","IMPRINT",FACE,{"disambiguationData":[TD([[makeQuery(id+"F0.imprint","IMPRINT",EDGE,{"disambiguationData":[TD([[subQ2,-1.0]])],"derivedFrom":subQ1}),-1.0]])]});}
            var Q35;
            {var subQ0=sQuery(id+"F0.wireOp",EDGE,"E40");var subQ1=sQuery(id+"F0.wireOp",EDGE,"E16");var subQ2=makeQuery(id+"F0.imprint","INTERSECT",VERTEX,{"disambiguationData":[OD(0.0)],"derivedFrom":[subQ1,subQ0]});Q35=makeQuery(id+"F0.imprint","IMPRINT",FACE,{"disambiguationData":[TD([[makeQuery(id+"F0.imprint","IMPRINT",EDGE,{"disambiguationData":[TD([[subQ2,-1.0]])],"derivedFrom":subQ1}),-1.0]])]});}
            var Q36;
            {var subQ0=sQuery(id+"F0.wireOp",EDGE,"E40");var subQ1=sQuery(id+"F0.wireOp",EDGE,"E17");var subQ2=makeQuery(id+"F0.imprint","INTERSECT",VERTEX,{"disambiguationData":[OD(0.0)],"derivedFrom":[subQ1,subQ0]});Q36=makeQuery(id+"F0.imprint","IMPRINT",FACE,{"disambiguationData":[TD([[makeQuery(id+"F0.imprint","IMPRINT",EDGE,{"disambiguationData":[TD([[subQ2,-1.0]])],"derivedFrom":subQ1}),-1.0]])]});}
            var Q37;
            {var subQ0=sQuery(id+"F0.wireOp",EDGE,"E40");var subQ1=sQuery(id+"F0.wireOp",EDGE,"E18");var subQ2=makeQuery(id+"F0.imprint","INTERSECT",VERTEX,{"disambiguationData":[OD(0.0)],"derivedFrom":[subQ1,subQ0]});Q37=makeQuery(id+"F0.imprint","IMPRINT",FACE,{"disambiguationData":[TD([[makeQuery(id+"F0.imprint","IMPRINT",EDGE,{"disambiguationData":[TD([[subQ2,-1.0]])],"derivedFrom":subQ1}),-1.0]])]});}
            var Q38;
            {var subQ0=sQuery(id+"F0.wireOp",EDGE,"E40");var subQ1=sQuery(id+"F0.wireOp",EDGE,"E20");var subQ2=makeQuery(id+"F0.imprint","INTERSECT",VERTEX,{"disambiguationData":[OD(0.0)],"derivedFrom":[subQ1,subQ0]});Q38=makeQuery(id+"F0.imprint","IMPRINT",FACE,{"disambiguationData":[TD([[makeQuery(id+"F0.imprint","IMPRINT",EDGE,{"disambiguationData":[TD([[subQ2,-1.0]])],"derivedFrom":subQ1}),-1.0]])]});}
            var Q39;
            {var subQ0=sQuery(id+"F0.wireOp",EDGE,"E41");var subQ1=sQuery(id+"F0.wireOp",EDGE,"E4");var subQ2=makeQuery(id+"F0.imprint","INTERSECT",VERTEX,{"disambiguationData":[OD(1.0)],"derivedFrom":[subQ1,subQ0]});Q39=makeQuery(id+"F0.imprint","IMPRINT",FACE,{"disambiguationData":[TD([[makeQuery(id+"F0.imprint","IMPRINT",EDGE,{"disambiguationData":[TD([[subQ2,-1.0]])],"derivedFrom":subQ1}),-1.0]])]});}
            var Q40;
            {var subQ0=sQuery(id+"F0.wireOp",EDGE,"E40");var subQ1=sQuery(id+"F0.wireOp",EDGE,"E4");var subQ2=makeQuery(id+"F0.imprint","INTERSECT",VERTEX,{"disambiguationData":[OD(1.0)],"derivedFrom":[subQ1,subQ0]});Q40=makeQuery(id+"F0.imprint","IMPRINT",FACE,{"disambiguationData":[TD([[makeQuery(id+"F0.imprint","IMPRINT",EDGE,{"disambiguationData":[TD([[subQ2,-1.0]])],"derivedFrom":subQ1}),-1.0]])]});}
            var Q41;
            {var subQ0=sQuery(id+"F0.wireOp",EDGE,"E41");var subQ1=sQuery(id+"F0.wireOp",EDGE,"E4");var subQ2=makeQuery(id+"F0.imprint","INTERSECT",VERTEX,{"disambiguationData":[OD(0.0)],"derivedFrom":[subQ1,subQ0]});Q41=makeQuery(id+"F0.imprint","IMPRINT",FACE,{"disambiguationData":[TD([[makeQuery(id+"F0.imprint","IMPRINT",EDGE,{"disambiguationData":[TD([[subQ2,1.0]])],"derivedFrom":subQ1}),-1.0]])]});}
            var Q42;
            {var subQ0=sQuery(id+"F0.wireOp",EDGE,"E42");var subQ1=sQuery(id+"F0.wireOp",EDGE,"E4");var subQ2=makeQuery(id+"F0.imprint","INTERSECT",VERTEX,{"derivedFrom":[subQ1,subQ0]});Q42=makeQuery(id+"F0.imprint","IMPRINT",FACE,{"disambiguationData":[TD([[makeQuery(id+"F0.imprint","IMPRINT",EDGE,{"disambiguationData":[TD([[subQ2,1.0]])],"derivedFrom":subQ1}),-1.0]])]});}
            var Q43;
            {var subQ0=sQuery(id+"F0.wireOp",EDGE,"E42");var subQ1=sQuery(id+"F0.wireOp",EDGE,"E4");var subQ2=makeQuery(id+"F0.imprint","INTERSECT",VERTEX,{"derivedFrom":[subQ1,subQ0]});Q43=makeQuery(id+"F0.imprint","IMPRINT",FACE,{"disambiguationData":[TD([[makeQuery(id+"F0.imprint","IMPRINT",EDGE,{"disambiguationData":[TD([[subQ2,-1.0]])],"derivedFrom":subQ1}),-1.0]])]});}
            var Q44;
            {var subQ0=sQuery(id+"F0.wireOp",EDGE,"E42");var subQ1=sQuery(id+"F0.wireOp",EDGE,"E8");var subQ2=makeQuery(id+"F0.imprint","INTERSECT",VERTEX,{"derivedFrom":[subQ1,subQ0]});Q44=makeQuery(id+"F0.imprint","IMPRINT",FACE,{"disambiguationData":[TD([[makeQuery(id+"F0.imprint","IMPRINT",EDGE,{"disambiguationData":[TD([[subQ2,-1.0]])],"derivedFrom":subQ1}),-1.0]])]});}
            var Q45;
            {var subQ0=sQuery(id+"F0.wireOp",EDGE,"E42");var subQ1=sQuery(id+"F0.wireOp",EDGE,"E10");var subQ2=makeQuery(id+"F0.imprint","INTERSECT",VERTEX,{"derivedFrom":[subQ1,subQ0]});Q45=makeQuery(id+"F0.imprint","IMPRINT",FACE,{"disambiguationData":[TD([[makeQuery(id+"F0.imprint","IMPRINT",EDGE,{"disambiguationData":[TD([[subQ2,-1.0]])],"derivedFrom":subQ1}),-1.0]])]});}
            var Q46;
            {var subQ0=sQuery(id+"F0.wireOp",EDGE,"E42");var subQ1=sQuery(id+"F0.wireOp",EDGE,"E12");var subQ2=makeQuery(id+"F0.imprint","INTERSECT",VERTEX,{"derivedFrom":[subQ1,subQ0]});Q46=makeQuery(id+"F0.imprint","IMPRINT",FACE,{"disambiguationData":[TD([[makeQuery(id+"F0.imprint","IMPRINT",EDGE,{"disambiguationData":[TD([[subQ2,-1.0]])],"derivedFrom":subQ1}),-1.0]])]});}
            var Q47;
            {var subQ0=sQuery(id+"F0.wireOp",EDGE,"E42");var subQ1=sQuery(id+"F0.wireOp",EDGE,"E14");var subQ2=makeQuery(id+"F0.imprint","INTERSECT",VERTEX,{"derivedFrom":[subQ1,subQ0]});Q47=makeQuery(id+"F0.imprint","IMPRINT",FACE,{"disambiguationData":[TD([[makeQuery(id+"F0.imprint","IMPRINT",EDGE,{"disambiguationData":[TD([[subQ2,-1.0]])],"derivedFrom":subQ1}),-1.0]])]});}
            var Q48;
            {var subQ0=sQuery(id+"F0.wireOp",EDGE,"E42");var subQ1=sQuery(id+"F0.wireOp",EDGE,"E17");var subQ2=makeQuery(id+"F0.imprint","INTERSECT",VERTEX,{"derivedFrom":[subQ1,subQ0]});Q48=makeQuery(id+"F0.imprint","IMPRINT",FACE,{"disambiguationData":[TD([[makeQuery(id+"F0.imprint","IMPRINT",EDGE,{"disambiguationData":[TD([[subQ2,-1.0]])],"derivedFrom":subQ1}),-1.0]])]});}
            var Q49;
            {var subQ0=sQuery(id+"F0.wireOp",EDGE,"E42");var subQ1=sQuery(id+"F0.wireOp",EDGE,"E18");var subQ2=makeQuery(id+"F0.imprint","INTERSECT",VERTEX,{"derivedFrom":[subQ1,subQ0]});Q49=makeQuery(id+"F0.imprint","IMPRINT",FACE,{"disambiguationData":[TD([[makeQuery(id+"F0.imprint","IMPRINT",EDGE,{"disambiguationData":[TD([[subQ2,-1.0]])],"derivedFrom":subQ1}),-1.0]])]});}
            var Q50;
            {var subQ0=sQuery(id+"F0.wireOp",EDGE,"E42");var subQ1=sQuery(id+"F0.wireOp",EDGE,"E20");var subQ2=makeQuery(id+"F0.imprint","INTERSECT",VERTEX,{"derivedFrom":[subQ1,subQ0]});Q50=makeQuery(id+"F0.imprint","IMPRINT",FACE,{"disambiguationData":[TD([[makeQuery(id+"F0.imprint","IMPRINT",EDGE,{"disambiguationData":[TD([[subQ2,-1.0]])],"derivedFrom":subQ1}),-1.0]])]});}
            var Q51;
            {var subQ0=sQuery(id+"F0.wireOp",EDGE,"E41");var subQ1=sQuery(id+"F0.wireOp",EDGE,"E20");var subQ2=makeQuery(id+"F0.imprint","INTERSECT",VERTEX,{"disambiguationData":[OD(1.0)],"derivedFrom":[subQ1,subQ0]});Q51=makeQuery(id+"F0.imprint","IMPRINT",FACE,{"disambiguationData":[TD([[makeQuery(id+"F0.imprint","IMPRINT",EDGE,{"disambiguationData":[TD([[subQ2,-1.0]])],"derivedFrom":subQ1}),-1.0]])]});}
            var Q52;
            {var subQ0=sQuery(id+"F0.wireOp",EDGE,"E41");var subQ1=sQuery(id+"F0.wireOp",EDGE,"E18");var subQ2=makeQuery(id+"F0.imprint","INTERSECT",VERTEX,{"disambiguationData":[OD(1.0)],"derivedFrom":[subQ1,subQ0]});Q52=makeQuery(id+"F0.imprint","IMPRINT",FACE,{"disambiguationData":[TD([[makeQuery(id+"F0.imprint","IMPRINT",EDGE,{"disambiguationData":[TD([[subQ2,-1.0]])],"derivedFrom":subQ1}),-1.0]])]});}
            var Q53;
            {var subQ0=sQuery(id+"F0.wireOp",EDGE,"E41");var subQ1=sQuery(id+"F0.wireOp",EDGE,"E17");var subQ2=makeQuery(id+"F0.imprint","INTERSECT",VERTEX,{"disambiguationData":[OD(1.0)],"derivedFrom":[subQ1,subQ0]});Q53=makeQuery(id+"F0.imprint","IMPRINT",FACE,{"disambiguationData":[TD([[makeQuery(id+"F0.imprint","IMPRINT",EDGE,{"disambiguationData":[TD([[subQ2,-1.0]])],"derivedFrom":subQ1}),-1.0]])]});}
            var Q54;
            {var subQ0=sQuery(id+"F0.wireOp",EDGE,"E41");var subQ1=sQuery(id+"F0.wireOp",EDGE,"E16");var subQ2=makeQuery(id+"F0.imprint","INTERSECT",VERTEX,{"disambiguationData":[OD(1.0)],"derivedFrom":[subQ1,subQ0]});Q54=makeQuery(id+"F0.imprint","IMPRINT",FACE,{"disambiguationData":[TD([[makeQuery(id+"F0.imprint","IMPRINT",EDGE,{"disambiguationData":[TD([[subQ2,-1.0]])],"derivedFrom":subQ1}),-1.0]])]});}
            var Q55;
            {var subQ0=sQuery(id+"F0.wireOp",EDGE,"E41");var subQ1=sQuery(id+"F0.wireOp",EDGE,"E14");var subQ2=makeQuery(id+"F0.imprint","INTERSECT",VERTEX,{"disambiguationData":[OD(1.0)],"derivedFrom":[subQ1,subQ0]});Q55=makeQuery(id+"F0.imprint","IMPRINT",FACE,{"disambiguationData":[TD([[makeQuery(id+"F0.imprint","IMPRINT",EDGE,{"disambiguationData":[TD([[subQ2,-1.0]])],"derivedFrom":subQ1}),-1.0]])]});}
            var Q56;
            {var subQ0=sQuery(id+"F0.wireOp",EDGE,"E41");var subQ1=sQuery(id+"F0.wireOp",EDGE,"E12");var subQ2=makeQuery(id+"F0.imprint","INTERSECT",VERTEX,{"disambiguationData":[OD(1.0)],"derivedFrom":[subQ1,subQ0]});Q56=makeQuery(id+"F0.imprint","IMPRINT",FACE,{"disambiguationData":[TD([[makeQuery(id+"F0.imprint","IMPRINT",EDGE,{"disambiguationData":[TD([[subQ2,-1.0]])],"derivedFrom":subQ1}),-1.0]])]});}
            var Q57;
            {var subQ0=sQuery(id+"F0.wireOp",EDGE,"E41");var subQ1=sQuery(id+"F0.wireOp",EDGE,"E10");var subQ2=makeQuery(id+"F0.imprint","INTERSECT",VERTEX,{"disambiguationData":[OD(1.0)],"derivedFrom":[subQ1,subQ0]});Q57=makeQuery(id+"F0.imprint","IMPRINT",FACE,{"disambiguationData":[TD([[makeQuery(id+"F0.imprint","IMPRINT",EDGE,{"disambiguationData":[TD([[subQ2,-1.0]])],"derivedFrom":subQ1}),-1.0]])]});}
            var Q58;
            {var subQ0=sQuery(id+"F0.wireOp",EDGE,"E41");var subQ1=sQuery(id+"F0.wireOp",EDGE,"E8");var subQ2=makeQuery(id+"F0.imprint","INTERSECT",VERTEX,{"disambiguationData":[OD(1.0)],"derivedFrom":[subQ1,subQ0]});Q58=makeQuery(id+"F0.imprint","IMPRINT",FACE,{"disambiguationData":[TD([[makeQuery(id+"F0.imprint","IMPRINT",EDGE,{"disambiguationData":[TD([[subQ2,-1.0]])],"derivedFrom":subQ1}),-1.0]])]});}
            var Q59;
            {var subQ0=sQuery(id+"F0.wireOp",EDGE,"E40");var subQ1=sQuery(id+"F0.wireOp",EDGE,"E8");var subQ2=makeQuery(id+"F0.imprint","INTERSECT",VERTEX,{"disambiguationData":[OD(1.0)],"derivedFrom":[subQ1,subQ0]});Q59=makeQuery(id+"F0.imprint","IMPRINT",FACE,{"disambiguationData":[TD([[makeQuery(id+"F0.imprint","IMPRINT",EDGE,{"disambiguationData":[TD([[subQ2,-1.0]])],"derivedFrom":subQ1}),-1.0]])]});}
            var Q60;
            {var subQ0=sQuery(id+"F0.wireOp",EDGE,"E40");var subQ1=sQuery(id+"F0.wireOp",EDGE,"E10");var subQ2=makeQuery(id+"F0.imprint","INTERSECT",VERTEX,{"disambiguationData":[OD(1.0)],"derivedFrom":[subQ1,subQ0]});Q60=makeQuery(id+"F0.imprint","IMPRINT",FACE,{"disambiguationData":[TD([[makeQuery(id+"F0.imprint","IMPRINT",EDGE,{"disambiguationData":[TD([[subQ2,-1.0]])],"derivedFrom":subQ1}),-1.0]])]});}
            var Q61;
            {var subQ0=sQuery(id+"F0.wireOp",EDGE,"E40");var subQ1=sQuery(id+"F0.wireOp",EDGE,"E12");var subQ2=makeQuery(id+"F0.imprint","INTERSECT",VERTEX,{"disambiguationData":[OD(1.0)],"derivedFrom":[subQ1,subQ0]});Q61=makeQuery(id+"F0.imprint","IMPRINT",FACE,{"disambiguationData":[TD([[makeQuery(id+"F0.imprint","IMPRINT",EDGE,{"disambiguationData":[TD([[subQ2,-1.0]])],"derivedFrom":subQ1}),-1.0]])]});}
            var Q62;
            {var subQ0=sQuery(id+"F0.wireOp",EDGE,"E40");var subQ1=sQuery(id+"F0.wireOp",EDGE,"E14");var subQ2=makeQuery(id+"F0.imprint","INTERSECT",VERTEX,{"disambiguationData":[OD(1.0)],"derivedFrom":[subQ1,subQ0]});Q62=makeQuery(id+"F0.imprint","IMPRINT",FACE,{"disambiguationData":[TD([[makeQuery(id+"F0.imprint","IMPRINT",EDGE,{"disambiguationData":[TD([[subQ2,-1.0]])],"derivedFrom":subQ1}),-1.0]])]});}
            var Q63;
            {var subQ0=sQuery(id+"F0.wireOp",EDGE,"E40");var subQ1=sQuery(id+"F0.wireOp",EDGE,"E16");var subQ2=makeQuery(id+"F0.imprint","INTERSECT",VERTEX,{"disambiguationData":[OD(1.0)],"derivedFrom":[subQ1,subQ0]});Q63=makeQuery(id+"F0.imprint","IMPRINT",FACE,{"disambiguationData":[TD([[makeQuery(id+"F0.imprint","IMPRINT",EDGE,{"disambiguationData":[TD([[subQ2,-1.0]])],"derivedFrom":subQ1}),-1.0]])]});}
            var Q64;
            {var subQ0=sQuery(id+"F0.wireOp",EDGE,"E40");var subQ1=sQuery(id+"F0.wireOp",EDGE,"E17");var subQ2=makeQuery(id+"F0.imprint","INTERSECT",VERTEX,{"disambiguationData":[OD(1.0)],"derivedFrom":[subQ1,subQ0]});Q64=makeQuery(id+"F0.imprint","IMPRINT",FACE,{"disambiguationData":[TD([[makeQuery(id+"F0.imprint","IMPRINT",EDGE,{"disambiguationData":[TD([[subQ2,-1.0]])],"derivedFrom":subQ1}),-1.0]])]});}
            var Q65;
            {var subQ0=sQuery(id+"F0.wireOp",EDGE,"E40");var subQ1=sQuery(id+"F0.wireOp",EDGE,"E18");var subQ2=makeQuery(id+"F0.imprint","INTERSECT",VERTEX,{"disambiguationData":[OD(1.0)],"derivedFrom":[subQ1,subQ0]});Q65=makeQuery(id+"F0.imprint","IMPRINT",FACE,{"disambiguationData":[TD([[makeQuery(id+"F0.imprint","IMPRINT",EDGE,{"disambiguationData":[TD([[subQ2,-1.0]])],"derivedFrom":subQ1}),-1.0]])]});}
            var Q66;
            {var subQ0=sQuery(id+"F0.wireOp",EDGE,"E40");var subQ1=sQuery(id+"F0.wireOp",EDGE,"E20");var subQ2=makeQuery(id+"F0.imprint","INTERSECT",VERTEX,{"disambiguationData":[OD(1.0)],"derivedFrom":[subQ1,subQ0]});Q66=makeQuery(id+"F0.imprint","IMPRINT",FACE,{"disambiguationData":[TD([[makeQuery(id+"F0.imprint","IMPRINT",EDGE,{"disambiguationData":[TD([[subQ2,-1.0]])],"derivedFrom":subQ1}),-1.0]])]});}
            var Q67;
            {var subQ0=sQuery(id+"F0.wireOp",EDGE,"E41");var subQ1=sQuery(id+"F0.wireOp",EDGE,"E20");var subQ2=makeQuery(id+"F0.imprint","INTERSECT",VERTEX,{"disambiguationData":[OD(0.0)],"derivedFrom":[subQ1,subQ0]});Q67=makeQuery(id+"F0.imprint","IMPRINT",FACE,{"disambiguationData":[TD([[makeQuery(id+"F0.imprint","IMPRINT",EDGE,{"disambiguationData":[TD([[subQ2,1.0]])],"derivedFrom":subQ1}),-1.0]])]});}
            var Q68;
            {var subQ0=sQuery(id+"F0.wireOp",EDGE,"E41");var subQ1=sQuery(id+"F0.wireOp",EDGE,"E18");var subQ2=makeQuery(id+"F0.imprint","INTERSECT",VERTEX,{"disambiguationData":[OD(0.0)],"derivedFrom":[subQ1,subQ0]});Q68=makeQuery(id+"F0.imprint","IMPRINT",FACE,{"disambiguationData":[TD([[makeQuery(id+"F0.imprint","IMPRINT",EDGE,{"disambiguationData":[TD([[subQ2,1.0]])],"derivedFrom":subQ1}),-1.0]])]});}
            var Q69;
            {var subQ0=sQuery(id+"F0.wireOp",EDGE,"E41");var subQ1=sQuery(id+"F0.wireOp",EDGE,"E17");var subQ2=makeQuery(id+"F0.imprint","INTERSECT",VERTEX,{"disambiguationData":[OD(0.0)],"derivedFrom":[subQ1,subQ0]});Q69=makeQuery(id+"F0.imprint","IMPRINT",FACE,{"disambiguationData":[TD([[makeQuery(id+"F0.imprint","IMPRINT",EDGE,{"disambiguationData":[TD([[subQ2,1.0]])],"derivedFrom":subQ1}),-1.0]])]});}
            var Q70;
            {var subQ0=sQuery(id+"F0.wireOp",EDGE,"E41");var subQ1=sQuery(id+"F0.wireOp",EDGE,"E16");var subQ2=makeQuery(id+"F0.imprint","INTERSECT",VERTEX,{"disambiguationData":[OD(0.0)],"derivedFrom":[subQ1,subQ0]});Q70=makeQuery(id+"F0.imprint","IMPRINT",FACE,{"disambiguationData":[TD([[makeQuery(id+"F0.imprint","IMPRINT",EDGE,{"disambiguationData":[TD([[subQ2,1.0]])],"derivedFrom":subQ1}),-1.0]])]});}
            var Q71;
            {var subQ0=sQuery(id+"F0.wireOp",EDGE,"E41");var subQ1=sQuery(id+"F0.wireOp",EDGE,"E14");var subQ2=makeQuery(id+"F0.imprint","INTERSECT",VERTEX,{"disambiguationData":[OD(0.0)],"derivedFrom":[subQ1,subQ0]});Q71=makeQuery(id+"F0.imprint","IMPRINT",FACE,{"disambiguationData":[TD([[makeQuery(id+"F0.imprint","IMPRINT",EDGE,{"disambiguationData":[TD([[subQ2,1.0]])],"derivedFrom":subQ1}),-1.0]])]});}
            var Q72;
            {var subQ0=sQuery(id+"F0.wireOp",EDGE,"E41");var subQ1=sQuery(id+"F0.wireOp",EDGE,"E12");var subQ2=makeQuery(id+"F0.imprint","INTERSECT",VERTEX,{"disambiguationData":[OD(0.0)],"derivedFrom":[subQ1,subQ0]});Q72=makeQuery(id+"F0.imprint","IMPRINT",FACE,{"disambiguationData":[TD([[makeQuery(id+"F0.imprint","IMPRINT",EDGE,{"disambiguationData":[TD([[subQ2,1.0]])],"derivedFrom":subQ1}),-1.0]])]});}
            var Q73;
            {var subQ0=sQuery(id+"F0.wireOp",EDGE,"E41");var subQ1=sQuery(id+"F0.wireOp",EDGE,"E10");var subQ2=makeQuery(id+"F0.imprint","INTERSECT",VERTEX,{"disambiguationData":[OD(0.0)],"derivedFrom":[subQ1,subQ0]});Q73=makeQuery(id+"F0.imprint","IMPRINT",FACE,{"disambiguationData":[TD([[makeQuery(id+"F0.imprint","IMPRINT",EDGE,{"disambiguationData":[TD([[subQ2,1.0]])],"derivedFrom":subQ1}),-1.0]])]});}
            var Q74;
            {var subQ0=sQuery(id+"F0.wireOp",EDGE,"E41");var subQ1=sQuery(id+"F0.wireOp",EDGE,"E8");var subQ2=makeQuery(id+"F0.imprint","INTERSECT",VERTEX,{"disambiguationData":[OD(0.0)],"derivedFrom":[subQ1,subQ0]});Q74=makeQuery(id+"F0.imprint","IMPRINT",FACE,{"disambiguationData":[TD([[makeQuery(id+"F0.imprint","IMPRINT",EDGE,{"disambiguationData":[TD([[subQ2,1.0]])],"derivedFrom":subQ1}),-1.0]])]});}
            var Q75;
            {var subQ0=sQuery(id+"F0.wireOp",EDGE,"E42");var subQ1=sQuery(id+"F0.wireOp",EDGE,"E8");var subQ2=makeQuery(id+"F0.imprint","INTERSECT",VERTEX,{"derivedFrom":[subQ1,subQ0]});Q75=makeQuery(id+"F0.imprint","IMPRINT",FACE,{"disambiguationData":[TD([[makeQuery(id+"F0.imprint","IMPRINT",EDGE,{"disambiguationData":[TD([[subQ2,1.0]])],"derivedFrom":subQ1}),-1.0]])]});}
            var Q76;
            {var subQ0=sQuery(id+"F0.wireOp",EDGE,"E42");var subQ1=sQuery(id+"F0.wireOp",EDGE,"E10");var subQ2=makeQuery(id+"F0.imprint","INTERSECT",VERTEX,{"derivedFrom":[subQ1,subQ0]});Q76=makeQuery(id+"F0.imprint","IMPRINT",FACE,{"disambiguationData":[TD([[makeQuery(id+"F0.imprint","IMPRINT",EDGE,{"disambiguationData":[TD([[subQ2,1.0]])],"derivedFrom":subQ1}),-1.0]])]});}
            var Q77;
            {var subQ0=sQuery(id+"F0.wireOp",EDGE,"E42");var subQ1=sQuery(id+"F0.wireOp",EDGE,"E12");var subQ2=makeQuery(id+"F0.imprint","INTERSECT",VERTEX,{"derivedFrom":[subQ1,subQ0]});Q77=makeQuery(id+"F0.imprint","IMPRINT",FACE,{"disambiguationData":[TD([[makeQuery(id+"F0.imprint","IMPRINT",EDGE,{"disambiguationData":[TD([[subQ2,1.0]])],"derivedFrom":subQ1}),-1.0]])]});}
            var Q78;
            {var subQ0=sQuery(id+"F0.wireOp",EDGE,"E42");var subQ1=sQuery(id+"F0.wireOp",EDGE,"E14");var subQ2=makeQuery(id+"F0.imprint","INTERSECT",VERTEX,{"derivedFrom":[subQ1,subQ0]});Q78=makeQuery(id+"F0.imprint","IMPRINT",FACE,{"disambiguationData":[TD([[makeQuery(id+"F0.imprint","IMPRINT",EDGE,{"disambiguationData":[TD([[subQ2,1.0]])],"derivedFrom":subQ1}),-1.0]])]});}
            var Q79;
            {var subQ0=sQuery(id+"F0.wireOp",EDGE,"E42");var subQ1=sQuery(id+"F0.wireOp",EDGE,"E16");var subQ2=makeQuery(id+"F0.imprint","INTERSECT",VERTEX,{"derivedFrom":[subQ1,subQ0]});Q79=makeQuery(id+"F0.imprint","IMPRINT",FACE,{"disambiguationData":[TD([[makeQuery(id+"F0.imprint","IMPRINT",EDGE,{"disambiguationData":[TD([[subQ2,-1.0]])],"derivedFrom":subQ1}),-1.0]])]});}
            var Q80;
            {var subQ0=sQuery(id+"F0.wireOp",EDGE,"E42");var subQ1=sQuery(id+"F0.wireOp",EDGE,"E17");var subQ2=makeQuery(id+"F0.imprint","INTERSECT",VERTEX,{"derivedFrom":[subQ1,subQ0]});Q80=makeQuery(id+"F0.imprint","IMPRINT",FACE,{"disambiguationData":[TD([[makeQuery(id+"F0.imprint","IMPRINT",EDGE,{"disambiguationData":[TD([[subQ2,1.0]])],"derivedFrom":subQ1}),-1.0]])]});}
            var Q81;
            {var subQ0=sQuery(id+"F0.wireOp",EDGE,"E42");var subQ1=sQuery(id+"F0.wireOp",EDGE,"E18");var subQ2=makeQuery(id+"F0.imprint","INTERSECT",VERTEX,{"derivedFrom":[subQ1,subQ0]});Q81=makeQuery(id+"F0.imprint","IMPRINT",FACE,{"disambiguationData":[TD([[makeQuery(id+"F0.imprint","IMPRINT",EDGE,{"disambiguationData":[TD([[subQ2,1.0]])],"derivedFrom":subQ1}),-1.0]])]});}
            var Q82;
            {var subQ0=sQuery(id+"F0.wireOp",EDGE,"E42");var subQ1=sQuery(id+"F0.wireOp",EDGE,"E20");var subQ2=makeQuery(id+"F0.imprint","INTERSECT",VERTEX,{"derivedFrom":[subQ1,subQ0]});Q82=makeQuery(id+"F0.imprint","IMPRINT",FACE,{"disambiguationData":[TD([[makeQuery(id+"F0.imprint","IMPRINT",EDGE,{"disambiguationData":[TD([[subQ2,1.0]])],"derivedFrom":subQ1}),-1.0]])]});}
            var Q83;
            {var subQ0=sQuery(id+"F0.wireOp",EDGE,"E42");var subQ1=sQuery(id+"F0.wireOp",EDGE,"E16");var subQ2=makeQuery(id+"F0.imprint","INTERSECT",VERTEX,{"derivedFrom":[subQ1,subQ0]});Q83=makeQuery(id+"F0.imprint","IMPRINT",FACE,{"disambiguationData":[TD([[makeQuery(id+"F0.imprint","IMPRINT",EDGE,{"disambiguationData":[TD([[subQ2,1.0]])],"derivedFrom":subQ1}),-1.0]])]});}
            var Q84;
            {var subQ0=sQuery(id+"F0.wireOp",EDGE,"E42");var subQ1=sQuery(id+"F0.wireOp",EDGE,"E23");var subQ2=makeQuery(id+"F0.imprint","INTERSECT",VERTEX,{"derivedFrom":[subQ1,subQ0]});Q84=makeQuery(id+"F0.imprint","IMPRINT",FACE,{"disambiguationData":[TD([[makeQuery(id+"F0.imprint","IMPRINT",EDGE,{"disambiguationData":[TD([[subQ2,-1.0]])],"derivedFrom":subQ1}),-1.0]])]});}
            var Q85;
            {var subQ0=sQuery(id+"F0.wireOp",EDGE,"E42");var subQ1=sQuery(id+"F0.wireOp",EDGE,"E26");var subQ2=makeQuery(id+"F0.imprint","INTERSECT",VERTEX,{"derivedFrom":[subQ1,subQ0]});Q85=makeQuery(id+"F0.imprint","IMPRINT",FACE,{"disambiguationData":[TD([[makeQuery(id+"F0.imprint","IMPRINT",EDGE,{"disambiguationData":[TD([[subQ2,-1.0]])],"derivedFrom":subQ1}),-1.0]])]});}
            var Q86;
            {var subQ0=sQuery(id+"F0.wireOp",EDGE,"E42");var subQ1=sQuery(id+"F0.wireOp",EDGE,"E28");var subQ2=makeQuery(id+"F0.imprint","INTERSECT",VERTEX,{"derivedFrom":[subQ1,subQ0]});Q86=makeQuery(id+"F0.imprint","IMPRINT",FACE,{"disambiguationData":[TD([[makeQuery(id+"F0.imprint","IMPRINT",EDGE,{"disambiguationData":[TD([[subQ2,-1.0]])],"derivedFrom":subQ1}),-1.0]])]});}
            var Q87;
            {var subQ0=sQuery(id+"F0.wireOp",EDGE,"E42");var subQ1=sQuery(id+"F0.wireOp",EDGE,"E30");var subQ2=makeQuery(id+"F0.imprint","INTERSECT",VERTEX,{"derivedFrom":[subQ1,subQ0]});Q87=makeQuery(id+"F0.imprint","IMPRINT",FACE,{"disambiguationData":[TD([[makeQuery(id+"F0.imprint","IMPRINT",EDGE,{"disambiguationData":[TD([[subQ2,-1.0]])],"derivedFrom":subQ1}),-1.0]])]});}
            var Q88;
            {var subQ0=sQuery(id+"F0.wireOp",EDGE,"E42");var subQ1=sQuery(id+"F0.wireOp",EDGE,"E36");var subQ2=makeQuery(id+"F0.imprint","INTERSECT",VERTEX,{"derivedFrom":[subQ1,subQ0]});Q88=makeQuery(id+"F0.imprint","IMPRINT",FACE,{"disambiguationData":[TD([[makeQuery(id+"F0.imprint","IMPRINT",EDGE,{"disambiguationData":[TD([[subQ2,-1.0]])],"derivedFrom":subQ1}),-1.0]])]});}
            var Q89;
            {var subQ0=sQuery(id+"F0.wireOp",EDGE,"E42");var subQ1=sQuery(id+"F0.wireOp",EDGE,"E38");var subQ2=makeQuery(id+"F0.imprint","INTERSECT",VERTEX,{"derivedFrom":[subQ1,subQ0]});Q89=makeQuery(id+"F0.imprint","IMPRINT",FACE,{"disambiguationData":[TD([[makeQuery(id+"F0.imprint","IMPRINT",EDGE,{"disambiguationData":[TD([[subQ2,-1.0]])],"derivedFrom":subQ1}),-1.0]])]});}
            var Q90;
            {var subQ0=sQuery(id+"F0.wireOp",EDGE,"E42");var subQ1=sQuery(id+"F0.wireOp",EDGE,"E34");var subQ2=makeQuery(id+"F0.imprint","INTERSECT",VERTEX,{"derivedFrom":[subQ1,subQ0]});Q90=makeQuery(id+"F0.imprint","IMPRINT",FACE,{"disambiguationData":[TD([[makeQuery(id+"F0.imprint","IMPRINT",EDGE,{"disambiguationData":[TD([[subQ2,-1.0]])],"derivedFrom":subQ1}),-1.0]])]});}
            var Q91;
            {var subQ0=sQuery(id+"F0.wireOp",EDGE,"E42");var subQ1=sQuery(id+"F0.wireOp",EDGE,"E32");var subQ2=makeQuery(id+"F0.imprint","INTERSECT",VERTEX,{"derivedFrom":[subQ1,subQ0]});Q91=makeQuery(id+"F0.imprint","IMPRINT",FACE,{"disambiguationData":[TD([[makeQuery(id+"F0.imprint","IMPRINT",EDGE,{"disambiguationData":[TD([[subQ2,-1.0]])],"derivedFrom":subQ1}),-1.0]])]});}
            var Q92;
            {var subQ0=sQuery(id+"F0.wireOp",EDGE,"E40");var subQ1=sQuery(id+"F0.wireOp",EDGE,"E23");var subQ2=makeQuery(id+"F0.imprint","INTERSECT",VERTEX,{"disambiguationData":[OD(0.0)],"derivedFrom":[subQ1,subQ0]});Q92=makeQuery(id+"F0.imprint","IMPRINT",FACE,{"disambiguationData":[TD([[makeQuery(id+"F0.imprint","IMPRINT",EDGE,{"disambiguationData":[TD([[subQ2,-1.0]])],"derivedFrom":subQ1}),-1.0]])]});}
            var Q93;
            {var subQ0=sQuery(id+"F0.wireOp",EDGE,"E40");var subQ1=sQuery(id+"F0.wireOp",EDGE,"E26");var subQ2=makeQuery(id+"F0.imprint","INTERSECT",VERTEX,{"disambiguationData":[OD(0.0)],"derivedFrom":[subQ1,subQ0]});Q93=makeQuery(id+"F0.imprint","IMPRINT",FACE,{"disambiguationData":[TD([[makeQuery(id+"F0.imprint","IMPRINT",EDGE,{"disambiguationData":[TD([[subQ2,-1.0]])],"derivedFrom":subQ1}),-1.0]])]});}
            var Q94;
            {var subQ0=sQuery(id+"F0.wireOp",EDGE,"E40");var subQ1=sQuery(id+"F0.wireOp",EDGE,"E28");var subQ2=makeQuery(id+"F0.imprint","INTERSECT",VERTEX,{"disambiguationData":[OD(0.0)],"derivedFrom":[subQ1,subQ0]});Q94=makeQuery(id+"F0.imprint","IMPRINT",FACE,{"disambiguationData":[TD([[makeQuery(id+"F0.imprint","IMPRINT",EDGE,{"disambiguationData":[TD([[subQ2,-1.0]])],"derivedFrom":subQ1}),-1.0]])]});}
            var Q95;
            {var subQ0=sQuery(id+"F0.wireOp",EDGE,"E40");var subQ1=sQuery(id+"F0.wireOp",EDGE,"E30");var subQ2=makeQuery(id+"F0.imprint","INTERSECT",VERTEX,{"disambiguationData":[OD(0.0)],"derivedFrom":[subQ1,subQ0]});Q95=makeQuery(id+"F0.imprint","IMPRINT",FACE,{"disambiguationData":[TD([[makeQuery(id+"F0.imprint","IMPRINT",EDGE,{"disambiguationData":[TD([[subQ2,-1.0]])],"derivedFrom":subQ1}),-1.0]])]});}
            var Q96;
            {var subQ0=sQuery(id+"F0.wireOp",EDGE,"E40");var subQ1=sQuery(id+"F0.wireOp",EDGE,"E32");var subQ2=makeQuery(id+"F0.imprint","INTERSECT",VERTEX,{"disambiguationData":[OD(0.0)],"derivedFrom":[subQ1,subQ0]});Q96=makeQuery(id+"F0.imprint","IMPRINT",FACE,{"disambiguationData":[TD([[makeQuery(id+"F0.imprint","IMPRINT",EDGE,{"disambiguationData":[TD([[subQ2,-1.0]])],"derivedFrom":subQ1}),-1.0]])]});}
            var Q97;
            {var subQ0=sQuery(id+"F0.wireOp",EDGE,"E40");var subQ1=sQuery(id+"F0.wireOp",EDGE,"E34");var subQ2=makeQuery(id+"F0.imprint","INTERSECT",VERTEX,{"disambiguationData":[OD(0.0)],"derivedFrom":[subQ1,subQ0]});Q97=makeQuery(id+"F0.imprint","IMPRINT",FACE,{"disambiguationData":[TD([[makeQuery(id+"F0.imprint","IMPRINT",EDGE,{"disambiguationData":[TD([[subQ2,-1.0]])],"derivedFrom":subQ1}),-1.0]])]});}
            var Q98;
            {var subQ0=sQuery(id+"F0.wireOp",EDGE,"E40");var subQ1=sQuery(id+"F0.wireOp",EDGE,"E36");var subQ2=makeQuery(id+"F0.imprint","INTERSECT",VERTEX,{"disambiguationData":[OD(0.0)],"derivedFrom":[subQ1,subQ0]});Q98=makeQuery(id+"F0.imprint","IMPRINT",FACE,{"disambiguationData":[TD([[makeQuery(id+"F0.imprint","IMPRINT",EDGE,{"disambiguationData":[TD([[subQ2,-1.0]])],"derivedFrom":subQ1}),-1.0]])]});}
            var Q99;
            {var subQ0=sQuery(id+"F0.wireOp",EDGE,"E40");var subQ1=sQuery(id+"F0.wireOp",EDGE,"E38");var subQ2=makeQuery(id+"F0.imprint","INTERSECT",VERTEX,{"disambiguationData":[OD(0.0)],"derivedFrom":[subQ1,subQ0]});Q99=makeQuery(id+"F0.imprint","IMPRINT",FACE,{"disambiguationData":[TD([[makeQuery(id+"F0.imprint","IMPRINT",EDGE,{"disambiguationData":[TD([[subQ2,-1.0]])],"derivedFrom":subQ1}),-1.0]])]});}
            var Q100;
            {var subQ0=sQuery(id+"F0.wireOp",EDGE,"E42");var subQ1=sQuery(id+"F0.wireOp",EDGE,"E23");var subQ2=makeQuery(id+"F0.imprint","INTERSECT",VERTEX,{"derivedFrom":[subQ1,subQ0]});Q100=makeQuery(id+"F0.imprint","IMPRINT",FACE,{"disambiguationData":[TD([[makeQuery(id+"F0.imprint","IMPRINT",EDGE,{"disambiguationData":[TD([[subQ2,1.0]])],"derivedFrom":subQ1}),-1.0]])]});}
            var Q101;
            {var subQ0=sQuery(id+"F0.wireOp",EDGE,"E42");var subQ1=sQuery(id+"F0.wireOp",EDGE,"E26");var subQ2=makeQuery(id+"F0.imprint","INTERSECT",VERTEX,{"derivedFrom":[subQ1,subQ0]});Q101=makeQuery(id+"F0.imprint","IMPRINT",FACE,{"disambiguationData":[TD([[makeQuery(id+"F0.imprint","IMPRINT",EDGE,{"disambiguationData":[TD([[subQ2,1.0]])],"derivedFrom":subQ1}),-1.0]])]});}
            var Q102;
            {var subQ0=sQuery(id+"F0.wireOp",EDGE,"E42");var subQ1=sQuery(id+"F0.wireOp",EDGE,"E28");var subQ2=makeQuery(id+"F0.imprint","INTERSECT",VERTEX,{"derivedFrom":[subQ1,subQ0]});Q102=makeQuery(id+"F0.imprint","IMPRINT",FACE,{"disambiguationData":[TD([[makeQuery(id+"F0.imprint","IMPRINT",EDGE,{"disambiguationData":[TD([[subQ2,1.0]])],"derivedFrom":subQ1}),-1.0]])]});}
            var Q103;
            {var subQ0=sQuery(id+"F0.wireOp",EDGE,"E42");var subQ1=sQuery(id+"F0.wireOp",EDGE,"E30");var subQ2=makeQuery(id+"F0.imprint","INTERSECT",VERTEX,{"derivedFrom":[subQ1,subQ0]});Q103=makeQuery(id+"F0.imprint","IMPRINT",FACE,{"disambiguationData":[TD([[makeQuery(id+"F0.imprint","IMPRINT",EDGE,{"disambiguationData":[TD([[subQ2,1.0]])],"derivedFrom":subQ1}),-1.0]])]});}
            var Q104;
            {var subQ0=sQuery(id+"F0.wireOp",EDGE,"E42");var subQ1=sQuery(id+"F0.wireOp",EDGE,"E32");var subQ2=makeQuery(id+"F0.imprint","INTERSECT",VERTEX,{"derivedFrom":[subQ1,subQ0]});Q104=makeQuery(id+"F0.imprint","IMPRINT",FACE,{"disambiguationData":[TD([[makeQuery(id+"F0.imprint","IMPRINT",EDGE,{"disambiguationData":[TD([[subQ2,1.0]])],"derivedFrom":subQ1}),-1.0]])]});}
            var Q105;
            {var subQ0=sQuery(id+"F0.wireOp",EDGE,"E42");var subQ1=sQuery(id+"F0.wireOp",EDGE,"E34");var subQ2=makeQuery(id+"F0.imprint","INTERSECT",VERTEX,{"derivedFrom":[subQ1,subQ0]});Q105=makeQuery(id+"F0.imprint","IMPRINT",FACE,{"disambiguationData":[TD([[makeQuery(id+"F0.imprint","IMPRINT",EDGE,{"disambiguationData":[TD([[subQ2,1.0]])],"derivedFrom":subQ1}),-1.0]])]});}
            var Q106;
            {var subQ0=sQuery(id+"F0.wireOp",EDGE,"E42");var subQ1=sQuery(id+"F0.wireOp",EDGE,"E36");var subQ2=makeQuery(id+"F0.imprint","INTERSECT",VERTEX,{"derivedFrom":[subQ1,subQ0]});Q106=makeQuery(id+"F0.imprint","IMPRINT",FACE,{"disambiguationData":[TD([[makeQuery(id+"F0.imprint","IMPRINT",EDGE,{"disambiguationData":[TD([[subQ2,1.0]])],"derivedFrom":subQ1}),-1.0]])]});}
            var Q107;
            {var subQ0=sQuery(id+"F0.wireOp",EDGE,"E42");var subQ1=sQuery(id+"F0.wireOp",EDGE,"E38");var subQ2=makeQuery(id+"F0.imprint","INTERSECT",VERTEX,{"derivedFrom":[subQ1,subQ0]});Q107=makeQuery(id+"F0.imprint","IMPRINT",FACE,{"disambiguationData":[TD([[makeQuery(id+"F0.imprint","IMPRINT",EDGE,{"disambiguationData":[TD([[subQ2,1.0]])],"derivedFrom":subQ1}),-1.0]])]});}
            var Q108;
            {var subQ0=sQuery(id+"F0.wireOp",EDGE,"E41");var subQ1=sQuery(id+"F0.wireOp",EDGE,"E23");var subQ2=makeQuery(id+"F0.imprint","INTERSECT",VERTEX,{"disambiguationData":[OD(0.0)],"derivedFrom":[subQ1,subQ0]});Q108=makeQuery(id+"F0.imprint","IMPRINT",FACE,{"disambiguationData":[TD([[makeQuery(id+"F0.imprint","IMPRINT",EDGE,{"disambiguationData":[TD([[subQ2,1.0]])],"derivedFrom":subQ1}),-1.0]])]});}
            var Q109;
            {var subQ0=sQuery(id+"F0.wireOp",EDGE,"E41");var subQ1=sQuery(id+"F0.wireOp",EDGE,"E26");var subQ2=makeQuery(id+"F0.imprint","INTERSECT",VERTEX,{"disambiguationData":[OD(0.0)],"derivedFrom":[subQ1,subQ0]});Q109=makeQuery(id+"F0.imprint","IMPRINT",FACE,{"disambiguationData":[TD([[makeQuery(id+"F0.imprint","IMPRINT",EDGE,{"disambiguationData":[TD([[subQ2,1.0]])],"derivedFrom":subQ1}),-1.0]])]});}
            var Q110;
            {var subQ0=sQuery(id+"F0.wireOp",EDGE,"E41");var subQ1=sQuery(id+"F0.wireOp",EDGE,"E28");var subQ2=makeQuery(id+"F0.imprint","INTERSECT",VERTEX,{"disambiguationData":[OD(0.0)],"derivedFrom":[subQ1,subQ0]});Q110=makeQuery(id+"F0.imprint","IMPRINT",FACE,{"disambiguationData":[TD([[makeQuery(id+"F0.imprint","IMPRINT",EDGE,{"disambiguationData":[TD([[subQ2,1.0]])],"derivedFrom":subQ1}),-1.0]])]});}
            var Q111;
            {var subQ0=sQuery(id+"F0.wireOp",EDGE,"E41");var subQ1=sQuery(id+"F0.wireOp",EDGE,"E30");var subQ2=makeQuery(id+"F0.imprint","INTERSECT",VERTEX,{"disambiguationData":[OD(0.0)],"derivedFrom":[subQ1,subQ0]});Q111=makeQuery(id+"F0.imprint","IMPRINT",FACE,{"disambiguationData":[TD([[makeQuery(id+"F0.imprint","IMPRINT",EDGE,{"disambiguationData":[TD([[subQ2,1.0]])],"derivedFrom":subQ1}),-1.0]])]});}
            var Q112;
            {var subQ0=sQuery(id+"F0.wireOp",EDGE,"E41");var subQ1=sQuery(id+"F0.wireOp",EDGE,"E32");var subQ2=makeQuery(id+"F0.imprint","INTERSECT",VERTEX,{"disambiguationData":[OD(0.0)],"derivedFrom":[subQ1,subQ0]});Q112=makeQuery(id+"F0.imprint","IMPRINT",FACE,{"disambiguationData":[TD([[makeQuery(id+"F0.imprint","IMPRINT",EDGE,{"disambiguationData":[TD([[subQ2,1.0]])],"derivedFrom":subQ1}),-1.0]])]});}
            var Q113;
            {var subQ0=sQuery(id+"F0.wireOp",EDGE,"E41");var subQ1=sQuery(id+"F0.wireOp",EDGE,"E34");var subQ2=makeQuery(id+"F0.imprint","INTERSECT",VERTEX,{"disambiguationData":[OD(0.0)],"derivedFrom":[subQ1,subQ0]});Q113=makeQuery(id+"F0.imprint","IMPRINT",FACE,{"disambiguationData":[TD([[makeQuery(id+"F0.imprint","IMPRINT",EDGE,{"disambiguationData":[TD([[subQ2,1.0]])],"derivedFrom":subQ1}),-1.0]])]});}
            var Q114;
            {var subQ0=sQuery(id+"F0.wireOp",EDGE,"E41");var subQ1=sQuery(id+"F0.wireOp",EDGE,"E36");var subQ2=makeQuery(id+"F0.imprint","INTERSECT",VERTEX,{"disambiguationData":[OD(0.0)],"derivedFrom":[subQ1,subQ0]});Q114=makeQuery(id+"F0.imprint","IMPRINT",FACE,{"disambiguationData":[TD([[makeQuery(id+"F0.imprint","IMPRINT",EDGE,{"disambiguationData":[TD([[subQ2,1.0]])],"derivedFrom":subQ1}),-1.0]])]});}
            var Q115;
            {var subQ0=sQuery(id+"F0.wireOp",EDGE,"E41");var subQ1=sQuery(id+"F0.wireOp",EDGE,"E38");var subQ2=makeQuery(id+"F0.imprint","INTERSECT",VERTEX,{"disambiguationData":[OD(0.0)],"derivedFrom":[subQ1,subQ0]});Q115=makeQuery(id+"F0.imprint","IMPRINT",FACE,{"disambiguationData":[TD([[makeQuery(id+"F0.imprint","IMPRINT",EDGE,{"disambiguationData":[TD([[subQ2,1.0]])],"derivedFrom":subQ1}),-1.0]])]});}
            var Q116;
            {var subQ0=sQuery(id+"F0.wireOp",EDGE,"E40");var subQ1=sQuery(id+"F0.wireOp",EDGE,"E23");var subQ2=makeQuery(id+"F0.imprint","INTERSECT",VERTEX,{"disambiguationData":[OD(1.0)],"derivedFrom":[subQ1,subQ0]});Q116=makeQuery(id+"F0.imprint","IMPRINT",FACE,{"disambiguationData":[TD([[makeQuery(id+"F0.imprint","IMPRINT",EDGE,{"disambiguationData":[TD([[subQ2,-1.0]])],"derivedFrom":subQ1}),-1.0]])]});}
            var Q117;
            {var subQ0=sQuery(id+"F0.wireOp",EDGE,"E40");var subQ1=sQuery(id+"F0.wireOp",EDGE,"E26");var subQ2=makeQuery(id+"F0.imprint","INTERSECT",VERTEX,{"disambiguationData":[OD(1.0)],"derivedFrom":[subQ1,subQ0]});Q117=makeQuery(id+"F0.imprint","IMPRINT",FACE,{"disambiguationData":[TD([[makeQuery(id+"F0.imprint","IMPRINT",EDGE,{"disambiguationData":[TD([[subQ2,-1.0]])],"derivedFrom":subQ1}),-1.0]])]});}
            var Q118;
            {var subQ0=sQuery(id+"F0.wireOp",EDGE,"E40");var subQ1=sQuery(id+"F0.wireOp",EDGE,"E28");var subQ2=makeQuery(id+"F0.imprint","INTERSECT",VERTEX,{"disambiguationData":[OD(1.0)],"derivedFrom":[subQ1,subQ0]});Q118=makeQuery(id+"F0.imprint","IMPRINT",FACE,{"disambiguationData":[TD([[makeQuery(id+"F0.imprint","IMPRINT",EDGE,{"disambiguationData":[TD([[subQ2,-1.0]])],"derivedFrom":subQ1}),-1.0]])]});}
            var Q119;
            {var subQ0=sQuery(id+"F0.wireOp",EDGE,"E40");var subQ1=sQuery(id+"F0.wireOp",EDGE,"E30");var subQ2=makeQuery(id+"F0.imprint","INTERSECT",VERTEX,{"disambiguationData":[OD(1.0)],"derivedFrom":[subQ1,subQ0]});Q119=makeQuery(id+"F0.imprint","IMPRINT",FACE,{"disambiguationData":[TD([[makeQuery(id+"F0.imprint","IMPRINT",EDGE,{"disambiguationData":[TD([[subQ2,-1.0]])],"derivedFrom":subQ1}),-1.0]])]});}
            var Q120;
            {var subQ0=sQuery(id+"F0.wireOp",EDGE,"E40");var subQ1=sQuery(id+"F0.wireOp",EDGE,"E32");var subQ2=makeQuery(id+"F0.imprint","INTERSECT",VERTEX,{"disambiguationData":[OD(1.0)],"derivedFrom":[subQ1,subQ0]});Q120=makeQuery(id+"F0.imprint","IMPRINT",FACE,{"disambiguationData":[TD([[makeQuery(id+"F0.imprint","IMPRINT",EDGE,{"disambiguationData":[TD([[subQ2,-1.0]])],"derivedFrom":subQ1}),-1.0]])]});}
            var Q121;
            {var subQ0=sQuery(id+"F0.wireOp",EDGE,"E40");var subQ1=sQuery(id+"F0.wireOp",EDGE,"E34");var subQ2=makeQuery(id+"F0.imprint","INTERSECT",VERTEX,{"disambiguationData":[OD(1.0)],"derivedFrom":[subQ1,subQ0]});Q121=makeQuery(id+"F0.imprint","IMPRINT",FACE,{"disambiguationData":[TD([[makeQuery(id+"F0.imprint","IMPRINT",EDGE,{"disambiguationData":[TD([[subQ2,-1.0]])],"derivedFrom":subQ1}),-1.0]])]});}
            var Q122;
            {var subQ0=sQuery(id+"F0.wireOp",EDGE,"E40");var subQ1=sQuery(id+"F0.wireOp",EDGE,"E36");var subQ2=makeQuery(id+"F0.imprint","INTERSECT",VERTEX,{"disambiguationData":[OD(1.0)],"derivedFrom":[subQ1,subQ0]});Q122=makeQuery(id+"F0.imprint","IMPRINT",FACE,{"disambiguationData":[TD([[makeQuery(id+"F0.imprint","IMPRINT",EDGE,{"disambiguationData":[TD([[subQ2,-1.0]])],"derivedFrom":subQ1}),-1.0]])]});}
            var Q123;
            {var subQ0=sQuery(id+"F0.wireOp",EDGE,"E40");var subQ1=sQuery(id+"F0.wireOp",EDGE,"E38");var subQ2=makeQuery(id+"F0.imprint","INTERSECT",VERTEX,{"disambiguationData":[OD(1.0)],"derivedFrom":[subQ1,subQ0]});Q123=makeQuery(id+"F0.imprint","IMPRINT",FACE,{"disambiguationData":[TD([[makeQuery(id+"F0.imprint","IMPRINT",EDGE,{"disambiguationData":[TD([[subQ2,-1.0]])],"derivedFrom":subQ1}),-1.0]])]});}
            var Q124;
            {var subQ0=sQuery(id+"F0.wireOp",EDGE,"E41");var subQ1=sQuery(id+"F0.wireOp",EDGE,"E23");var subQ2=makeQuery(id+"F0.imprint","INTERSECT",VERTEX,{"disambiguationData":[OD(1.0)],"derivedFrom":[subQ1,subQ0]});Q124=makeQuery(id+"F0.imprint","IMPRINT",FACE,{"disambiguationData":[TD([[makeQuery(id+"F0.imprint","IMPRINT",EDGE,{"disambiguationData":[TD([[subQ2,-1.0]])],"derivedFrom":subQ1}),-1.0]])]});}
            var Q125;
            {var subQ0=sQuery(id+"F0.wireOp",EDGE,"E41");var subQ1=sQuery(id+"F0.wireOp",EDGE,"E26");var subQ2=makeQuery(id+"F0.imprint","INTERSECT",VERTEX,{"disambiguationData":[OD(1.0)],"derivedFrom":[subQ1,subQ0]});Q125=makeQuery(id+"F0.imprint","IMPRINT",FACE,{"disambiguationData":[TD([[makeQuery(id+"F0.imprint","IMPRINT",EDGE,{"disambiguationData":[TD([[subQ2,-1.0]])],"derivedFrom":subQ1}),-1.0]])]});}
            var Q126;
            {var subQ0=sQuery(id+"F0.wireOp",EDGE,"E41");var subQ1=sQuery(id+"F0.wireOp",EDGE,"E28");var subQ2=makeQuery(id+"F0.imprint","INTERSECT",VERTEX,{"disambiguationData":[OD(1.0)],"derivedFrom":[subQ1,subQ0]});Q126=makeQuery(id+"F0.imprint","IMPRINT",FACE,{"disambiguationData":[TD([[makeQuery(id+"F0.imprint","IMPRINT",EDGE,{"disambiguationData":[TD([[subQ2,-1.0]])],"derivedFrom":subQ1}),-1.0]])]});}
            var Q127;
            {var subQ0=sQuery(id+"F0.wireOp",EDGE,"E41");var subQ1=sQuery(id+"F0.wireOp",EDGE,"E30");var subQ2=makeQuery(id+"F0.imprint","INTERSECT",VERTEX,{"disambiguationData":[OD(1.0)],"derivedFrom":[subQ1,subQ0]});Q127=makeQuery(id+"F0.imprint","IMPRINT",FACE,{"disambiguationData":[TD([[makeQuery(id+"F0.imprint","IMPRINT",EDGE,{"disambiguationData":[TD([[subQ2,-1.0]])],"derivedFrom":subQ1}),-1.0]])]});}
            var Q128;
            {var subQ0=sQuery(id+"F0.wireOp",EDGE,"E41");var subQ1=sQuery(id+"F0.wireOp",EDGE,"E32");var subQ2=makeQuery(id+"F0.imprint","INTERSECT",VERTEX,{"disambiguationData":[OD(1.0)],"derivedFrom":[subQ1,subQ0]});Q128=makeQuery(id+"F0.imprint","IMPRINT",FACE,{"disambiguationData":[TD([[makeQuery(id+"F0.imprint","IMPRINT",EDGE,{"disambiguationData":[TD([[subQ2,-1.0]])],"derivedFrom":subQ1}),-1.0]])]});}
            var Q129;
            {var subQ0=sQuery(id+"F0.wireOp",EDGE,"E41");var subQ1=sQuery(id+"F0.wireOp",EDGE,"E34");var subQ2=makeQuery(id+"F0.imprint","INTERSECT",VERTEX,{"disambiguationData":[OD(1.0)],"derivedFrom":[subQ1,subQ0]});Q129=makeQuery(id+"F0.imprint","IMPRINT",FACE,{"disambiguationData":[TD([[makeQuery(id+"F0.imprint","IMPRINT",EDGE,{"disambiguationData":[TD([[subQ2,-1.0]])],"derivedFrom":subQ1}),-1.0]])]});}
            var Q130;
            {var subQ0=sQuery(id+"F0.wireOp",EDGE,"E41");var subQ1=sQuery(id+"F0.wireOp",EDGE,"E36");var subQ2=makeQuery(id+"F0.imprint","INTERSECT",VERTEX,{"disambiguationData":[OD(1.0)],"derivedFrom":[subQ1,subQ0]});Q130=makeQuery(id+"F0.imprint","IMPRINT",FACE,{"disambiguationData":[TD([[makeQuery(id+"F0.imprint","IMPRINT",EDGE,{"disambiguationData":[TD([[subQ2,-1.0]])],"derivedFrom":subQ1}),-1.0]])]});}
            var Q131;
            {var subQ0=sQuery(id+"F0.wireOp",EDGE,"E41");var subQ1=sQuery(id+"F0.wireOp",EDGE,"E38");var subQ2=makeQuery(id+"F0.imprint","INTERSECT",VERTEX,{"disambiguationData":[OD(1.0)],"derivedFrom":[subQ1,subQ0]});Q131=makeQuery(id+"F0.imprint","IMPRINT",FACE,{"disambiguationData":[TD([[makeQuery(id+"F0.imprint","IMPRINT",EDGE,{"disambiguationData":[TD([[subQ2,-1.0]])],"derivedFrom":subQ1}),-1.0]])]});}
            var Q132;
            {var subQ0=sQuery(id+"F0.wireOp",EDGE,"E45");var subQ1=sQuery(id+"F0.wireOp",EDGE,"E23");var subQ2=makeQuery(id+"F0.imprint","INTERSECT",VERTEX,{"derivedFrom":[subQ1,subQ0]});Q132=makeQuery(id+"F0.imprint","IMPRINT",FACE,{"disambiguationData":[TD([[makeQuery(id+"F0.imprint","IMPRINT",EDGE,{"disambiguationData":[TD([[subQ2,-1.0]])],"derivedFrom":subQ1}),-1.0]])]});}
            var Q133;
            {var subQ0=sQuery(id+"F0.wireOp",EDGE,"E45");var subQ1=sQuery(id+"F0.wireOp",EDGE,"E26");var subQ2=makeQuery(id+"F0.imprint","INTERSECT",VERTEX,{"derivedFrom":[subQ1,subQ0]});Q133=makeQuery(id+"F0.imprint","IMPRINT",FACE,{"disambiguationData":[TD([[makeQuery(id+"F0.imprint","IMPRINT",EDGE,{"disambiguationData":[TD([[subQ2,-1.0]])],"derivedFrom":subQ1}),-1.0]])]});}
            var Q134;
            {var subQ0=sQuery(id+"F0.wireOp",EDGE,"E45");var subQ1=sQuery(id+"F0.wireOp",EDGE,"E28");var subQ2=makeQuery(id+"F0.imprint","INTERSECT",VERTEX,{"derivedFrom":[subQ1,subQ0]});Q134=makeQuery(id+"F0.imprint","IMPRINT",FACE,{"disambiguationData":[TD([[makeQuery(id+"F0.imprint","IMPRINT",EDGE,{"disambiguationData":[TD([[subQ2,-1.0]])],"derivedFrom":subQ1}),-1.0]])]});}
            var Q135;
            {var subQ0=sQuery(id+"F0.wireOp",EDGE,"E45");var subQ1=sQuery(id+"F0.wireOp",EDGE,"E30");var subQ2=makeQuery(id+"F0.imprint","INTERSECT",VERTEX,{"derivedFrom":[subQ1,subQ0]});Q135=makeQuery(id+"F0.imprint","IMPRINT",FACE,{"disambiguationData":[TD([[makeQuery(id+"F0.imprint","IMPRINT",EDGE,{"disambiguationData":[TD([[subQ2,-1.0]])],"derivedFrom":subQ1}),-1.0]])]});}
            var Q136;
            {var subQ0=sQuery(id+"F0.wireOp",EDGE,"E45");var subQ1=sQuery(id+"F0.wireOp",EDGE,"E32");var subQ2=makeQuery(id+"F0.imprint","INTERSECT",VERTEX,{"derivedFrom":[subQ1,subQ0]});Q136=makeQuery(id+"F0.imprint","IMPRINT",FACE,{"disambiguationData":[TD([[makeQuery(id+"F0.imprint","IMPRINT",EDGE,{"disambiguationData":[TD([[subQ2,-1.0]])],"derivedFrom":subQ1}),-1.0]])]});}
            var Q137;
            {var subQ0=sQuery(id+"F0.wireOp",EDGE,"E45");var subQ1=sQuery(id+"F0.wireOp",EDGE,"E34");var subQ2=makeQuery(id+"F0.imprint","INTERSECT",VERTEX,{"derivedFrom":[subQ1,subQ0]});Q137=makeQuery(id+"F0.imprint","IMPRINT",FACE,{"disambiguationData":[TD([[makeQuery(id+"F0.imprint","IMPRINT",EDGE,{"disambiguationData":[TD([[subQ2,-1.0]])],"derivedFrom":subQ1}),-1.0]])]});}
            var Q138;
            {var subQ0=sQuery(id+"F0.wireOp",EDGE,"E45");var subQ1=sQuery(id+"F0.wireOp",EDGE,"E36");var subQ2=makeQuery(id+"F0.imprint","INTERSECT",VERTEX,{"derivedFrom":[subQ1,subQ0]});Q138=makeQuery(id+"F0.imprint","IMPRINT",FACE,{"disambiguationData":[TD([[makeQuery(id+"F0.imprint","IMPRINT",EDGE,{"disambiguationData":[TD([[subQ2,-1.0]])],"derivedFrom":subQ1}),-1.0]])]});}
            var Q139;
            {var subQ0=sQuery(id+"F0.wireOp",EDGE,"E45");var subQ1=sQuery(id+"F0.wireOp",EDGE,"E38");var subQ2=makeQuery(id+"F0.imprint","INTERSECT",VERTEX,{"derivedFrom":[subQ1,subQ0]});Q139=makeQuery(id+"F0.imprint","IMPRINT",FACE,{"disambiguationData":[TD([[makeQuery(id+"F0.imprint","IMPRINT",EDGE,{"disambiguationData":[TD([[subQ2,-1.0]])],"derivedFrom":subQ1}),-1.0]])]});}
            extrude(context, id + "F2", {"entities" : qUnion([Q0, Q1, Q2, Q3, Q4, Q5, Q6, Q7, Q8, Q9, Q10, Q11, Q12, Q13, Q14, Q15, Q16, Q17, Q18, Q19, Q20, Q21, Q22, Q23, Q24, Q25, Q26, Q27, Q28, Q29, Q30, Q31, Q32, Q33, Q34, Q35, Q36, Q37, Q38, Q39, Q40, Q41, Q42, Q43, Q44, Q45, Q46, Q47, Q48, Q49, Q50, Q51, Q52, Q53, Q54, Q55, Q56, Q57, Q58, Q59, Q60, Q61, Q62, Q63, Q64, Q65, Q66, Q67, Q68, Q69, Q70, Q71, Q72, Q73, Q74, Q75, Q76, Q77, Q78, Q79, Q80, Q81, Q82, Q83, Q84, Q85, Q86, Q87, Q88, Q89, Q90, Q91, Q92, Q93, Q94, Q95, Q96, Q97, Q98, Q99, Q100, Q101, Q102, Q103, Q104, Q105, Q106, Q107, Q108, Q109, Q110, Q111, Q112, Q113, Q114, Q115, Q116, Q117, Q118, Q119, Q120, Q121, Q122, Q123, Q124, Q125, Q126, Q127, Q128, Q129, Q130, Q131, Q132, Q133, Q134, Q135, Q136, Q137, Q138, Q139]), "operationType" : NewBodyOperationType.REMOVE, "depth" : 25 * mm, "offsetDistance" : 25 * mm});
        }
        {
            var Q0;
            {var subQ0=sQuery(id+"F0.wireOp",EDGE,"E41");var subQ1=sQuery(id+"F0.wireOp",EDGE,"E3");var subQ2=makeQuery(id+"F0.imprint","INTERSECT",VERTEX,{"disambiguationData":[OD(1.0)],"derivedFrom":[subQ1,subQ0]});Q0=makeQuery(id+"F0.imprint","IMPRINT",FACE,{"disambiguationData":[TD([[makeQuery(id+"F0.imprint","IMPRINT",EDGE,{"disambiguationData":[TD([[subQ2,-1.0]])],"derivedFrom":subQ1}),-1.0]])]});}
            var Q1;
            {var subQ0=sQuery(id+"F0.wireOp",EDGE,"E41");var subQ1=sQuery(id+"F0.wireOp",EDGE,"E4");var subQ2=makeQuery(id+"F0.imprint","INTERSECT",VERTEX,{"disambiguationData":[OD(1.0)],"derivedFrom":[subQ1,subQ0]});Q1=makeQuery(id+"F0.imprint","IMPRINT",FACE,{"disambiguationData":[TD([[makeQuery(id+"F0.imprint","IMPRINT",EDGE,{"disambiguationData":[TD([[subQ2,-1.0]])],"derivedFrom":subQ1}),1.0]])]});}
            var Q2;
            {var subQ0=sQuery(id+"F0.wireOp",EDGE,"E41");var subQ1=sQuery(id+"F0.wireOp",EDGE,"E7");var subQ2=makeQuery(id+"F0.imprint","INTERSECT",VERTEX,{"disambiguationData":[OD(1.0)],"derivedFrom":[subQ1,subQ0]});Q2=makeQuery(id+"F0.imprint","IMPRINT",FACE,{"disambiguationData":[TD([[makeQuery(id+"F0.imprint","IMPRINT",EDGE,{"disambiguationData":[TD([[subQ2,-1.0]])],"derivedFrom":subQ1}),-1.0]])]});}
            var Q3;
            {var subQ0=sQuery(id+"F0.wireOp",EDGE,"E41");var subQ1=sQuery(id+"F0.wireOp",EDGE,"E9");var subQ2=makeQuery(id+"F0.imprint","INTERSECT",VERTEX,{"disambiguationData":[OD(1.0)],"derivedFrom":[subQ1,subQ0]});Q3=makeQuery(id+"F0.imprint","IMPRINT",FACE,{"disambiguationData":[TD([[makeQuery(id+"F0.imprint","IMPRINT",EDGE,{"disambiguationData":[TD([[subQ2,-1.0]])],"derivedFrom":subQ1}),-1.0]])]});}
            var Q4;
            {var subQ0=sQuery(id+"F0.wireOp",EDGE,"E41");var subQ1=sQuery(id+"F0.wireOp",EDGE,"E11");var subQ2=makeQuery(id+"F0.imprint","INTERSECT",VERTEX,{"disambiguationData":[OD(1.0)],"derivedFrom":[subQ1,subQ0]});Q4=makeQuery(id+"F0.imprint","IMPRINT",FACE,{"disambiguationData":[TD([[makeQuery(id+"F0.imprint","IMPRINT",EDGE,{"disambiguationData":[TD([[subQ2,-1.0]])],"derivedFrom":subQ1}),-1.0]])]});}
            var Q5;
            {var subQ0=sQuery(id+"F0.wireOp",EDGE,"E41");var subQ1=sQuery(id+"F0.wireOp",EDGE,"E13");var subQ2=makeQuery(id+"F0.imprint","INTERSECT",VERTEX,{"disambiguationData":[OD(1.0)],"derivedFrom":[subQ1,subQ0]});Q5=makeQuery(id+"F0.imprint","IMPRINT",FACE,{"disambiguationData":[TD([[makeQuery(id+"F0.imprint","IMPRINT",EDGE,{"disambiguationData":[TD([[subQ2,-1.0]])],"derivedFrom":subQ1}),-1.0]])]});}
            var Q6;
            {var subQ0=sQuery(id+"F0.wireOp",EDGE,"E41");var subQ1=sQuery(id+"F0.wireOp",EDGE,"E15");var subQ2=makeQuery(id+"F0.imprint","INTERSECT",VERTEX,{"disambiguationData":[OD(1.0)],"derivedFrom":[subQ1,subQ0]});Q6=makeQuery(id+"F0.imprint","IMPRINT",FACE,{"disambiguationData":[TD([[makeQuery(id+"F0.imprint","IMPRINT",EDGE,{"disambiguationData":[TD([[subQ2,-1.0]])],"derivedFrom":subQ1}),-1.0]])]});}
            var Q7;
            {var subQ0=sQuery(id+"F0.wireOp",EDGE,"E41");var subQ1=sQuery(id+"F0.wireOp",EDGE,"E17");var subQ2=makeQuery(id+"F0.imprint","INTERSECT",VERTEX,{"disambiguationData":[OD(1.0)],"derivedFrom":[subQ1,subQ0]});Q7=makeQuery(id+"F0.imprint","IMPRINT",FACE,{"disambiguationData":[TD([[makeQuery(id+"F0.imprint","IMPRINT",EDGE,{"disambiguationData":[TD([[subQ2,-1.0]])],"derivedFrom":subQ1}),1.0]])]});}
            var Q8;
            {var subQ0=sQuery(id+"F0.wireOp",EDGE,"E41");var subQ1=sQuery(id+"F0.wireOp",EDGE,"E18");var subQ2=makeQuery(id+"F0.imprint","INTERSECT",VERTEX,{"disambiguationData":[OD(1.0)],"derivedFrom":[subQ1,subQ0]});Q8=makeQuery(id+"F0.imprint","IMPRINT",FACE,{"disambiguationData":[TD([[makeQuery(id+"F0.imprint","IMPRINT",EDGE,{"disambiguationData":[TD([[subQ2,-1.0]])],"derivedFrom":subQ1}),1.0]])]});}
            var Q9;
            {var subQ0=sQuery(id+"F0.wireOp",EDGE,"E41");var subQ1=sQuery(id+"F0.wireOp",EDGE,"E19");var subQ2=makeQuery(id+"F0.imprint","INTERSECT",VERTEX,{"disambiguationData":[OD(1.0)],"derivedFrom":[subQ1,subQ0]});Q9=makeQuery(id+"F0.imprint","IMPRINT",FACE,{"disambiguationData":[TD([[makeQuery(id+"F0.imprint","IMPRINT",EDGE,{"disambiguationData":[TD([[subQ2,-1.0]])],"derivedFrom":subQ1}),-1.0]])]});}
            var Q10;
            {var subQ0=sQuery(id+"F0.wireOp",EDGE,"E41");var subQ1=sQuery(id+"F0.wireOp",EDGE,"E23");var subQ2=makeQuery(id+"F0.imprint","INTERSECT",VERTEX,{"disambiguationData":[OD(1.0)],"derivedFrom":[subQ1,subQ0]});Q10=makeQuery(id+"F0.imprint","IMPRINT",FACE,{"disambiguationData":[TD([[makeQuery(id+"F0.imprint","IMPRINT",EDGE,{"disambiguationData":[TD([[subQ2,-1.0]])],"derivedFrom":subQ1}),1.0]])]});}
            var Q11;
            {var subQ0=sQuery(id+"F0.wireOp",EDGE,"E41");var subQ1=sQuery(id+"F0.wireOp",EDGE,"E25");var subQ2=makeQuery(id+"F0.imprint","INTERSECT",VERTEX,{"disambiguationData":[OD(1.0)],"derivedFrom":[subQ1,subQ0]});Q11=makeQuery(id+"F0.imprint","IMPRINT",FACE,{"disambiguationData":[TD([[makeQuery(id+"F0.imprint","IMPRINT",EDGE,{"disambiguationData":[TD([[subQ2,-1.0]])],"derivedFrom":subQ1}),-1.0]])]});}
            var Q12;
            {var subQ0=sQuery(id+"F0.wireOp",EDGE,"E41");var subQ1=sQuery(id+"F0.wireOp",EDGE,"E27");var subQ2=makeQuery(id+"F0.imprint","INTERSECT",VERTEX,{"disambiguationData":[OD(1.0)],"derivedFrom":[subQ1,subQ0]});Q12=makeQuery(id+"F0.imprint","IMPRINT",FACE,{"disambiguationData":[TD([[makeQuery(id+"F0.imprint","IMPRINT",EDGE,{"disambiguationData":[TD([[subQ2,-1.0]])],"derivedFrom":subQ1}),-1.0]])]});}
            var Q13;
            {var subQ0=sQuery(id+"F0.wireOp",EDGE,"E41");var subQ1=sQuery(id+"F0.wireOp",EDGE,"E29");var subQ2=makeQuery(id+"F0.imprint","INTERSECT",VERTEX,{"disambiguationData":[OD(1.0)],"derivedFrom":[subQ1,subQ0]});Q13=makeQuery(id+"F0.imprint","IMPRINT",FACE,{"disambiguationData":[TD([[makeQuery(id+"F0.imprint","IMPRINT",EDGE,{"disambiguationData":[TD([[subQ2,-1.0]])],"derivedFrom":subQ1}),-1.0]])]});}
            var Q14;
            {var subQ0=sQuery(id+"F0.wireOp",EDGE,"E41");var subQ1=sQuery(id+"F0.wireOp",EDGE,"E31");var subQ2=makeQuery(id+"F0.imprint","INTERSECT",VERTEX,{"disambiguationData":[OD(1.0)],"derivedFrom":[subQ1,subQ0]});Q14=makeQuery(id+"F0.imprint","IMPRINT",FACE,{"disambiguationData":[TD([[makeQuery(id+"F0.imprint","IMPRINT",EDGE,{"disambiguationData":[TD([[subQ2,-1.0]])],"derivedFrom":subQ1}),-1.0]])]});}
            var Q15;
            {var subQ0=sQuery(id+"F0.wireOp",EDGE,"E41");var subQ1=sQuery(id+"F0.wireOp",EDGE,"E33");var subQ2=makeQuery(id+"F0.imprint","INTERSECT",VERTEX,{"disambiguationData":[OD(1.0)],"derivedFrom":[subQ1,subQ0]});Q15=makeQuery(id+"F0.imprint","IMPRINT",FACE,{"disambiguationData":[TD([[makeQuery(id+"F0.imprint","IMPRINT",EDGE,{"disambiguationData":[TD([[subQ2,-1.0]])],"derivedFrom":subQ1}),-1.0]])]});}
            var Q16;
            {var subQ0=sQuery(id+"F0.wireOp",EDGE,"E41");var subQ1=sQuery(id+"F0.wireOp",EDGE,"E35");var subQ2=makeQuery(id+"F0.imprint","INTERSECT",VERTEX,{"disambiguationData":[OD(1.0)],"derivedFrom":[subQ1,subQ0]});Q16=makeQuery(id+"F0.imprint","IMPRINT",FACE,{"disambiguationData":[TD([[makeQuery(id+"F0.imprint","IMPRINT",EDGE,{"disambiguationData":[TD([[subQ2,-1.0]])],"derivedFrom":subQ1}),-1.0]])]});}
            var Q17;
            {var subQ0=sQuery(id+"F0.wireOp",EDGE,"E41");var subQ1=sQuery(id+"F0.wireOp",EDGE,"E37");var subQ2=makeQuery(id+"F0.imprint","INTERSECT",VERTEX,{"disambiguationData":[OD(1.0)],"derivedFrom":[subQ1,subQ0]});Q17=makeQuery(id+"F0.imprint","IMPRINT",FACE,{"disambiguationData":[TD([[makeQuery(id+"F0.imprint","IMPRINT",EDGE,{"disambiguationData":[TD([[subQ2,-1.0]])],"derivedFrom":subQ1}),-1.0]])]});}
            var Q18;
            {var subQ0=sQuery(id+"F0.wireOp",EDGE,"E40");var subQ1=sQuery(id+"F0.wireOp",EDGE,"E0");var subQ2=makeQuery(id+"F0.imprint","INTERSECT",VERTEX,{"disambiguationData":[OD(1.0)],"derivedFrom":[subQ1,subQ0]});Q18=makeQuery(id+"F0.imprint","IMPRINT",FACE,{"disambiguationData":[TD([[makeQuery(id+"F0.imprint","IMPRINT",EDGE,{"disambiguationData":[TD([[subQ2,1.0]])],"derivedFrom":subQ1}),1.0]])]});}
            var Q19;
            {var subQ0=sQuery(id+"F0.wireOp",EDGE,"E41");var subQ1=sQuery(id+"F0.wireOp",EDGE,"E1");var subQ2=makeQuery(id+"F0.imprint","INTERSECT",VERTEX,{"disambiguationData":[OD(1.0)],"derivedFrom":[subQ1,subQ0]});Q19=makeQuery(id+"F0.imprint","IMPRINT",FACE,{"disambiguationData":[TD([[makeQuery(id+"F0.imprint","IMPRINT",EDGE,{"disambiguationData":[TD([[subQ2,-1.0]])],"derivedFrom":subQ1}),-1.0]])]});}
            extrude(context, id + "F3", {"entities" : qUnion([Q0, Q1, Q2, Q3, Q4, Q5, Q6, Q7, Q8, Q9, Q10, Q11, Q12, Q13, Q14, Q15, Q16, Q17, Q18, Q19]), "operationType" : NewBodyOperationType.REMOVE, "depth" : 5 * mm, "offsetDistance" : 25 * mm});
        }
        {
            var Q0;
            {var subQ0=sQuery(id+"F0.wireOp",EDGE,"E41");var subQ1=sQuery(id+"F0.wireOp",EDGE,"E1");var subQ2=makeQuery(id+"F0.imprint","INTERSECT",VERTEX,{"disambiguationData":[OD(0.0)],"derivedFrom":[subQ1,subQ0]});Q0=makeQuery(id+"F0.imprint","IMPRINT",FACE,{"disambiguationData":[TD([[makeQuery(id+"F0.imprint","IMPRINT",EDGE,{"disambiguationData":[TD([[subQ2,1.0]])],"derivedFrom":subQ1}),-1.0]])]});}
            var Q1;
            {var subQ0=sQuery(id+"F0.wireOp",EDGE,"E41");var subQ1=sQuery(id+"F0.wireOp",EDGE,"E9");var subQ2=makeQuery(id+"F0.imprint","INTERSECT",VERTEX,{"disambiguationData":[OD(0.0)],"derivedFrom":[subQ1,subQ0]});Q1=makeQuery(id+"F0.imprint","IMPRINT",FACE,{"disambiguationData":[TD([[makeQuery(id+"F0.imprint","IMPRINT",EDGE,{"disambiguationData":[TD([[subQ2,1.0]])],"derivedFrom":subQ1}),-1.0]])]});}
            var Q2;
            {var subQ0=sQuery(id+"F0.wireOp",EDGE,"E41");var subQ1=sQuery(id+"F0.wireOp",EDGE,"E11");var subQ2=makeQuery(id+"F0.imprint","INTERSECT",VERTEX,{"disambiguationData":[OD(0.0)],"derivedFrom":[subQ1,subQ0]});Q2=makeQuery(id+"F0.imprint","IMPRINT",FACE,{"disambiguationData":[TD([[makeQuery(id+"F0.imprint","IMPRINT",EDGE,{"disambiguationData":[TD([[subQ2,1.0]])],"derivedFrom":subQ1}),-1.0]])]});}
            var Q3;
            {var subQ0=sQuery(id+"F0.wireOp",EDGE,"E41");var subQ1=sQuery(id+"F0.wireOp",EDGE,"E13");var subQ2=makeQuery(id+"F0.imprint","INTERSECT",VERTEX,{"disambiguationData":[OD(0.0)],"derivedFrom":[subQ1,subQ0]});Q3=makeQuery(id+"F0.imprint","IMPRINT",FACE,{"disambiguationData":[TD([[makeQuery(id+"F0.imprint","IMPRINT",EDGE,{"disambiguationData":[TD([[subQ2,1.0]])],"derivedFrom":subQ1}),-1.0]])]});}
            var Q4;
            {var subQ0=sQuery(id+"F0.wireOp",EDGE,"E41");var subQ1=sQuery(id+"F0.wireOp",EDGE,"E15");var subQ2=makeQuery(id+"F0.imprint","INTERSECT",VERTEX,{"disambiguationData":[OD(0.0)],"derivedFrom":[subQ1,subQ0]});Q4=makeQuery(id+"F0.imprint","IMPRINT",FACE,{"disambiguationData":[TD([[makeQuery(id+"F0.imprint","IMPRINT",EDGE,{"disambiguationData":[TD([[subQ2,1.0]])],"derivedFrom":subQ1}),-1.0]])]});}
            var Q5;
            {var subQ0=sQuery(id+"F0.wireOp",EDGE,"E41");var subQ1=sQuery(id+"F0.wireOp",EDGE,"E17");var subQ2=makeQuery(id+"F0.imprint","INTERSECT",VERTEX,{"disambiguationData":[OD(0.0)],"derivedFrom":[subQ1,subQ0]});Q5=makeQuery(id+"F0.imprint","IMPRINT",FACE,{"disambiguationData":[TD([[makeQuery(id+"F0.imprint","IMPRINT",EDGE,{"disambiguationData":[TD([[subQ2,1.0]])],"derivedFrom":subQ1}),1.0]])]});}
            var Q6;
            {var subQ0=sQuery(id+"F0.wireOp",EDGE,"E41");var subQ1=sQuery(id+"F0.wireOp",EDGE,"E18");var subQ2=makeQuery(id+"F0.imprint","INTERSECT",VERTEX,{"disambiguationData":[OD(0.0)],"derivedFrom":[subQ1,subQ0]});Q6=makeQuery(id+"F0.imprint","IMPRINT",FACE,{"disambiguationData":[TD([[makeQuery(id+"F0.imprint","IMPRINT",EDGE,{"disambiguationData":[TD([[subQ2,1.0]])],"derivedFrom":subQ1}),1.0]])]});}
            var Q7;
            {var subQ0=sQuery(id+"F0.wireOp",EDGE,"E41");var subQ1=sQuery(id+"F0.wireOp",EDGE,"E23");var subQ2=makeQuery(id+"F0.imprint","INTERSECT",VERTEX,{"disambiguationData":[OD(0.0)],"derivedFrom":[subQ1,subQ0]});Q7=makeQuery(id+"F0.imprint","IMPRINT",FACE,{"disambiguationData":[TD([[makeQuery(id+"F0.imprint","IMPRINT",EDGE,{"disambiguationData":[TD([[subQ2,1.0]])],"derivedFrom":subQ1}),1.0]])]});}
            var Q8;
            {var subQ0=sQuery(id+"F0.wireOp",EDGE,"E41");var subQ1=sQuery(id+"F0.wireOp",EDGE,"E25");var subQ2=makeQuery(id+"F0.imprint","INTERSECT",VERTEX,{"disambiguationData":[OD(0.0)],"derivedFrom":[subQ1,subQ0]});Q8=makeQuery(id+"F0.imprint","IMPRINT",FACE,{"disambiguationData":[TD([[makeQuery(id+"F0.imprint","IMPRINT",EDGE,{"disambiguationData":[TD([[subQ2,1.0]])],"derivedFrom":subQ1}),-1.0]])]});}
            var Q9;
            {var subQ0=sQuery(id+"F0.wireOp",EDGE,"E41");var subQ1=sQuery(id+"F0.wireOp",EDGE,"E27");var subQ2=makeQuery(id+"F0.imprint","INTERSECT",VERTEX,{"disambiguationData":[OD(0.0)],"derivedFrom":[subQ1,subQ0]});Q9=makeQuery(id+"F0.imprint","IMPRINT",FACE,{"disambiguationData":[TD([[makeQuery(id+"F0.imprint","IMPRINT",EDGE,{"disambiguationData":[TD([[subQ2,1.0]])],"derivedFrom":subQ1}),-1.0]])]});}
            var Q10;
            {var subQ0=sQuery(id+"F0.wireOp",EDGE,"E41");var subQ1=sQuery(id+"F0.wireOp",EDGE,"E0");var subQ2=makeQuery(id+"F0.imprint","INTERSECT",VERTEX,{"disambiguationData":[OD(0.0)],"derivedFrom":[subQ1,subQ0]});Q10=makeQuery(id+"F0.imprint","IMPRINT",FACE,{"disambiguationData":[TD([[makeQuery(id+"F0.imprint","IMPRINT",EDGE,{"disambiguationData":[TD([[subQ2,1.0]])],"derivedFrom":subQ1}),1.0]])]});}
            var Q11;
            {var subQ0=sQuery(id+"F0.wireOp",EDGE,"E41");var subQ1=sQuery(id+"F0.wireOp",EDGE,"E29");var subQ2=makeQuery(id+"F0.imprint","INTERSECT",VERTEX,{"disambiguationData":[OD(0.0)],"derivedFrom":[subQ1,subQ0]});Q11=makeQuery(id+"F0.imprint","IMPRINT",FACE,{"disambiguationData":[TD([[makeQuery(id+"F0.imprint","IMPRINT",EDGE,{"disambiguationData":[TD([[subQ2,1.0]])],"derivedFrom":subQ1}),-1.0]])]});}
            var Q12;
            {var subQ0=sQuery(id+"F0.wireOp",EDGE,"E41");var subQ1=sQuery(id+"F0.wireOp",EDGE,"E19");var subQ2=makeQuery(id+"F0.imprint","INTERSECT",VERTEX,{"disambiguationData":[OD(0.0)],"derivedFrom":[subQ1,subQ0]});Q12=makeQuery(id+"F0.imprint","IMPRINT",FACE,{"disambiguationData":[TD([[makeQuery(id+"F0.imprint","IMPRINT",EDGE,{"disambiguationData":[TD([[subQ2,1.0]])],"derivedFrom":subQ1}),-1.0]])]});}
            var Q13;
            {var subQ0=sQuery(id+"F0.wireOp",EDGE,"E41");var subQ1=sQuery(id+"F0.wireOp",EDGE,"E3");var subQ2=makeQuery(id+"F0.imprint","INTERSECT",VERTEX,{"disambiguationData":[OD(0.0)],"derivedFrom":[subQ1,subQ0]});Q13=makeQuery(id+"F0.imprint","IMPRINT",FACE,{"disambiguationData":[TD([[makeQuery(id+"F0.imprint","IMPRINT",EDGE,{"disambiguationData":[TD([[subQ2,1.0]])],"derivedFrom":subQ1}),-1.0]])]});}
            var Q14;
            {var subQ0=sQuery(id+"F0.wireOp",EDGE,"E41");var subQ1=sQuery(id+"F0.wireOp",EDGE,"E7");var subQ2=makeQuery(id+"F0.imprint","INTERSECT",VERTEX,{"disambiguationData":[OD(0.0)],"derivedFrom":[subQ1,subQ0]});Q14=makeQuery(id+"F0.imprint","IMPRINT",FACE,{"disambiguationData":[TD([[makeQuery(id+"F0.imprint","IMPRINT",EDGE,{"disambiguationData":[TD([[subQ2,1.0]])],"derivedFrom":subQ1}),-1.0]])]});}
            var Q15;
            {var subQ0=sQuery(id+"F0.wireOp",EDGE,"E41");var subQ1=sQuery(id+"F0.wireOp",EDGE,"E4");var subQ2=makeQuery(id+"F0.imprint","INTERSECT",VERTEX,{"disambiguationData":[OD(0.0)],"derivedFrom":[subQ1,subQ0]});Q15=makeQuery(id+"F0.imprint","IMPRINT",FACE,{"disambiguationData":[TD([[makeQuery(id+"F0.imprint","IMPRINT",EDGE,{"disambiguationData":[TD([[subQ2,1.0]])],"derivedFrom":subQ1}),1.0]])]});}
            var Q16;
            {var subQ0=sQuery(id+"F0.wireOp",EDGE,"E41");var subQ1=sQuery(id+"F0.wireOp",EDGE,"E37");var subQ2=makeQuery(id+"F0.imprint","INTERSECT",VERTEX,{"disambiguationData":[OD(0.0)],"derivedFrom":[subQ1,subQ0]});Q16=makeQuery(id+"F0.imprint","IMPRINT",FACE,{"disambiguationData":[TD([[makeQuery(id+"F0.imprint","IMPRINT",EDGE,{"disambiguationData":[TD([[subQ2,1.0]])],"derivedFrom":subQ1}),-1.0]])]});}
            var Q17;
            {var subQ0=sQuery(id+"F0.wireOp",EDGE,"E41");var subQ1=sQuery(id+"F0.wireOp",EDGE,"E35");var subQ2=makeQuery(id+"F0.imprint","INTERSECT",VERTEX,{"disambiguationData":[OD(0.0)],"derivedFrom":[subQ1,subQ0]});Q17=makeQuery(id+"F0.imprint","IMPRINT",FACE,{"disambiguationData":[TD([[makeQuery(id+"F0.imprint","IMPRINT",EDGE,{"disambiguationData":[TD([[subQ2,1.0]])],"derivedFrom":subQ1}),-1.0]])]});}
            var Q18;
            {var subQ0=sQuery(id+"F0.wireOp",EDGE,"E41");var subQ1=sQuery(id+"F0.wireOp",EDGE,"E33");var subQ2=makeQuery(id+"F0.imprint","INTERSECT",VERTEX,{"disambiguationData":[OD(0.0)],"derivedFrom":[subQ1,subQ0]});Q18=makeQuery(id+"F0.imprint","IMPRINT",FACE,{"disambiguationData":[TD([[makeQuery(id+"F0.imprint","IMPRINT",EDGE,{"disambiguationData":[TD([[subQ2,1.0]])],"derivedFrom":subQ1}),-1.0]])]});}
            var Q19;
            {var subQ0=sQuery(id+"F0.wireOp",EDGE,"E41");var subQ1=sQuery(id+"F0.wireOp",EDGE,"E31");var subQ2=makeQuery(id+"F0.imprint","INTERSECT",VERTEX,{"disambiguationData":[OD(0.0)],"derivedFrom":[subQ1,subQ0]});Q19=makeQuery(id+"F0.imprint","IMPRINT",FACE,{"disambiguationData":[TD([[makeQuery(id+"F0.imprint","IMPRINT",EDGE,{"disambiguationData":[TD([[subQ2,1.0]])],"derivedFrom":subQ1}),-1.0]])]});}
            extrude(context, id + "F4", {"entities" : qUnion([Q0, Q1, Q2, Q3, Q4, Q5, Q6, Q7, Q8, Q9, Q10, Q11, Q12, Q13, Q14, Q15, Q16, Q17, Q18, Q19]), "operationType" : NewBodyOperationType.REMOVE, "depth" : 5 * mm, "offsetDistance" : 25 * mm});
        }
        {
            var Q0;
            {var subQ0=sQuery(id+"F0.wireOp",EDGE,"E42");var subQ1=sQuery(id+"F0.wireOp",EDGE,"E1");var subQ2=makeQuery(id+"F0.imprint","INTERSECT",VERTEX,{"derivedFrom":[subQ1,subQ0]});Q0=makeQuery(id+"F0.imprint","IMPRINT",FACE,{"disambiguationData":[TD([[makeQuery(id+"F0.imprint","IMPRINT",EDGE,{"disambiguationData":[TD([[subQ2,-1.0]])],"derivedFrom":subQ1}),-1.0]])]});}
            var Q1;
            {var subQ0=sQuery(id+"F0.wireOp",EDGE,"E42");var subQ1=sQuery(id+"F0.wireOp",EDGE,"E3");var subQ2=makeQuery(id+"F0.imprint","INTERSECT",VERTEX,{"derivedFrom":[subQ1,subQ0]});Q1=makeQuery(id+"F0.imprint","IMPRINT",FACE,{"disambiguationData":[TD([[makeQuery(id+"F0.imprint","IMPRINT",EDGE,{"disambiguationData":[TD([[subQ2,-1.0]])],"derivedFrom":subQ1}),-1.0]])]});}
            var Q2;
            {var subQ0=sQuery(id+"F0.wireOp",EDGE,"E42");var subQ1=sQuery(id+"F0.wireOp",EDGE,"E4");var subQ2=makeQuery(id+"F0.imprint","INTERSECT",VERTEX,{"derivedFrom":[subQ1,subQ0]});Q2=makeQuery(id+"F0.imprint","IMPRINT",FACE,{"disambiguationData":[TD([[makeQuery(id+"F0.imprint","IMPRINT",EDGE,{"disambiguationData":[TD([[subQ2,-1.0]])],"derivedFrom":subQ1}),1.0]])]});}
            var Q3;
            {var subQ0=sQuery(id+"F0.wireOp",EDGE,"E42");var subQ1=sQuery(id+"F0.wireOp",EDGE,"E7");var subQ2=makeQuery(id+"F0.imprint","INTERSECT",VERTEX,{"derivedFrom":[subQ1,subQ0]});Q3=makeQuery(id+"F0.imprint","IMPRINT",FACE,{"disambiguationData":[TD([[makeQuery(id+"F0.imprint","IMPRINT",EDGE,{"disambiguationData":[TD([[subQ2,-1.0]])],"derivedFrom":subQ1}),-1.0]])]});}
            var Q4;
            {var subQ0=sQuery(id+"F0.wireOp",EDGE,"E42");var subQ1=sQuery(id+"F0.wireOp",EDGE,"E9");var subQ2=makeQuery(id+"F0.imprint","INTERSECT",VERTEX,{"derivedFrom":[subQ1,subQ0]});Q4=makeQuery(id+"F0.imprint","IMPRINT",FACE,{"disambiguationData":[TD([[makeQuery(id+"F0.imprint","IMPRINT",EDGE,{"disambiguationData":[TD([[subQ2,-1.0]])],"derivedFrom":subQ1}),-1.0]])]});}
            var Q5;
            {var subQ0=sQuery(id+"F0.wireOp",EDGE,"E42");var subQ1=sQuery(id+"F0.wireOp",EDGE,"E11");var subQ2=makeQuery(id+"F0.imprint","INTERSECT",VERTEX,{"derivedFrom":[subQ1,subQ0]});Q5=makeQuery(id+"F0.imprint","IMPRINT",FACE,{"disambiguationData":[TD([[makeQuery(id+"F0.imprint","IMPRINT",EDGE,{"disambiguationData":[TD([[subQ2,-1.0]])],"derivedFrom":subQ1}),-1.0]])]});}
            var Q6;
            {var subQ0=sQuery(id+"F0.wireOp",EDGE,"E42");var subQ1=sQuery(id+"F0.wireOp",EDGE,"E13");var subQ2=makeQuery(id+"F0.imprint","INTERSECT",VERTEX,{"derivedFrom":[subQ1,subQ0]});Q6=makeQuery(id+"F0.imprint","IMPRINT",FACE,{"disambiguationData":[TD([[makeQuery(id+"F0.imprint","IMPRINT",EDGE,{"disambiguationData":[TD([[subQ2,-1.0]])],"derivedFrom":subQ1}),-1.0]])]});}
            var Q7;
            {var subQ0=sQuery(id+"F0.wireOp",EDGE,"E42");var subQ1=sQuery(id+"F0.wireOp",EDGE,"E15");var subQ2=makeQuery(id+"F0.imprint","INTERSECT",VERTEX,{"derivedFrom":[subQ1,subQ0]});Q7=makeQuery(id+"F0.imprint","IMPRINT",FACE,{"disambiguationData":[TD([[makeQuery(id+"F0.imprint","IMPRINT",EDGE,{"disambiguationData":[TD([[subQ2,-1.0]])],"derivedFrom":subQ1}),-1.0]])]});}
            var Q8;
            {var subQ0=sQuery(id+"F0.wireOp",EDGE,"E42");var subQ1=sQuery(id+"F0.wireOp",EDGE,"E17");var subQ2=makeQuery(id+"F0.imprint","INTERSECT",VERTEX,{"derivedFrom":[subQ1,subQ0]});Q8=makeQuery(id+"F0.imprint","IMPRINT",FACE,{"disambiguationData":[TD([[makeQuery(id+"F0.imprint","IMPRINT",EDGE,{"disambiguationData":[TD([[subQ2,-1.0]])],"derivedFrom":subQ1}),1.0]])]});}
            var Q9;
            {var subQ0=sQuery(id+"F0.wireOp",EDGE,"E42");var subQ1=sQuery(id+"F0.wireOp",EDGE,"E18");var subQ2=makeQuery(id+"F0.imprint","INTERSECT",VERTEX,{"derivedFrom":[subQ1,subQ0]});Q9=makeQuery(id+"F0.imprint","IMPRINT",FACE,{"disambiguationData":[TD([[makeQuery(id+"F0.imprint","IMPRINT",EDGE,{"disambiguationData":[TD([[subQ2,-1.0]])],"derivedFrom":subQ1}),1.0]])]});}
            var Q10;
            {var subQ0=sQuery(id+"F0.wireOp",EDGE,"E42");var subQ1=sQuery(id+"F0.wireOp",EDGE,"E19");var subQ2=makeQuery(id+"F0.imprint","INTERSECT",VERTEX,{"derivedFrom":[subQ1,subQ0]});Q10=makeQuery(id+"F0.imprint","IMPRINT",FACE,{"disambiguationData":[TD([[makeQuery(id+"F0.imprint","IMPRINT",EDGE,{"disambiguationData":[TD([[subQ2,-1.0]])],"derivedFrom":subQ1}),-1.0]])]});}
            var Q11;
            {var subQ0=sQuery(id+"F0.wireOp",EDGE,"E42");var subQ1=sQuery(id+"F0.wireOp",EDGE,"E23");var subQ2=makeQuery(id+"F0.imprint","INTERSECT",VERTEX,{"derivedFrom":[subQ1,subQ0]});Q11=makeQuery(id+"F0.imprint","IMPRINT",FACE,{"disambiguationData":[TD([[makeQuery(id+"F0.imprint","IMPRINT",EDGE,{"disambiguationData":[TD([[subQ2,-1.0]])],"derivedFrom":subQ1}),1.0]])]});}
            var Q12;
            {var subQ0=sQuery(id+"F0.wireOp",EDGE,"E42");var subQ1=sQuery(id+"F0.wireOp",EDGE,"E25");var subQ2=makeQuery(id+"F0.imprint","INTERSECT",VERTEX,{"derivedFrom":[subQ1,subQ0]});Q12=makeQuery(id+"F0.imprint","IMPRINT",FACE,{"disambiguationData":[TD([[makeQuery(id+"F0.imprint","IMPRINT",EDGE,{"disambiguationData":[TD([[subQ2,-1.0]])],"derivedFrom":subQ1}),-1.0]])]});}
            var Q13;
            {var subQ0=sQuery(id+"F0.wireOp",EDGE,"E42");var subQ1=sQuery(id+"F0.wireOp",EDGE,"E27");var subQ2=makeQuery(id+"F0.imprint","INTERSECT",VERTEX,{"derivedFrom":[subQ1,subQ0]});Q13=makeQuery(id+"F0.imprint","IMPRINT",FACE,{"disambiguationData":[TD([[makeQuery(id+"F0.imprint","IMPRINT",EDGE,{"disambiguationData":[TD([[subQ2,-1.0]])],"derivedFrom":subQ1}),-1.0]])]});}
            var Q14;
            {var subQ0=sQuery(id+"F0.wireOp",EDGE,"E42");var subQ1=sQuery(id+"F0.wireOp",EDGE,"E29");var subQ2=makeQuery(id+"F0.imprint","INTERSECT",VERTEX,{"derivedFrom":[subQ1,subQ0]});Q14=makeQuery(id+"F0.imprint","IMPRINT",FACE,{"disambiguationData":[TD([[makeQuery(id+"F0.imprint","IMPRINT",EDGE,{"disambiguationData":[TD([[subQ2,-1.0]])],"derivedFrom":subQ1}),-1.0]])]});}
            var Q15;
            {var subQ0=sQuery(id+"F0.wireOp",EDGE,"E42");var subQ1=sQuery(id+"F0.wireOp",EDGE,"E31");var subQ2=makeQuery(id+"F0.imprint","INTERSECT",VERTEX,{"derivedFrom":[subQ1,subQ0]});Q15=makeQuery(id+"F0.imprint","IMPRINT",FACE,{"disambiguationData":[TD([[makeQuery(id+"F0.imprint","IMPRINT",EDGE,{"disambiguationData":[TD([[subQ2,-1.0]])],"derivedFrom":subQ1}),-1.0]])]});}
            var Q16;
            {var subQ0=sQuery(id+"F0.wireOp",EDGE,"E42");var subQ1=sQuery(id+"F0.wireOp",EDGE,"E33");var subQ2=makeQuery(id+"F0.imprint","INTERSECT",VERTEX,{"derivedFrom":[subQ1,subQ0]});Q16=makeQuery(id+"F0.imprint","IMPRINT",FACE,{"disambiguationData":[TD([[makeQuery(id+"F0.imprint","IMPRINT",EDGE,{"disambiguationData":[TD([[subQ2,-1.0]])],"derivedFrom":subQ1}),-1.0]])]});}
            var Q17;
            {var subQ0=sQuery(id+"F0.wireOp",EDGE,"E42");var subQ1=sQuery(id+"F0.wireOp",EDGE,"E35");var subQ2=makeQuery(id+"F0.imprint","INTERSECT",VERTEX,{"derivedFrom":[subQ1,subQ0]});Q17=makeQuery(id+"F0.imprint","IMPRINT",FACE,{"disambiguationData":[TD([[makeQuery(id+"F0.imprint","IMPRINT",EDGE,{"disambiguationData":[TD([[subQ2,-1.0]])],"derivedFrom":subQ1}),-1.0]])]});}
            var Q18;
            {var subQ0=sQuery(id+"F0.wireOp",EDGE,"E42");var subQ1=sQuery(id+"F0.wireOp",EDGE,"E37");var subQ2=makeQuery(id+"F0.imprint","INTERSECT",VERTEX,{"derivedFrom":[subQ1,subQ0]});Q18=makeQuery(id+"F0.imprint","IMPRINT",FACE,{"disambiguationData":[TD([[makeQuery(id+"F0.imprint","IMPRINT",EDGE,{"disambiguationData":[TD([[subQ2,-1.0]])],"derivedFrom":subQ1}),-1.0]])]});}
            var Q19;
            {var subQ0=sQuery(id+"F0.wireOp",EDGE,"E40");var subQ1=sQuery(id+"F0.wireOp",EDGE,"E0");var subQ2=makeQuery(id+"F0.imprint","INTERSECT",VERTEX,{"disambiguationData":[OD(0.0)],"derivedFrom":[subQ1,subQ0]});Q19=makeQuery(id+"F0.imprint","IMPRINT",FACE,{"disambiguationData":[TD([[makeQuery(id+"F0.imprint","IMPRINT",EDGE,{"disambiguationData":[TD([[subQ2,1.0]])],"derivedFrom":subQ1}),1.0]])]});}
            extrude(context, id + "F5", {"entities" : qUnion([Q0, Q1, Q2, Q3, Q4, Q5, Q6, Q7, Q8, Q9, Q10, Q11, Q12, Q13, Q14, Q15, Q16, Q17, Q18, Q19]), "operationType" : NewBodyOperationType.REMOVE, "depth" : 5 * mm, "offsetDistance" : 25 * mm});
        }
        {
            var Q0;
            {var subQ0=sQuery(id+"F0.wireOp",EDGE,"E40");var subQ1=sQuery(id+"F0.wireOp",EDGE,"E1");var subQ2=makeQuery(id+"F0.imprint","INTERSECT",VERTEX,{"disambiguationData":[OD(0.0)],"derivedFrom":[subQ1,subQ0]});Q0=makeQuery(id+"F0.imprint","IMPRINT",FACE,{"disambiguationData":[TD([[makeQuery(id+"F0.imprint","IMPRINT",EDGE,{"disambiguationData":[TD([[subQ2,-1.0]])],"derivedFrom":subQ1}),-1.0]])]});}
            var Q1;
            {var subQ0=sQuery(id+"F0.wireOp",EDGE,"E40");var subQ1=sQuery(id+"F0.wireOp",EDGE,"E3");var subQ2=makeQuery(id+"F0.imprint","INTERSECT",VERTEX,{"disambiguationData":[OD(0.0)],"derivedFrom":[subQ1,subQ0]});Q1=makeQuery(id+"F0.imprint","IMPRINT",FACE,{"disambiguationData":[TD([[makeQuery(id+"F0.imprint","IMPRINT",EDGE,{"disambiguationData":[TD([[subQ2,-1.0]])],"derivedFrom":subQ1}),-1.0]])]});}
            var Q2;
            {var subQ0=sQuery(id+"F0.wireOp",EDGE,"E40");var subQ1=sQuery(id+"F0.wireOp",EDGE,"E4");var subQ2=makeQuery(id+"F0.imprint","INTERSECT",VERTEX,{"disambiguationData":[OD(0.0)],"derivedFrom":[subQ1,subQ0]});Q2=makeQuery(id+"F0.imprint","IMPRINT",FACE,{"disambiguationData":[TD([[makeQuery(id+"F0.imprint","IMPRINT",EDGE,{"disambiguationData":[TD([[subQ2,-1.0]])],"derivedFrom":subQ1}),1.0]])]});}
            var Q3;
            {var subQ0=sQuery(id+"F0.wireOp",EDGE,"E40");var subQ1=sQuery(id+"F0.wireOp",EDGE,"E7");var subQ2=makeQuery(id+"F0.imprint","INTERSECT",VERTEX,{"disambiguationData":[OD(0.0)],"derivedFrom":[subQ1,subQ0]});Q3=makeQuery(id+"F0.imprint","IMPRINT",FACE,{"disambiguationData":[TD([[makeQuery(id+"F0.imprint","IMPRINT",EDGE,{"disambiguationData":[TD([[subQ2,-1.0]])],"derivedFrom":subQ1}),-1.0]])]});}
            var Q4;
            {var subQ0=sQuery(id+"F0.wireOp",EDGE,"E40");var subQ1=sQuery(id+"F0.wireOp",EDGE,"E9");var subQ2=makeQuery(id+"F0.imprint","INTERSECT",VERTEX,{"disambiguationData":[OD(0.0)],"derivedFrom":[subQ1,subQ0]});Q4=makeQuery(id+"F0.imprint","IMPRINT",FACE,{"disambiguationData":[TD([[makeQuery(id+"F0.imprint","IMPRINT",EDGE,{"disambiguationData":[TD([[subQ2,-1.0]])],"derivedFrom":subQ1}),-1.0]])]});}
            var Q5;
            {var subQ0=sQuery(id+"F0.wireOp",EDGE,"E40");var subQ1=sQuery(id+"F0.wireOp",EDGE,"E11");var subQ2=makeQuery(id+"F0.imprint","INTERSECT",VERTEX,{"disambiguationData":[OD(0.0)],"derivedFrom":[subQ1,subQ0]});Q5=makeQuery(id+"F0.imprint","IMPRINT",FACE,{"disambiguationData":[TD([[makeQuery(id+"F0.imprint","IMPRINT",EDGE,{"disambiguationData":[TD([[subQ2,-1.0]])],"derivedFrom":subQ1}),-1.0]])]});}
            var Q6;
            {var subQ0=sQuery(id+"F0.wireOp",EDGE,"E40");var subQ1=sQuery(id+"F0.wireOp",EDGE,"E13");var subQ2=makeQuery(id+"F0.imprint","INTERSECT",VERTEX,{"disambiguationData":[OD(0.0)],"derivedFrom":[subQ1,subQ0]});Q6=makeQuery(id+"F0.imprint","IMPRINT",FACE,{"disambiguationData":[TD([[makeQuery(id+"F0.imprint","IMPRINT",EDGE,{"disambiguationData":[TD([[subQ2,-1.0]])],"derivedFrom":subQ1}),-1.0]])]});}
            var Q7;
            {var subQ0=sQuery(id+"F0.wireOp",EDGE,"E40");var subQ1=sQuery(id+"F0.wireOp",EDGE,"E15");var subQ2=makeQuery(id+"F0.imprint","INTERSECT",VERTEX,{"disambiguationData":[OD(0.0)],"derivedFrom":[subQ1,subQ0]});Q7=makeQuery(id+"F0.imprint","IMPRINT",FACE,{"disambiguationData":[TD([[makeQuery(id+"F0.imprint","IMPRINT",EDGE,{"disambiguationData":[TD([[subQ2,-1.0]])],"derivedFrom":subQ1}),-1.0]])]});}
            var Q8;
            {var subQ0=sQuery(id+"F0.wireOp",EDGE,"E40");var subQ1=sQuery(id+"F0.wireOp",EDGE,"E17");var subQ2=makeQuery(id+"F0.imprint","INTERSECT",VERTEX,{"disambiguationData":[OD(0.0)],"derivedFrom":[subQ1,subQ0]});Q8=makeQuery(id+"F0.imprint","IMPRINT",FACE,{"disambiguationData":[TD([[makeQuery(id+"F0.imprint","IMPRINT",EDGE,{"disambiguationData":[TD([[subQ2,-1.0]])],"derivedFrom":subQ1}),1.0]])]});}
            var Q9;
            {var subQ0=sQuery(id+"F0.wireOp",EDGE,"E40");var subQ1=sQuery(id+"F0.wireOp",EDGE,"E18");var subQ2=makeQuery(id+"F0.imprint","INTERSECT",VERTEX,{"disambiguationData":[OD(0.0)],"derivedFrom":[subQ1,subQ0]});Q9=makeQuery(id+"F0.imprint","IMPRINT",FACE,{"disambiguationData":[TD([[makeQuery(id+"F0.imprint","IMPRINT",EDGE,{"disambiguationData":[TD([[subQ2,-1.0]])],"derivedFrom":subQ1}),1.0]])]});}
            var Q10;
            {var subQ0=sQuery(id+"F0.wireOp",EDGE,"E40");var subQ1=sQuery(id+"F0.wireOp",EDGE,"E19");var subQ2=makeQuery(id+"F0.imprint","INTERSECT",VERTEX,{"disambiguationData":[OD(0.0)],"derivedFrom":[subQ1,subQ0]});Q10=makeQuery(id+"F0.imprint","IMPRINT",FACE,{"disambiguationData":[TD([[makeQuery(id+"F0.imprint","IMPRINT",EDGE,{"disambiguationData":[TD([[subQ2,-1.0]])],"derivedFrom":subQ1}),-1.0]])]});}
            var Q11;
            {var subQ0=sQuery(id+"F0.wireOp",EDGE,"E40");var subQ1=sQuery(id+"F0.wireOp",EDGE,"E23");var subQ2=makeQuery(id+"F0.imprint","INTERSECT",VERTEX,{"disambiguationData":[OD(0.0)],"derivedFrom":[subQ1,subQ0]});Q11=makeQuery(id+"F0.imprint","IMPRINT",FACE,{"disambiguationData":[TD([[makeQuery(id+"F0.imprint","IMPRINT",EDGE,{"disambiguationData":[TD([[subQ2,-1.0]])],"derivedFrom":subQ1}),1.0]])]});}
            var Q12;
            {var subQ0=sQuery(id+"F0.wireOp",EDGE,"E40");var subQ1=sQuery(id+"F0.wireOp",EDGE,"E25");var subQ2=makeQuery(id+"F0.imprint","INTERSECT",VERTEX,{"disambiguationData":[OD(0.0)],"derivedFrom":[subQ1,subQ0]});Q12=makeQuery(id+"F0.imprint","IMPRINT",FACE,{"disambiguationData":[TD([[makeQuery(id+"F0.imprint","IMPRINT",EDGE,{"disambiguationData":[TD([[subQ2,-1.0]])],"derivedFrom":subQ1}),-1.0]])]});}
            var Q13;
            {var subQ0=sQuery(id+"F0.wireOp",EDGE,"E40");var subQ1=sQuery(id+"F0.wireOp",EDGE,"E27");var subQ2=makeQuery(id+"F0.imprint","INTERSECT",VERTEX,{"disambiguationData":[OD(0.0)],"derivedFrom":[subQ1,subQ0]});Q13=makeQuery(id+"F0.imprint","IMPRINT",FACE,{"disambiguationData":[TD([[makeQuery(id+"F0.imprint","IMPRINT",EDGE,{"disambiguationData":[TD([[subQ2,-1.0]])],"derivedFrom":subQ1}),-1.0]])]});}
            var Q14;
            {var subQ0=sQuery(id+"F0.wireOp",EDGE,"E40");var subQ1=sQuery(id+"F0.wireOp",EDGE,"E29");var subQ2=makeQuery(id+"F0.imprint","INTERSECT",VERTEX,{"disambiguationData":[OD(0.0)],"derivedFrom":[subQ1,subQ0]});Q14=makeQuery(id+"F0.imprint","IMPRINT",FACE,{"disambiguationData":[TD([[makeQuery(id+"F0.imprint","IMPRINT",EDGE,{"disambiguationData":[TD([[subQ2,-1.0]])],"derivedFrom":subQ1}),-1.0]])]});}
            var Q15;
            {var subQ0=sQuery(id+"F0.wireOp",EDGE,"E40");var subQ1=sQuery(id+"F0.wireOp",EDGE,"E31");var subQ2=makeQuery(id+"F0.imprint","INTERSECT",VERTEX,{"disambiguationData":[OD(0.0)],"derivedFrom":[subQ1,subQ0]});Q15=makeQuery(id+"F0.imprint","IMPRINT",FACE,{"disambiguationData":[TD([[makeQuery(id+"F0.imprint","IMPRINT",EDGE,{"disambiguationData":[TD([[subQ2,-1.0]])],"derivedFrom":subQ1}),-1.0]])]});}
            var Q16;
            {var subQ0=sQuery(id+"F0.wireOp",EDGE,"E40");var subQ1=sQuery(id+"F0.wireOp",EDGE,"E33");var subQ2=makeQuery(id+"F0.imprint","INTERSECT",VERTEX,{"disambiguationData":[OD(0.0)],"derivedFrom":[subQ1,subQ0]});Q16=makeQuery(id+"F0.imprint","IMPRINT",FACE,{"disambiguationData":[TD([[makeQuery(id+"F0.imprint","IMPRINT",EDGE,{"disambiguationData":[TD([[subQ2,-1.0]])],"derivedFrom":subQ1}),-1.0]])]});}
            var Q17;
            {var subQ0=sQuery(id+"F0.wireOp",EDGE,"E40");var subQ1=sQuery(id+"F0.wireOp",EDGE,"E35");var subQ2=makeQuery(id+"F0.imprint","INTERSECT",VERTEX,{"disambiguationData":[OD(0.0)],"derivedFrom":[subQ1,subQ0]});Q17=makeQuery(id+"F0.imprint","IMPRINT",FACE,{"disambiguationData":[TD([[makeQuery(id+"F0.imprint","IMPRINT",EDGE,{"disambiguationData":[TD([[subQ2,-1.0]])],"derivedFrom":subQ1}),-1.0]])]});}
            var Q18;
            {var subQ0=sQuery(id+"F0.wireOp",EDGE,"E40");var subQ1=sQuery(id+"F0.wireOp",EDGE,"E37");var subQ2=makeQuery(id+"F0.imprint","INTERSECT",VERTEX,{"disambiguationData":[OD(0.0)],"derivedFrom":[subQ1,subQ0]});Q18=makeQuery(id+"F0.imprint","IMPRINT",FACE,{"disambiguationData":[TD([[makeQuery(id+"F0.imprint","IMPRINT",EDGE,{"disambiguationData":[TD([[subQ2,-1.0]])],"derivedFrom":subQ1}),-1.0]])]});}
            var Q19;
            {var subQ0=sQuery(id+"F0.wireOp",EDGE,"E40");var subQ1=sQuery(id+"F0.wireOp",EDGE,"E0");var subQ2=makeQuery(id+"F0.imprint","INTERSECT",VERTEX,{"disambiguationData":[OD(0.0)],"derivedFrom":[subQ1,subQ0]});Q19=makeQuery(id+"F0.imprint","IMPRINT",FACE,{"disambiguationData":[TD([[makeQuery(id+"F0.imprint","IMPRINT",EDGE,{"disambiguationData":[TD([[subQ2,-1.0]])],"derivedFrom":subQ1}),1.0]])]});}
            extrude(context, id + "F6", {"entities" : qUnion([Q0, Q1, Q2, Q3, Q4, Q5, Q6, Q7, Q8, Q9, Q10, Q11, Q12, Q13, Q14, Q15, Q16, Q17, Q18, Q19]), "operationType" : NewBodyOperationType.REMOVE, "depth" : 10 * mm, "offsetDistance" : 25 * mm});
        }
        {
            var Q0;
            {var subQ1=sQuery(id+"F0.wireOp",EDGE,"E40");var subQ3=sQuery(id+"F0.wireOp",EDGE,"E46");var subQ4=makeQuery(id+"F0.imprint","INTERSECT",VERTEX,{"disambiguationData":[OD(0.0)],"derivedFrom":[subQ1,subQ3]});Q0=makeQuery(id+"F0.imprint","IMPRINT",FACE,{"disambiguationData":[TD([[makeQuery(id+"F0.imprint","IMPRINT",EDGE,{"disambiguationData":[TD([[subQ4,-1.0]])],"derivedFrom":subQ3}),1.0]])]});}
            var Q1;
            {var subQ1=sQuery(id+"F0.wireOp",EDGE,"E41");var subQ3=sQuery(id+"F0.wireOp",EDGE,"E46");var subQ4=makeQuery(id+"F0.imprint","INTERSECT",VERTEX,{"disambiguationData":[OD(1.0)],"derivedFrom":[subQ1,subQ3]});Q1=makeQuery(id+"F0.imprint","IMPRINT",FACE,{"disambiguationData":[TD([[makeQuery(id+"F0.imprint","IMPRINT",EDGE,{"disambiguationData":[TD([[subQ4,1.0]])],"derivedFrom":subQ3}),1.0]])]});}
            var Q2;
            {var subQ1=sQuery(id+"F0.wireOp",EDGE,"E40");var subQ3=sQuery(id+"F0.wireOp",EDGE,"E46");var subQ4=makeQuery(id+"F0.imprint","INTERSECT",VERTEX,{"disambiguationData":[OD(1.0)],"derivedFrom":[subQ1,subQ3]});Q2=makeQuery(id+"F0.imprint","IMPRINT",FACE,{"disambiguationData":[TD([[makeQuery(id+"F0.imprint","IMPRINT",EDGE,{"disambiguationData":[TD([[subQ4,1.0]])],"derivedFrom":subQ3}),1.0]])]});}
            var Q3;
            {var subQ1=sQuery(id+"F0.wireOp",EDGE,"E40");var subQ3=sQuery(id+"F0.wireOp",EDGE,"E46");var subQ4=makeQuery(id+"F0.imprint","INTERSECT",VERTEX,{"disambiguationData":[OD(1.0)],"derivedFrom":[subQ1,subQ3]});Q3=makeQuery(id+"F0.imprint","IMPRINT",FACE,{"disambiguationData":[TD([[makeQuery(id+"F0.imprint","IMPRINT",EDGE,{"disambiguationData":[TD([[subQ4,-1.0]])],"derivedFrom":subQ3}),1.0]])]});}
            var Q4;
            {var subQ1=sQuery(id+"F0.wireOp",EDGE,"E41");var subQ3=sQuery(id+"F0.wireOp",EDGE,"E46");var subQ4=makeQuery(id+"F0.imprint","INTERSECT",VERTEX,{"disambiguationData":[OD(0.0)],"derivedFrom":[subQ1,subQ3]});Q4=makeQuery(id+"F0.imprint","IMPRINT",FACE,{"disambiguationData":[TD([[makeQuery(id+"F0.imprint","IMPRINT",EDGE,{"disambiguationData":[TD([[subQ4,1.0]])],"derivedFrom":subQ3}),1.0]])]});}
            var Q5;
            {var subQ1=sQuery(id+"F0.wireOp",EDGE,"E41");var subQ3=sQuery(id+"F0.wireOp",EDGE,"E46");var subQ4=makeQuery(id+"F0.imprint","INTERSECT",VERTEX,{"disambiguationData":[OD(0.0)],"derivedFrom":[subQ1,subQ3]});Q5=makeQuery(id+"F0.imprint","IMPRINT",FACE,{"disambiguationData":[TD([[makeQuery(id+"F0.imprint","IMPRINT",EDGE,{"disambiguationData":[TD([[subQ4,-1.0]])],"derivedFrom":subQ3}),1.0]])]});}
            var Q6;
            {var subQ1=sQuery(id+"F0.wireOp",EDGE,"E40");var subQ3=sQuery(id+"F0.wireOp",EDGE,"E46");var subQ4=makeQuery(id+"F0.imprint","INTERSECT",VERTEX,{"disambiguationData":[OD(0.0)],"derivedFrom":[subQ1,subQ3]});Q6=makeQuery(id+"F0.imprint","IMPRINT",FACE,{"disambiguationData":[TD([[makeQuery(id+"F0.imprint","IMPRINT",EDGE,{"disambiguationData":[TD([[subQ4,1.0]])],"derivedFrom":subQ3}),1.0]])]});}
            extrude(context, id + "F7", {"entities" : qUnion([Q0, Q1, Q2, Q3, Q4, Q5, Q6]), "depth" : 26 * mm, "offsetDistance" : 25 * mm});
        }
    });
